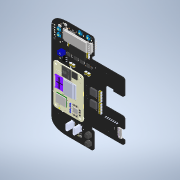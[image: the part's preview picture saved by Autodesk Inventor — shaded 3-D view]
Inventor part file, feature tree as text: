
AUTODESK INVENTOR PART (.ipt)
format: ipt  version: 2022 (Build 260153000, 153)  size: 56,215,552 bytes
history: native  units: mm
features: other x3630, sketch x2440, extrude x2
ambient origin geometry x8: Origin, YZ Plane, XZ Plane, XY Plane, X Axis, Y Axis, Z Axis, Center Point
bodies: Body1 (feature_tree), Body2 (feature_tree), Body3 (feature_tree), Body4 (feature_tree), Body5 (feature_tree), Body6 (feature_tree), Body7 (feature_tree), Body8 (feature_tree), Body9 (feature_tree), Body10 (feature_tree), Body11 (feature_tree), Body12 (feature_tree), Body13 (feature_tree), Body14 (feature_tree), Body15 (feature_tree), Body16 (feature_tree), Body17 (feature_tree), Body18 (feature_tree), Body19 (feature_tree), Body20 (feature_tree), Body21 (feature_tree), Body22 (feature_tree), Body23 (feature_tree), Body24 (feature_tree), Body25 (feature_tree), Body26 (feature_tree), Body27 (feature_tree), Body28 (feature_tree), Body29 (feature_tree), Body30 (feature_tree), Body31 (feature_tree), Body32 (feature_tree), Body33 (feature_tree), Body34 (feature_tree), Body35 (feature_tree), Body36 (feature_tree), Body37 (feature_tree), Body38 (feature_tree), Body39 (feature_tree), Body40 (feature_tree), Body41 (feature_tree), Body42 (feature_tree), Body43 (feature_tree), Body44 (feature_tree), Body45 (feature_tree), Body46 (feature_tree), Body47 (feature_tree), Body48 (feature_tree), Body49 (feature_tree), Body50 (feature_tree), Body51 (feature_tree), Body52 (feature_tree), Body53 (feature_tree), Body54 (feature_tree), Body55 (feature_tree), Body56 (feature_tree), Body57 (feature_tree), Body58 (feature_tree), Body59 (feature_tree), Body60 (feature_tree), Body61 (feature_tree), Body62 (feature_tree), Body63 (feature_tree), Body64 (feature_tree), Body65 (feature_tree), Body66 (feature_tree), Body67 (feature_tree), Body68 (feature_tree), Body69 (feature_tree), Body70 (feature_tree), Body71 (feature_tree), Body72 (feature_tree), Body73 (feature_tree), Body74 (feature_tree), Body75 (feature_tree), Body76 (feature_tree), Body77 (feature_tree), Body78 (feature_tree), Body79 (feature_tree), Body80 (feature_tree), Body81 (feature_tree), Body82 (feature_tree), Body83 (feature_tree), Body84 (feature_tree), Body85 (feature_tree), Body86 (feature_tree), Body87 (feature_tree), Body88 (feature_tree), Body89 (feature_tree), Body90 (feature_tree), Body91 (feature_tree), Body92 (feature_tree), Body93 (feature_tree), Body94 (feature_tree), Body95 (feature_tree), Body96 (feature_tree), Body97 (feature_tree), Body98 (feature_tree), Body99 (feature_tree), Body100 (feature_tree), Body101 (feature_tree), Body102 (feature_tree), Body103 (feature_tree), Body104 (feature_tree), Body105 (feature_tree), Body106 (feature_tree), Body107 (feature_tree), Body108 (feature_tree), Body109 (feature_tree), Body110 (feature_tree), Body111 (feature_tree), Body112 (feature_tree), Body113 (feature_tree), Body114 (feature_tree), Body115 (feature_tree), Body116 (feature_tree), Body117 (feature_tree), Body118 (feature_tree), Body119 (feature_tree), Body120 (feature_tree), Body121 (feature_tree), Body122 (feature_tree), Body123 (feature_tree), Body124 (feature_tree), Body125 (feature_tree), Body126 (feature_tree), Body127 (feature_tree), Body128 (feature_tree), Body129 (feature_tree), Body130 (feature_tree), Body131 (feature_tree), Body132 (feature_tree), Body133 (feature_tree), Body134 (feature_tree), Body135 (feature_tree), Body136 (feature_tree), Body137 (feature_tree), Body138 (feature_tree), Body139 (feature_tree), Body140 (feature_tree), Body141 (feature_tree), Body142 (feature_tree), Body143 (feature_tree), Body144 (feature_tree), Body145 (feature_tree), Body146 (feature_tree), Body147 (feature_tree), Body148 (feature_tree), Body149 (feature_tree), Body150 (feature_tree), Body151 (feature_tree), Body152 (feature_tree), Body153 (feature_tree), Body154 (feature_tree), Body155 (feature_tree), Body156 (feature_tree), Body157 (feature_tree), Body158 (feature_tree), Body159 (feature_tree), Body160 (feature_tree), Body161 (feature_tree), Body162 (feature_tree), Body163 (feature_tree), Body164 (feature_tree), Body165 (feature_tree), Body166 (feature_tree), Body167 (feature_tree), Body168 (feature_tree), Body169 (feature_tree), Body170 (feature_tree), Body171 (feature_tree), Body172 (feature_tree), Body173 (feature_tree), Body174 (feature_tree), Body175 (feature_tree), Body176 (feature_tree), Body177 (feature_tree), Body178 (feature_tree), Body179 (feature_tree), Body180 (feature_tree), Body181 (feature_tree), Body182 (feature_tree), Body183 (feature_tree), Body184 (feature_tree), Body185 (feature_tree), Body186 (feature_tree), Body187 (feature_tree), Body188 (feature_tree), Body189 (feature_tree), Body190 (feature_tree), Body191 (feature_tree), Body192 (feature_tree), Body193 (feature_tree), Body194 (feature_tree), Body195 (feature_tree), Body196 (feature_tree), Body197 (feature_tree), Body198 (feature_tree), Body199 (feature_tree), Body200 (feature_tree), Body201 (feature_tree), Body202 (feature_tree), Body203 (feature_tree), Body204 (feature_tree), Body205 (feature_tree), Body206 (feature_tree), Body207 (feature_tree), Body208 (feature_tree), Body209 (feature_tree), Body210 (feature_tree), Body211 (feature_tree), Body212 (feature_tree), Body213 (feature_tree), Body214 (feature_tree), Body215 (feature_tree), Body216 (feature_tree), Body217 (feature_tree), Body218 (feature_tree), Body219 (feature_tree), Body220 (feature_tree), Body221 (feature_tree), Body222 (feature_tree), Body223 (feature_tree), Body224 (feature_tree), Body225 (feature_tree), Body226 (feature_tree), Body227 (feature_tree), Body228 (feature_tree), Body229 (feature_tree), Body230 (feature_tree), Body231 (feature_tree), Body232 (feature_tree), Body233 (feature_tree), Body234 (feature_tree), Body235 (feature_tree), Body236 (feature_tree), Body237 (feature_tree), Body238 (feature_tree), Body239 (feature_tree), Body240 (feature_tree), Body241 (feature_tree), Body242 (feature_tree), Body243 (feature_tree), Body244 (feature_tree), Body245 (feature_tree), Body246 (feature_tree), Body247 (feature_tree), Body248 (feature_tree), Body249 (feature_tree), Body250 (feature_tree), Body251 (feature_tree), Body252 (feature_tree), Body253 (feature_tree), Body254 (feature_tree), Body255 (feature_tree), Body256 (feature_tree), Body257 (feature_tree), Body258 (feature_tree), Body259 (feature_tree), Body260 (feature_tree), Body261 (feature_tree), Body262 (feature_tree), Body263 (feature_tree), Body264 (feature_tree), Body265 (feature_tree), Body266 (feature_tree), Body267 (feature_tree), Body268 (feature_tree), Body269 (feature_tree), Body270 (feature_tree), Body271 (feature_tree), Body272 (feature_tree), Body273 (feature_tree), Body274 (feature_tree), Body275 (feature_tree), Body276 (feature_tree), Body277 (feature_tree), Body278 (feature_tree), Body279 (feature_tree), Body280 (feature_tree), Body281 (feature_tree), Body282 (feature_tree), Body283 (feature_tree), Body284 (feature_tree), Body285 (feature_tree), Body286 (feature_tree), Body287 (feature_tree), Body288 (feature_tree), Body289 (feature_tree), Body290 (feature_tree), Body291 (feature_tree), Body292 (feature_tree), Body293 (feature_tree), Body294 (feature_tree), Body295 (feature_tree), Body296 (feature_tree), Body297 (feature_tree), Body298 (feature_tree), Body299 (feature_tree), Body300 (feature_tree), Body301 (feature_tree), Body302 (feature_tree), Body303 (feature_tree), Body304 (feature_tree), Body305 (feature_tree), Body306 (feature_tree), Body307 (feature_tree), Body308 (feature_tree), Body309 (feature_tree), Body310 (feature_tree), Body311 (feature_tree), Body312 (feature_tree), Body313 (feature_tree), Body314 (feature_tree), Body315 (feature_tree), Body316 (feature_tree), Body317 (feature_tree), Body318 (feature_tree), Body319 (feature_tree), Body320 (feature_tree), Body321 (feature_tree), Body322 (feature_tree), Body323 (feature_tree), Body324 (feature_tree), Body325 (feature_tree), Body326 (feature_tree), Body327 (feature_tree), Body328 (feature_tree), Body329 (feature_tree), Body330 (feature_tree), Body331 (feature_tree), Body332 (feature_tree), Body333 (feature_tree), Body334 (feature_tree), Body335 (feature_tree), Body336 (feature_tree), Body337 (feature_tree), Body338 (feature_tree), Body339 (feature_tree), Body340 (feature_tree), Body341 (feature_tree), Body342 (feature_tree), Body343 (feature_tree), Body344 (feature_tree), Body345 (feature_tree), Body346 (feature_tree), Body347 (feature_tree), Body348 (feature_tree), Body349 (feature_tree), Body350 (feature_tree), Body351 (feature_tree), Body352 (feature_tree), Body353 (feature_tree), Body354 (feature_tree), Body355 (feature_tree), Body356 (feature_tree), Body357 (feature_tree), Body358 (feature_tree), Body359 (feature_tree), Body360 (feature_tree), Body361 (feature_tree), Body362 (feature_tree), Body363 (feature_tree), Body364 (feature_tree), Body365 (feature_tree), Body366 (feature_tree), Body367 (feature_tree), Body368 (feature_tree), Body369 (feature_tree), Body370 (feature_tree), Body371 (feature_tree), Body372 (feature_tree), Body373 (feature_tree), Body374 (feature_tree), Body375 (feature_tree), Body376 (feature_tree), Body377 (feature_tree), Body378 (feature_tree), Body379 (feature_tree), Body380 (feature_tree), Body381 (feature_tree), Body382 (feature_tree), Body383 (feature_tree), Body384 (feature_tree), Body385 (feature_tree), Body386 (feature_tree), Body387 (feature_tree), Body388 (feature_tree), Body389 (feature_tree), Body390 (feature_tree), Body391 (feature_tree), Body392 (feature_tree), Body393 (feature_tree), Body394 (feature_tree), Body395 (feature_tree), Body396 (feature_tree), Body397 (feature_tree), Body398 (feature_tree), Body399 (feature_tree), Body400 (feature_tree), Body401 (feature_tree), Body402 (feature_tree), Body403 (feature_tree), Body404 (feature_tree), Body405 (feature_tree), Body406 (feature_tree), Body407 (feature_tree), Body408 (feature_tree), Body409 (feature_tree), Body410 (feature_tree), Body411 (feature_tree), Body412 (feature_tree), Body413 (feature_tree), Body414 (feature_tree), Body415 (feature_tree), Body416 (feature_tree), Body417 (feature_tree), Body418 (feature_tree), Body419 (feature_tree), Body420 (feature_tree), Body421 (feature_tree), Body422 (feature_tree), Body423 (feature_tree), Body424 (feature_tree), Body425 (feature_tree), Body426 (feature_tree), Body427 (feature_tree), Body428 (feature_tree), Body429 (feature_tree), Body430 (feature_tree), Body431 (feature_tree), Body432 (feature_tree), Body433 (feature_tree), Body434 (feature_tree), Body435 (feature_tree), Body436 (feature_tree), Body437 (feature_tree), Body438 (feature_tree), Body439 (feature_tree), Body440 (feature_tree), Body441 (feature_tree), Body442 (feature_tree), Body443 (feature_tree), Body444 (feature_tree), Body445 (feature_tree), Body446 (feature_tree), Body447 (feature_tree), Body448 (feature_tree), Body449 (feature_tree), Body450 (feature_tree), Body451 (feature_tree), Body452 (feature_tree), Body453 (feature_tree), Body454 (feature_tree), Body455 (feature_tree), Body456 (feature_tree), Body457 (feature_tree), Body458 (feature_tree), Body459 (feature_tree), Body460 (feature_tree), Body461 (feature_tree), Body462 (feature_tree), Body463 (feature_tree), Body464 (feature_tree), Body465 (feature_tree), Body466 (feature_tree), Body467 (feature_tree), Body468 (feature_tree), Body469 (feature_tree), Body470 (feature_tree), Body471 (feature_tree), Body472 (feature_tree), Body473 (feature_tree), Body474 (feature_tree), Body475 (feature_tree), Body476 (feature_tree), Body477 (feature_tree), Body478 (feature_tree), Body479 (feature_tree), Body480 (feature_tree), Body481 (feature_tree), Body482 (feature_tree), Body483 (feature_tree), Body484 (feature_tree), Body485 (feature_tree), Body486 (feature_tree), Body487 (feature_tree), Body488 (feature_tree), Body489 (feature_tree), Body490 (feature_tree), Body491 (feature_tree), Body492 (feature_tree), Body493 (feature_tree), Body494 (feature_tree), Body495 (feature_tree), Body496 (feature_tree), Body497 (feature_tree), Body498 (feature_tree), Body499 (feature_tree), Body500 (feature_tree), Body501 (feature_tree), Body502 (feature_tree), Body503 (feature_tree), Body504 (feature_tree), Body505 (feature_tree), Body506 (feature_tree), Body507 (feature_tree), Body508 (feature_tree), Body509 (feature_tree), Body510 (feature_tree), Body511 (feature_tree), Body512 (feature_tree), Body513 (feature_tree), Body514 (feature_tree), Body515 (feature_tree), Body516 (feature_tree), Body517 (feature_tree), Body518 (feature_tree), Body519 (feature_tree), Body520 (feature_tree), Body521 (feature_tree), Body522 (feature_tree), Body523 (feature_tree), Body524 (feature_tree), Body525 (feature_tree), Body526 (feature_tree), Body527 (feature_tree), Body528 (feature_tree), Body529 (feature_tree), Body530 (feature_tree), Body531 (feature_tree), Body532 (feature_tree), Body533 (feature_tree), Body534 (feature_tree), Body535 (feature_tree), Body536 (feature_tree), Body537 (feature_tree), Body538 (feature_tree), Body539 (feature_tree), Body540 (feature_tree), Body541 (feature_tree), Body542 (feature_tree), Body543 (feature_tree), Body544 (feature_tree), Body545 (feature_tree), Body546 (feature_tree), Body547 (feature_tree), Body548 (feature_tree), Body549 (feature_tree), Body550 (feature_tree), Body551 (feature_tree), Body552 (feature_tree), Body553 (feature_tree), Body554 (feature_tree), Body555 (feature_tree), Body556 (feature_tree), Body557 (feature_tree), Body558 (feature_tree), Body559 (feature_tree), Body560 (feature_tree), Body561 (feature_tree), Body562 (feature_tree), Body563 (feature_tree), Body564 (feature_tree), Body565 (feature_tree), Body566 (feature_tree), Body567 (feature_tree), Body568 (feature_tree), Body569 (feature_tree), Body570 (feature_tree), Body571 (feature_tree), Body572 (feature_tree), Body573 (feature_tree), Body574 (feature_tree), Body575 (feature_tree), Body576 (feature_tree), Body577 (feature_tree), Body578 (feature_tree), Body579 (feature_tree), Body580 (feature_tree), Body581 (feature_tree), Body582 (feature_tree), Body583 (feature_tree), Body584 (feature_tree), Body585 (feature_tree), Body586 (feature_tree), Body587 (feature_tree), Body588 (feature_tree), Body589 (feature_tree), Body590 (feature_tree), Body591 (feature_tree), Body592 (feature_tree), Body593 (feature_tree), Body594 (feature_tree), Body595 (feature_tree), Body596 (feature_tree), Body597 (feature_tree), Body598 (feature_tree), Body599 (feature_tree), Body600 (feature_tree), Body601 (feature_tree), Body602 (feature_tree), Body603 (feature_tree), Body604 (feature_tree), Body605 (feature_tree), Body606 (feature_tree), Body607 (feature_tree), Body608 (feature_tree), Body609 (feature_tree), Body610 (feature_tree), Body611 (feature_tree), Body612 (feature_tree), Body613 (feature_tree), Body614 (feature_tree), Body615 (feature_tree), Body616 (feature_tree), Body617 (feature_tree), Body618 (feature_tree), Body619 (feature_tree), Body620 (feature_tree), Body621 (feature_tree), Body622 (feature_tree), Body623 (feature_tree), Body624 (feature_tree), Body625 (feature_tree), Body626 (feature_tree), Body627 (feature_tree), Body628 (feature_tree), Body629 (feature_tree), Body630 (feature_tree), Body631 (feature_tree), Body632 (feature_tree), Body633 (feature_tree), Body634 (feature_tree), Body635 (feature_tree), Body636 (feature_tree), Body637 (feature_tree), Body638 (feature_tree), Body639 (feature_tree), Body640 (feature_tree), Body641 (feature_tree), Body642 (feature_tree), Body643 (feature_tree), Body644 (feature_tree), Body645 (feature_tree), Body646 (feature_tree), Body647 (feature_tree), Body648 (feature_tree), Body649 (feature_tree), Body650 (feature_tree), Body651 (feature_tree), Body652 (feature_tree), Body653 (feature_tree), Body654 (feature_tree), Body655 (feature_tree), Body656 (feature_tree), Body657 (feature_tree), Body658 (feature_tree), Body659 (feature_tree), Body660 (feature_tree), Body661 (feature_tree), Body662 (feature_tree), Body663 (feature_tree), Body664 (feature_tree), Body665 (feature_tree), Body666 (feature_tree), Body667 (feature_tree), Body668 (feature_tree), Body669 (feature_tree), Body670 (feature_tree), Body671 (feature_tree), Body672 (feature_tree), Body673 (feature_tree), Body674 (feature_tree), Body675 (feature_tree), Body676 (feature_tree), Body677 (feature_tree), Body678 (feature_tree), Body679 (feature_tree), Body680 (feature_tree), Body681 (feature_tree), Body682 (feature_tree), Body683 (feature_tree), Body684 (feature_tree), Body685 (feature_tree), Body686 (feature_tree), Body687 (feature_tree), Body688 (feature_tree), Body689 (feature_tree), Body690 (feature_tree), Body691 (feature_tree), Body692 (feature_tree), Body693 (feature_tree), Body694 (feature_tree), Body695 (feature_tree), Body696 (feature_tree), Body697 (feature_tree), Body698 (feature_tree), Body699 (feature_tree), Body700 (feature_tree), Body701 (feature_tree), Body702 (feature_tree), Body703 (feature_tree), Body704 (feature_tree), Body705 (feature_tree), Body706 (feature_tree), Body707 (feature_tree), Body708 (feature_tree), Body709 (feature_tree), Body710 (feature_tree), Body711 (feature_tree), Body712 (feature_tree), Body713 (feature_tree), Body714 (feature_tree), Body715 (feature_tree), Body716 (feature_tree), Body717 (feature_tree), Body718 (feature_tree), Body719 (feature_tree), Body720 (feature_tree), Body721 (feature_tree), Body722 (feature_tree), Body723 (feature_tree), Body724 (feature_tree), Body725 (feature_tree), Body726 (feature_tree), Body727 (feature_tree), Body728 (feature_tree), Body729 (feature_tree), Body730 (feature_tree), Body731 (feature_tree), Body732 (feature_tree), Body733 (feature_tree), Body734 (feature_tree), Body735 (feature_tree), Body736 (feature_tree), Body737 (feature_tree), Body738 (feature_tree), Body739 (feature_tree), Body740 (feature_tree), Body741 (feature_tree), Body742 (feature_tree), Body743 (feature_tree), Body744 (feature_tree), Body745 (feature_tree), Body746 (feature_tree), Body747 (feature_tree), Body748 (feature_tree), Body749 (feature_tree), Body750 (feature_tree), Body751 (feature_tree), Body752 (feature_tree), Body753 (feature_tree), Body754 (feature_tree), Body755 (feature_tree), Body756 (feature_tree), Body757 (feature_tree), Body758 (feature_tree), Body759 (feature_tree), Body760 (feature_tree), Body761 (feature_tree), Body762 (feature_tree), Body763 (feature_tree), Body764 (feature_tree), Body765 (feature_tree), Body766 (feature_tree), Body767 (feature_tree), Body768 (feature_tree), Body769 (feature_tree), Body770 (feature_tree), Body771 (feature_tree), Body772 (feature_tree), Body773 (feature_tree), Body774 (feature_tree), Body775 (feature_tree), Body776 (feature_tree), Body777 (feature_tree), Body778 (feature_tree), Body779 (feature_tree), Body780 (feature_tree), Body781 (feature_tree), Body782 (feature_tree), Body783 (feature_tree), Body784 (feature_tree), Body785 (feature_tree), Body786 (feature_tree), Body787 (feature_tree), Body788 (feature_tree), Body789 (feature_tree), Body790 (feature_tree), Body791 (feature_tree), Body792 (feature_tree), Body793 (feature_tree), Body794 (feature_tree), Body795 (feature_tree), Body796 (feature_tree), Body797 (feature_tree), Body798 (feature_tree), Body799 (feature_tree), Body800 (feature_tree), Body801 (feature_tree), Body802 (feature_tree), Body803 (feature_tree), Body804 (feature_tree), Body805 (feature_tree), Body806 (feature_tree), Body807 (feature_tree), Body808 (feature_tree), Body809 (feature_tree), Body810 (feature_tree), Body811 (feature_tree), Body812 (feature_tree), Body813 (feature_tree), Body814 (feature_tree), Body815 (feature_tree), Body816 (feature_tree), Body817 (feature_tree), Body818 (feature_tree), Body819 (feature_tree), Body820 (feature_tree), Body821 (feature_tree), Body822 (feature_tree), Body823 (feature_tree), Body824 (feature_tree), Body825 (feature_tree), Body826 (feature_tree), Body827 (feature_tree), Body828 (feature_tree), Body829 (feature_tree), Body830 (feature_tree), Body831 (feature_tree), Body832 (feature_tree), Body833 (feature_tree), Body834 (feature_tree), Body835 (feature_tree), Body836 (feature_tree), Body837 (feature_tree), Body838 (feature_tree), Body839 (feature_tree), Body840 (feature_tree), Body841 (feature_tree), Body842 (feature_tree), Body843 (feature_tree), Body844 (feature_tree), Body845 (feature_tree), Body846 (feature_tree), Body847 (feature_tree), Body848 (feature_tree), Body849 (feature_tree), Body850 (feature_tree), Body851 (feature_tree), Body852 (feature_tree), Body853 (feature_tree), Body854 (feature_tree), Body855 (feature_tree), Body856 (feature_tree), Body857 (feature_tree), Body858 (feature_tree), Body859 (feature_tree), Body860 (feature_tree), Body861 (feature_tree), Body862 (feature_tree), Body863 (feature_tree), Body864 (feature_tree), Body865 (feature_tree), Body866 (feature_tree), Body867 (feature_tree), Body868 (feature_tree), Body869 (feature_tree), Body870 (feature_tree), Body871 (feature_tree), Body872 (feature_tree), Body873 (feature_tree), Body874 (feature_tree), Body875 (feature_tree), Body876 (feature_tree), Body877 (feature_tree), Body878 (feature_tree), Body879 (feature_tree), Body880 (feature_tree), Body881 (feature_tree), Body882 (feature_tree), Body883 (feature_tree), Body884 (feature_tree), Body885 (feature_tree), Body886 (feature_tree), Body887 (feature_tree), Body888 (feature_tree), Body889 (feature_tree), Body890 (feature_tree), Body891 (feature_tree), Body892 (feature_tree), Body893 (feature_tree), Body894 (feature_tree), Body895 (feature_tree), Body896 (feature_tree), Body897 (feature_tree), Body898 (feature_tree), Body899 (feature_tree), Body900 (feature_tree), Body901 (feature_tree), Body902 (feature_tree), Body903 (feature_tree), Body904 (feature_tree), Body905 (feature_tree), Body906 (feature_tree), Body907 (feature_tree), Body908 (feature_tree), Body909 (feature_tree), Body910 (feature_tree), Body911 (feature_tree), Body912 (feature_tree), Body913 (feature_tree), Body914 (feature_tree), Body915 (feature_tree), Body916 (feature_tree), Body917 (feature_tree), Body918 (feature_tree), Body919 (feature_tree), Body920 (feature_tree), Body921 (feature_tree), Body922 (feature_tree), Body923 (feature_tree), Body924 (feature_tree), Body925 (feature_tree), Body926 (feature_tree), Body927 (feature_tree), Body928 (feature_tree), Body929 (feature_tree), Body930 (feature_tree), Body931 (feature_tree), Body932 (feature_tree), Body933 (feature_tree), Body934 (feature_tree), Body935 (feature_tree), Body936 (feature_tree), Body937 (feature_tree), Body938 (feature_tree), Body939 (feature_tree), Body940 (feature_tree), Body941 (feature_tree), Body942 (feature_tree), Body943 (feature_tree), Body944 (feature_tree), Body945 (feature_tree), Body946 (feature_tree), Body947 (feature_tree), Body948 (feature_tree), Body949 (feature_tree), Body950 (feature_tree), Body951 (feature_tree), Body952 (feature_tree), Body953 (feature_tree), Body954 (feature_tree), Body955 (feature_tree), Body956 (feature_tree), Body957 (feature_tree), Body958 (feature_tree), Body959 (feature_tree), Body960 (feature_tree), Body961 (feature_tree), Body962 (feature_tree), Body963 (feature_tree), Body964 (feature_tree), Body965 (feature_tree), Body966 (feature_tree), Body967 (feature_tree), Body968 (feature_tree), Body969 (feature_tree), Body970 (feature_tree), Body971 (feature_tree), Body972 (feature_tree), Body973 (feature_tree), Body974 (feature_tree), Body975 (feature_tree), Body976 (feature_tree), Body977 (feature_tree), Body978 (feature_tree), Body979 (feature_tree), Body980 (feature_tree), Body981 (feature_tree), Body982 (feature_tree), Body983 (feature_tree), Body984 (feature_tree), Body985 (feature_tree), Body986 (feature_tree), Body987 (feature_tree), Body988 (feature_tree), Body989 (feature_tree), Body990 (feature_tree), Body991 (feature_tree), Body992 (feature_tree), Body993 (feature_tree), Body994 (feature_tree), Body995 (feature_tree), Body996 (feature_tree), Body997 (feature_tree), Body998 (feature_tree), Body999 (feature_tree), Body1000 (feature_tree), Body1001 (feature_tree), Body1002 (feature_tree), Body1003 (feature_tree), Body1004 (feature_tree), Body1005 (feature_tree), Body1006 (feature_tree), Body1007 (feature_tree), Body1008 (feature_tree), Body1009 (feature_tree), Body1010 (feature_tree), Body1011 (feature_tree), Body1012 (feature_tree), Body1013 (feature_tree), Body1014 (feature_tree), Body1015 (feature_tree), Body1016 (feature_tree), Body1017 (feature_tree), Body1018 (feature_tree), Body1019 (feature_tree), Body1020 (feature_tree), Body1021 (feature_tree), Body1022 (feature_tree), Body1023 (feature_tree), Body1024 (feature_tree), Body1025 (feature_tree), Body1026 (feature_tree), Body1027 (feature_tree), Body1028 (feature_tree), Body1029 (feature_tree), Body1030 (feature_tree), Body1031 (feature_tree), Body1032 (feature_tree), Body1033 (feature_tree), Body1034 (feature_tree), Body1035 (feature_tree), Body1036 (feature_tree), Body1037 (feature_tree), Body1038 (feature_tree), Body1039 (feature_tree), Body1040 (feature_tree), Body1041 (feature_tree), Body1042 (feature_tree), Body1043 (feature_tree), Body1044 (feature_tree), Body1045 (feature_tree), Body1046 (feature_tree), Body1047 (feature_tree), Body1048 (feature_tree), Body1049 (feature_tree), Body1050 (feature_tree), Body1051 (feature_tree), Body1052 (feature_tree), Body1053 (feature_tree), Body1054 (feature_tree), Body1055 (feature_tree), Body1056 (feature_tree), Body1057 (feature_tree), Body1058 (feature_tree), Body1059 (feature_tree), Body1060 (feature_tree), Body1061 (feature_tree), Body1062 (feature_tree), Body1063 (feature_tree), Body1064 (feature_tree), Body1065 (feature_tree), Body1066 (feature_tree), Body1067 (feature_tree), Body1068 (feature_tree), Body1069 (feature_tree), Body1070 (feature_tree), Body1071 (feature_tree), Body1072 (feature_tree), Body1073 (feature_tree), Body1074 (feature_tree), Body1075 (feature_tree), Body1076 (feature_tree), Body1077 (feature_tree), Body1078 (feature_tree), Body1079 (feature_tree), Body1080 (feature_tree), Body1081 (feature_tree), Body1082 (feature_tree), Body1083 (feature_tree), Body1084 (feature_tree), Body1085 (feature_tree), Body1086 (feature_tree), Body1087 (feature_tree), Body1088 (feature_tree), Body1089 (feature_tree), Body1090 (feature_tree), Body1091 (feature_tree), Body1092 (feature_tree), Body1093 (feature_tree), Body1094 (feature_tree), Body1095 (feature_tree), Body1096 (feature_tree), Body1097 (feature_tree), Body1098 (feature_tree), Body1099 (feature_tree), Body1100 (feature_tree), Body1101 (feature_tree), Body1102 (feature_tree), Body1103 (feature_tree), Body1104 (feature_tree), Body1105 (feature_tree), Body1106 (feature_tree), Body1107 (feature_tree), Body1108 (feature_tree), Body1109 (feature_tree), Body1110 (feature_tree), Body1111 (feature_tree), Body1112 (feature_tree), Body1113 (feature_tree), Body1114 (feature_tree), Body1115 (feature_tree), Body1116 (feature_tree), Body1117 (feature_tree), Body1118 (feature_tree), Body1119 (feature_tree), Body1120 (feature_tree), Body1121 (feature_tree), Body1122 (feature_tree), Body1123 (feature_tree), Body1124 (feature_tree), Body1125 (feature_tree), Body1126 (feature_tree), Body1127 (feature_tree), Body1128 (feature_tree), Body1129 (feature_tree), Body1130 (feature_tree), Body1131 (feature_tree), Body1132 (feature_tree), Body1133 (feature_tree), Body1134 (feature_tree), Body1135 (feature_tree), Body1136 (feature_tree), Body1137 (feature_tree), Body1138 (feature_tree), Body1139 (feature_tree), Body1140 (feature_tree), Body1141 (feature_tree), Body1142 (feature_tree), Body1143 (feature_tree), Body1144 (feature_tree), Body1145 (feature_tree), Body1146 (feature_tree), Body1147 (feature_tree), Body1148 (feature_tree), Body1149 (feature_tree), Body1150 (feature_tree), Body1151 (feature_tree), Body1152 (feature_tree), Body1153 (feature_tree), Body1154 (feature_tree), Body1155 (feature_tree), Body1156 (feature_tree), Body1157 (feature_tree), Body1158 (feature_tree), Body1159 (feature_tree), Body1160 (feature_tree), Body1161 (feature_tree), Body1162 (feature_tree), Body1163 (feature_tree), Body1164 (feature_tree), Body1165 (feature_tree), Body1166 (feature_tree), Body1167 (feature_tree), Body1168 (feature_tree), Body1169 (feature_tree), Body1170 (feature_tree), Body1171 (feature_tree), Body1172 (feature_tree), Body1173 (feature_tree), Body1174 (feature_tree), Body1175 (feature_tree), Body1176 (feature_tree), Body1177 (feature_tree), Body1178 (feature_tree), Body1179 (feature_tree), Body1180 (feature_tree), Body1181 (feature_tree), Body1182 (feature_tree), Body1183 (feature_tree), Body1184 (feature_tree), Body1185 (feature_tree), Body1186 (feature_tree), Body1187 (feature_tree), Body1188 (feature_tree), Body1189 (feature_tree), Body1190 (feature_tree), Body1191 (feature_tree), Body1192 (feature_tree), Body1193 (feature_tree), Body1194 (feature_tree), Body1195 (feature_tree), Body1196 (feature_tree), Body1197 (feature_tree), Body1198 (feature_tree), Body1199 (feature_tree), Body1200 (feature_tree), Body1201 (feature_tree), Body1202 (feature_tree), Body1203 (feature_tree), Body1204 (feature_tree), Body1205 (feature_tree), Body1206 (feature_tree), Body1207 (feature_tree), Body1208 (feature_tree), Body1209 (feature_tree), Body1210 (feature_tree), Body1211 (feature_tree), Body1212 (feature_tree), Body1213 (feature_tree), Body1214 (feature_tree), Body1215 (feature_tree), Body1216 (feature_tree), Body1217 (feature_tree), Body1218 (feature_tree), Body1219 (feature_tree), Body1220 (feature_tree), Body1221 (feature_tree), Body1222 (feature_tree), Body1223 (feature_tree), Body1224 (feature_tree), Body1225 (feature_tree), Body1226 (feature_tree), Body1227 (feature_tree), Body1228 (feature_tree), Body1229 (feature_tree), Body1230 (feature_tree), Body1231 (feature_tree), Body1232 (feature_tree), Body1233 (feature_tree), Body1234 (feature_tree), Body1235 (feature_tree), Body1236 (feature_tree), Body1237 (feature_tree), Body1238 (feature_tree), Body1239 (feature_tree), Body1240 (feature_tree), Body1241 (feature_tree), Body1242 (feature_tree), Body1243 (feature_tree), Body1244 (feature_tree), Body1245 (feature_tree), Body1246 (feature_tree), Body1247 (feature_tree), Body1248 (feature_tree), Body1249 (feature_tree), Body1250 (feature_tree), Body1251 (feature_tree), Body1252 (feature_tree), Body1253 (feature_tree), Body1254 (feature_tree), Body1255 (feature_tree), Body1256 (feature_tree), Body1257 (feature_tree), Body1258 (feature_tree), Body1259 (feature_tree), Body1260 (feature_tree), Body1261 (feature_tree), Body1262 (feature_tree), Body1263 (feature_tree), Body1264 (feature_tree), Body1265 (feature_tree), Body1266 (feature_tree), Body1267 (feature_tree), Body1268 (feature_tree), Body1269 (feature_tree), Body1270 (feature_tree), Body1271 (feature_tree), Body1272 (feature_tree), Body1273 (feature_tree), Body1274 (feature_tree), Body1275 (feature_tree), Body1276 (feature_tree), Body1277 (feature_tree), Body1278 (feature_tree), Body1279 (feature_tree), Body1280 (feature_tree), Body1281 (feature_tree), Body1282 (feature_tree), Body1283 (feature_tree), Body1284 (feature_tree), Body1285 (feature_tree), Body1286 (feature_tree), Body1287 (feature_tree), Body1288 (feature_tree), Body1289 (feature_tree), Body1290 (feature_tree), Body1291 (feature_tree), Body1292 (feature_tree), Body1293 (feature_tree), Body1294 (feature_tree), Body1295 (feature_tree), Body1296 (feature_tree), Body1297 (feature_tree), Body1298 (feature_tree), Body1299 (feature_tree), Body1300 (feature_tree), Body1301 (feature_tree), Body1302 (feature_tree), Body1303 (feature_tree), Body1304 (feature_tree), Body1305 (feature_tree), Body1306 (feature_tree), Body1307 (feature_tree), Body1308 (feature_tree), Body1309 (feature_tree), Body1310 (feature_tree), Body1311 (feature_tree), Body1312 (feature_tree), Body1313 (feature_tree), Body1314 (feature_tree), Body1315 (feature_tree), Body1316 (feature_tree), Body1317 (feature_tree), Body1318 (feature_tree), Body1319 (feature_tree), Body1320 (feature_tree), Body1321 (feature_tree), Body1322 (feature_tree), Body1323 (feature_tree), Body1324 (feature_tree), Body1325 (feature_tree), Body1326 (feature_tree), Body1327 (feature_tree), Body1328 (feature_tree), Body1329 (feature_tree), Body1330 (feature_tree), Body1331 (feature_tree), Body1332 (feature_tree), Body1333 (feature_tree), Body1334 (feature_tree), Body1335 (feature_tree), Body1336 (feature_tree), Body1337 (feature_tree), Body1338 (feature_tree), Body1339 (feature_tree), Body1340 (feature_tree), Body1341 (feature_tree), Body1342 (feature_tree), Body1343 (feature_tree), Body1344 (feature_tree), Body1345 (feature_tree), Body1346 (feature_tree), Body1347 (feature_tree), Body1348 (feature_tree), Body1349 (feature_tree), Body1350 (feature_tree), Body1351 (feature_tree), Body1352 (feature_tree), Body1353 (feature_tree), Body1354 (feature_tree), Body1355 (feature_tree), Body1356 (feature_tree), Body1357 (feature_tree), Body1358 (feature_tree), Body1359 (feature_tree), Body1360 (feature_tree), Body1361 (feature_tree), Body1362 (feature_tree), Body1363 (feature_tree), Body1364 (feature_tree), Body1365 (feature_tree), Body1366 (feature_tree), Body1367 (feature_tree), Body1368 (feature_tree), Body1369 (feature_tree), Body1370 (feature_tree), Body1371 (feature_tree), Body1372 (feature_tree), Body1373 (feature_tree), Body1374 (feature_tree), Body1375 (feature_tree), Body1376 (feature_tree), Body1377 (feature_tree), Body1378 (feature_tree), Body1379 (feature_tree), Body1380 (feature_tree), Body1381 (feature_tree), Body1382 (feature_tree), Body1383 (feature_tree), Body1384 (feature_tree), Body1385 (feature_tree), Body1386 (feature_tree), Body1387 (feature_tree), Body1388 (feature_tree), Body1389 (feature_tree), Body1390 (feature_tree), Body1391 (feature_tree), Body1392 (feature_tree), Body1393 (feature_tree), Body1394 (feature_tree), Body1395 (feature_tree), Body1396 (feature_tree), Body1397 (feature_tree), Body1398 (feature_tree), Body1399 (feature_tree), Body1400 (feature_tree), Body1401 (feature_tree), Body1402 (feature_tree), Body1403 (feature_tree), Body1404 (feature_tree), Body1405 (feature_tree), Body1406 (feature_tree), Body1407 (feature_tree), Body1408 (feature_tree), Body1409 (feature_tree), Body1410 (feature_tree), Body1411 (feature_tree), Body1412 (feature_tree), Body1413 (feature_tree), Body1414 (feature_tree), Body1415 (feature_tree), Body1416 (feature_tree), Body1417 (feature_tree), Body1418 (feature_tree), Body1419 (feature_tree), Body1420 (feature_tree), Body1421 (feature_tree), Body1422 (feature_tree), Body1423 (feature_tree), Body1424 (feature_tree), Body1425 (feature_tree), Body1426 (feature_tree), Body1427 (feature_tree), Body1428 (feature_tree), Body1429 (feature_tree), Body1430 (feature_tree), Body1431 (feature_tree), Body1432 (feature_tree), Body1433 (feature_tree), Body1434 (feature_tree), Body1435 (feature_tree), Body1436 (feature_tree), Body1437 (feature_tree), Body1438 (feature_tree), Body1439 (feature_tree), Body1440 (feature_tree), Body1441 (feature_tree), Body1442 (feature_tree), Body1443 (feature_tree), Body1444 (feature_tree), Body1445 (feature_tree), Body1446 (feature_tree), Body1447 (feature_tree), Body1448 (feature_tree), Body1449 (feature_tree), Body1450 (feature_tree), Body1451 (feature_tree), Body1452 (feature_tree), Body1453 (feature_tree), Body1454 (feature_tree), Body1455 (feature_tree), Body1456 (feature_tree), Body1457 (feature_tree), Body1458 (feature_tree), Body1459 (feature_tree), Body1460 (feature_tree), Body1461 (feature_tree), Body1462 (feature_tree), Body1463 (feature_tree), Body1464 (feature_tree), Body1465 (feature_tree), Body1466 (feature_tree), Body1467 (feature_tree), Body1468 (feature_tree), Body1469 (feature_tree), Body1470 (feature_tree), Body1471 (feature_tree), Body1472 (feature_tree), Body1473 (feature_tree), Body1474 (feature_tree), Body1475 (feature_tree), Body1476 (feature_tree), Body1477 (feature_tree), Body1478 (feature_tree), Body1479 (feature_tree), Body1480 (feature_tree), Body1481 (feature_tree), Body1482 (feature_tree), Body1483 (feature_tree), Body1484 (feature_tree), Body1485 (feature_tree), Body1486 (feature_tree), Body1487 (feature_tree), Body1488 (feature_tree), Body1489 (feature_tree), Body1490 (feature_tree), Body1491 (feature_tree), Body1492 (feature_tree), Body1493 (feature_tree), Body1494 (feature_tree), Body1495 (feature_tree), Body1496 (feature_tree), Body1497 (feature_tree), Body1498 (feature_tree), Body1499 (feature_tree), Body1500 (feature_tree), Body1501 (feature_tree), Body1502 (feature_tree), Body1503 (feature_tree), Body1504 (feature_tree), Body1505 (feature_tree), Body1506 (feature_tree), Body1507 (feature_tree), Body1508 (feature_tree), Body1509 (feature_tree), Body1510 (feature_tree), Body1511 (feature_tree), Body1512 (feature_tree), Body1513 (feature_tree), Body1514 (feature_tree), Body1515 (feature_tree), Body1516 (feature_tree), Body1517 (feature_tree), Body1518 (feature_tree), Body1519 (feature_tree), Body1520 (feature_tree), Body1521 (feature_tree), Body1522 (feature_tree), Body1523 (feature_tree), Body1524 (feature_tree), Body1525 (feature_tree), Body1526 (feature_tree), Body1527 (feature_tree), Body1528 (feature_tree), Body1529 (feature_tree), Body1530 (feature_tree), Body1531 (feature_tree), Body1532 (feature_tree), Body1533 (feature_tree), Body1534 (feature_tree), Body1535 (feature_tree), Body1536 (feature_tree), Body1537 (feature_tree), Body1538 (feature_tree), Body1539 (feature_tree), Body1540 (feature_tree), Body1541 (feature_tree), Body1542 (feature_tree), Body1543 (feature_tree), Body1544 (feature_tree), Body1545 (feature_tree), Body1546 (feature_tree), Body1547 (feature_tree), Body1548 (feature_tree), Body1549 (feature_tree), Body1550 (feature_tree), Body1551 (feature_tree), Body1552 (feature_tree), Body1553 (feature_tree), Body1554 (feature_tree), Body1555 (feature_tree), Body1556 (feature_tree), Body1557 (feature_tree), Body1558 (feature_tree), Body1559 (feature_tree), Body1560 (feature_tree), Body1561 (feature_tree), Body1562 (feature_tree), Body1563 (feature_tree), Body1564 (feature_tree), Body1565 (feature_tree), Body1566 (feature_tree), Body1567 (feature_tree), Body1568 (feature_tree), Body1569 (feature_tree), Body1570 (feature_tree), Body1571 (feature_tree), Body1572 (feature_tree), Body1573 (feature_tree), Body1574 (feature_tree), Body1575 (feature_tree), Body1576 (feature_tree), Body1577 (feature_tree), Body1578 (feature_tree), Body1579 (feature_tree), Body1580 (feature_tree), Body1581 (feature_tree), Body1582 (feature_tree), Body1583 (feature_tree), Body1584 (feature_tree), Body1585 (feature_tree), Body1586 (feature_tree), Body1587 (feature_tree), Body1588 (feature_tree), Body1589 (feature_tree), Body1590 (feature_tree), Body1591 (feature_tree), Body1592 (feature_tree), Body1593 (feature_tree), Body1594 (feature_tree), Body1595 (feature_tree), Body1596 (feature_tree), Body1597 (feature_tree), Body1598 (feature_tree), Body1599 (feature_tree), Body1600 (feature_tree), Body1601 (feature_tree), Body1602 (feature_tree), Body1603 (feature_tree), Body1604 (feature_tree), Body1605 (feature_tree), Body1606 (feature_tree), Body1607 (feature_tree), Body1608 (feature_tree), Body1609 (feature_tree), Body1610 (feature_tree), Body1611 (feature_tree), Body1612 (feature_tree), Body1613 (feature_tree), Body1614 (feature_tree), Body1615 (feature_tree), Body1616 (feature_tree), Body1617 (feature_tree), Body1618 (feature_tree), Body1619 (feature_tree), Body1620 (feature_tree), Body1621 (feature_tree), Body1622 (feature_tree), Body1623 (feature_tree), Body1624 (feature_tree), Body1625 (feature_tree), Body1626 (feature_tree), Body1627 (feature_tree), Body1628 (feature_tree), Body1629 (feature_tree), Body1630 (feature_tree), Body1631 (feature_tree), Body1632 (feature_tree), Body1633 (feature_tree), Body1634 (feature_tree), Body1635 (feature_tree), Body1636 (feature_tree), Body1637 (feature_tree), Body1638 (feature_tree), Body1639 (feature_tree), Body1640 (feature_tree), Body1641 (feature_tree), Body1642 (feature_tree), Body1643 (feature_tree), Body1644 (feature_tree), Body1645 (feature_tree), Body1646 (feature_tree), Body1647 (feature_tree), Body1648 (feature_tree), Body1649 (feature_tree), Body1650 (feature_tree), Body1651 (feature_tree), Body1652 (feature_tree), Body1653 (feature_tree), Body1654 (feature_tree), Body1655 (feature_tree), Body1656 (feature_tree), Body1657 (feature_tree), Body1658 (feature_tree), Body1659 (feature_tree), Body1660 (feature_tree), Body1661 (feature_tree), Body1662 (feature_tree), Body1663 (feature_tree), Body1664 (feature_tree), Body1665 (feature_tree), Body1666 (feature_tree), Body1667 (feature_tree), Body1668 (feature_tree), Body1669 (feature_tree), Body1670 (feature_tree), Body1671 (feature_tree), Body1672 (feature_tree), Body1673 (feature_tree), Body1674 (feature_tree), Body1675 (feature_tree), Body1676 (feature_tree), Body1677 (feature_tree), Body1678 (feature_tree), Body1679 (feature_tree), Body1680 (feature_tree), Body1681 (feature_tree), Body1682 (feature_tree), Body1683 (feature_tree), Body1684 (feature_tree), Body1685 (feature_tree), Body1686 (feature_tree), Body1687 (feature_tree), Body1688 (feature_tree), Body1689 (feature_tree), Body1690 (feature_tree), Body1691 (feature_tree), Body1692 (feature_tree), Body1693 (feature_tree), Body1694 (feature_tree), Body1695 (feature_tree), Body1696 (feature_tree), Body1697 (feature_tree), Body1698 (feature_tree), Body1699 (feature_tree), Body1700 (feature_tree), Body1701 (feature_tree), Body1702 (feature_tree), Body1703 (feature_tree), Body1704 (feature_tree), Body1705 (feature_tree), Body1706 (feature_tree), Body1707 (feature_tree), Body1708 (feature_tree), Body1709 (feature_tree), Body1710 (feature_tree), Body1711 (feature_tree), Body1712 (feature_tree), Body1713 (feature_tree), Body1714 (feature_tree), Body1715 (feature_tree), Body1716 (feature_tree), Body1717 (feature_tree), Body1718 (feature_tree), Body1719 (feature_tree), Body1720 (feature_tree), Body1721 (feature_tree), Body1722 (feature_tree), Body1723 (feature_tree), Body1724 (feature_tree), Body1725 (feature_tree), Body1726 (feature_tree), Body1727 (feature_tree), Body1728 (feature_tree), Body1729 (feature_tree), Body1730 (feature_tree), Body1731 (feature_tree), Body1732 (feature_tree), Body1733 (feature_tree), Body1734 (feature_tree), Body1735 (feature_tree), Body1736 (feature_tree), Body1737 (feature_tree), Body1738 (feature_tree), Body1739 (feature_tree), Body1740 (feature_tree), Body1741 (feature_tree), Body1742 (feature_tree), Body1743 (feature_tree), Body1744 (feature_tree), Body1745 (feature_tree), Body1746 (feature_tree), Body1747 (feature_tree), Body1748 (feature_tree), Body1749 (feature_tree), Body1750 (feature_tree), Body1751 (feature_tree), Body1752 (feature_tree), Body1753 (feature_tree), Body1754 (feature_tree), Body1755 (feature_tree), Body1756 (feature_tree), Body1757 (feature_tree), Body1758 (feature_tree), Body1759 (feature_tree), Body1760 (feature_tree), Body1761 (feature_tree), Body1762 (feature_tree), Body1763 (feature_tree), Body1764 (feature_tree), Body1765 (feature_tree), Body1766 (feature_tree), Body1767 (feature_tree), Body1768 (feature_tree), Body1769 (feature_tree), Body1770 (feature_tree), Body1771 (feature_tree), Body1772 (feature_tree), Body1773 (feature_tree), Body1774 (feature_tree), Body1775 (feature_tree), Body1776 (feature_tree), Body1777 (feature_tree), Body1778 (feature_tree), Body1779 (feature_tree), Body1780 (feature_tree), Body1781 (feature_tree), Body1782 (feature_tree), Body1783 (feature_tree), Body1784 (feature_tree), Body1785 (feature_tree), Body1786 (feature_tree), Body1787 (feature_tree), Body1788 (feature_tree), Body1789 (feature_tree), Body1790 (feature_tree), Body1791 (feature_tree), Body1792 (feature_tree), Body1793 (feature_tree), Body1794 (feature_tree), Body1795 (feature_tree), Body1796 (feature_tree), Body1797 (feature_tree), Body1798 (feature_tree), Body1799 (feature_tree), Body1800 (feature_tree), Body1801 (feature_tree), Body1802 (feature_tree), Body1803 (feature_tree), Body1804 (feature_tree), Body1805 (feature_tree), Body1806 (feature_tree), Body1807 (feature_tree), Body1808 (feature_tree), Body1809 (feature_tree), Body1810 (feature_tree), Body1811 (feature_tree), Body1812 (feature_tree), Body1813 (feature_tree), Body1814 (feature_tree), Body1815 (feature_tree), Body1816 (feature_tree), Body1817 (feature_tree)
feature tree (6072):
  other  "Твердое тело1"
  other  "Исправленная геометрия1"
  sketch  "3D эскиз1"
  sketch  "3D эскиз2"
  sketch  "3D эскиз3"
  sketch  "3D эскиз4"
  sketch  "3D эскиз5"
  sketch  "3D эскиз6"
  sketch  "3D эскиз7"
  sketch  "3D эскиз8"
  sketch  "3D эскиз9"
  sketch  "3D эскиз10"
  sketch  "3D эскиз11"
  sketch  "3D эскиз12"
  sketch  "3D эскиз13"
  sketch  "3D эскиз14"
  sketch  "3D эскиз15"
  sketch  "3D эскиз16"
  sketch  "3D эскиз17"
  sketch  "3D эскиз18"
  sketch  "3D эскиз19"
  sketch  "3D эскиз20"
  sketch  "3D эскиз21"
  sketch  "3D эскиз22"
  sketch  "3D эскиз23"
  sketch  "3D эскиз24"
  sketch  "3D эскиз25"
  sketch  "3D эскиз26"
  sketch  "3D эскиз27"
  sketch  "3D эскиз28"
  sketch  "3D эскиз29"
  sketch  "3D эскиз30"
  sketch  "3D эскиз31"
  sketch  "3D эскиз32"
  sketch  "3D эскиз33"
  sketch  "3D эскиз34"
  sketch  "3D эскиз35"
  sketch  "3D эскиз36"
  sketch  "3D эскиз37"
  sketch  "3D эскиз38"
  sketch  "3D эскиз39"
  sketch  "3D эскиз40"
  sketch  "3D эскиз41"
  sketch  "3D эскиз42"
  sketch  "3D эскиз43"
  sketch  "3D эскиз44"
  sketch  "3D эскиз45"
  sketch  "3D эскиз46"
  sketch  "3D эскиз47"
  sketch  "3D эскиз48"
  sketch  "3D эскиз49"
  sketch  "3D эскиз50"
  sketch  "3D эскиз51"
  sketch  "3D эскиз52"
  sketch  "3D эскиз53"
  sketch  "3D эскиз54"
  sketch  "3D эскиз55"
  sketch  "3D эскиз56"
  sketch  "3D эскиз57"
  sketch  "3D эскиз58"
  sketch  "3D эскиз59"
  sketch  "3D эскиз60"
  sketch  "3D эскиз61"
  sketch  "3D эскиз62"
  sketch  "3D эскиз63"
  sketch  "3D эскиз64"
  sketch  "3D эскиз65"
  sketch  "3D эскиз66"
  sketch  "3D эскиз67"
  sketch  "3D эскиз68"
  sketch  "3D эскиз69"
  sketch  "3D эскиз70"
  sketch  "3D эскиз71"
  sketch  "3D эскиз72"
  sketch  "3D эскиз73"
  sketch  "3D эскиз74"
  sketch  "3D эскиз75"
  sketch  "3D эскиз76"
  sketch  "3D эскиз77"
  sketch  "3D эскиз78"
  sketch  "3D эскиз79"
  sketch  "3D эскиз80"
  sketch  "3D эскиз81"
  sketch  "3D эскиз82"
  sketch  "3D эскиз83"
  sketch  "3D эскиз84"
  sketch  "3D эскиз85"
  sketch  "3D эскиз86"
  sketch  "3D эскиз87"
  sketch  "3D эскиз88"
  sketch  "3D эскиз89"
  sketch  "3D эскиз90"
  sketch  "3D эскиз91"
  sketch  "3D эскиз92"
  sketch  "3D эскиз93"
  sketch  "3D эскиз94"
  sketch  "3D эскиз95"
  sketch  "3D эскиз96"
  sketch  "3D эскиз97"
  sketch  "3D эскиз98"
  sketch  "3D эскиз99"
  sketch  "3D эскиз100"
  sketch  "3D эскиз101"
  sketch  "3D эскиз102"
  sketch  "3D эскиз103"
  sketch  "3D эскиз104"
  sketch  "3D эскиз105"
  sketch  "3D эскиз106"
  sketch  "3D эскиз107"
  sketch  "3D эскиз108"
  sketch  "3D эскиз109"
  sketch  "3D эскиз110"
  sketch  "3D эскиз111"
  sketch  "3D эскиз112"
  sketch  "3D эскиз113"
  sketch  "3D эскиз114"
  sketch  "3D эскиз115"
  sketch  "3D эскиз116"
  sketch  "3D эскиз117"
  sketch  "3D эскиз118"
  sketch  "3D эскиз119"
  sketch  "3D эскиз120"
  sketch  "3D эскиз121"
  sketch  "3D эскиз122"
  sketch  "3D эскиз123"
  sketch  "3D эскиз124"
  sketch  "3D эскиз125"
  sketch  "3D эскиз126"
  sketch  "3D эскиз127"
  sketch  "3D эскиз128"
  sketch  "3D эскиз129"
  sketch  "3D эскиз130"
  sketch  "3D эскиз131"
  sketch  "3D эскиз132"
  sketch  "3D эскиз133"
  sketch  "3D эскиз134"
  sketch  "3D эскиз135"
  sketch  "3D эскиз136"
  sketch  "3D эскиз137"
  sketch  "3D эскиз138"
  sketch  "3D эскиз139"
  sketch  "3D эскиз140"
  sketch  "3D эскиз141"
  sketch  "3D эскиз142"
  sketch  "3D эскиз143"
  sketch  "3D эскиз144"
  sketch  "3D эскиз145"
  sketch  "3D эскиз146"
  sketch  "3D эскиз147"
  sketch  "3D эскиз148"
  sketch  "3D эскиз149"
  sketch  "3D эскиз150"
  sketch  "3D эскиз151"
  sketch  "3D эскиз152"
  sketch  "3D эскиз153"
  sketch  "3D эскиз154"
  sketch  "3D эскиз155"
  sketch  "3D эскиз156"
  sketch  "3D эскиз157"
  sketch  "3D эскиз158"
  sketch  "3D эскиз159"
  sketch  "3D эскиз160"
  sketch  "3D эскиз161"
  sketch  "3D эскиз162"
  sketch  "3D эскиз163"
  sketch  "3D эскиз164"
  sketch  "3D эскиз165"
  sketch  "3D эскиз166"
  sketch  "3D эскиз167"
  sketch  "3D эскиз168"
  sketch  "3D эскиз169"
  sketch  "3D эскиз170"
  sketch  "3D эскиз171"
  sketch  "3D эскиз172"
  sketch  "3D эскиз173"
  sketch  "3D эскиз174"
  sketch  "3D эскиз175"
  sketch  "3D эскиз176"
  sketch  "3D эскиз177"
  sketch  "3D эскиз178"
  sketch  "3D эскиз179"
  sketch  "3D эскиз180"
  sketch  "3D эскиз181"
  sketch  "3D эскиз182"
  sketch  "3D эскиз183"
  sketch  "3D эскиз184"
  sketch  "3D эскиз185"
  sketch  "3D эскиз186"
  sketch  "3D эскиз187"
  sketch  "3D эскиз188"
  sketch  "3D эскиз189"
  sketch  "3D эскиз190"
  sketch  "3D эскиз191"
  sketch  "3D эскиз192"
  sketch  "3D эскиз193"
  sketch  "3D эскиз194"
  sketch  "3D эскиз195"
  sketch  "3D эскиз196"
  sketch  "3D эскиз197"
  sketch  "3D эскиз198"
  sketch  "3D эскиз199"
  sketch  "3D эскиз200"
  sketch  "3D эскиз201"
  sketch  "3D эскиз202"
  sketch  "3D эскиз203"
  sketch  "3D эскиз204"
  sketch  "3D эскиз205"
  sketch  "3D эскиз206"
  sketch  "3D эскиз207"
  sketch  "3D эскиз208"
  sketch  "3D эскиз209"
  sketch  "3D эскиз210"
  sketch  "3D эскиз211"
  sketch  "3D эскиз212"
  sketch  "3D эскиз213"
  sketch  "3D эскиз214"
  sketch  "3D эскиз215"
  sketch  "3D эскиз216"
  sketch  "3D эскиз217"
  sketch  "3D эскиз218"
  sketch  "3D эскиз219"
  sketch  "3D эскиз220"
  sketch  "3D эскиз221"
  sketch  "3D эскиз222"
  sketch  "3D эскиз223"
  sketch  "3D эскиз224"
  sketch  "3D эскиз225"
  sketch  "3D эскиз226"
  sketch  "3D эскиз227"
  sketch  "3D эскиз228"
  sketch  "3D эскиз229"
  sketch  "3D эскиз230"
  sketch  "3D эскиз231"
  sketch  "3D эскиз232"
  sketch  "3D эскиз233"
  sketch  "3D эскиз234"
  sketch  "3D эскиз235"
  sketch  "3D эскиз236"
  sketch  "3D эскиз237"
  sketch  "3D эскиз238"
  sketch  "3D эскиз239"
  sketch  "3D эскиз240"
  sketch  "3D эскиз241"
  sketch  "3D эскиз242"
  sketch  "3D эскиз243"
  sketch  "3D эскиз244"
  sketch  "3D эскиз245"
  sketch  "3D эскиз246"
  sketch  "3D эскиз247"
  sketch  "3D эскиз248"
  sketch  "3D эскиз249"
  sketch  "3D эскиз250"
  sketch  "3D эскиз251"
  sketch  "3D эскиз252"
  sketch  "3D эскиз253"
  sketch  "3D эскиз254"
  sketch  "3D эскиз255"
  sketch  "3D эскиз256"
  sketch  "3D эскиз257"
  sketch  "3D эскиз258"
  sketch  "3D эскиз259"
  sketch  "3D эскиз260"
  sketch  "3D эскиз261"
  sketch  "3D эскиз262"
  sketch  "3D эскиз263"
  sketch  "3D эскиз264"
  sketch  "3D эскиз265"
  sketch  "3D эскиз266"
  sketch  "3D эскиз267"
  sketch  "3D эскиз268"
  sketch  "3D эскиз269"
  sketch  "3D эскиз270"
  sketch  "3D эскиз271"
  sketch  "3D эскиз272"
  sketch  "3D эскиз273"
  sketch  "3D эскиз274"
  sketch  "3D эскиз275"
  sketch  "3D эскиз276"
  sketch  "3D эскиз277"
  sketch  "3D эскиз278"
  sketch  "3D эскиз279"
  sketch  "3D эскиз280"
  sketch  "3D эскиз281"
  sketch  "3D эскиз282"
  sketch  "3D эскиз283"
  sketch  "3D эскиз284"
  sketch  "3D эскиз285"
  sketch  "3D эскиз286"
  sketch  "3D эскиз287"
  sketch  "3D эскиз288"
  sketch  "3D эскиз289"
  sketch  "3D эскиз290"
  sketch  "3D эскиз291"
  sketch  "3D эскиз292"
  sketch  "3D эскиз293"
  sketch  "3D эскиз294"
  sketch  "3D эскиз295"
  sketch  "3D эскиз296"
  sketch  "3D эскиз297"
  sketch  "3D эскиз298"
  sketch  "3D эскиз299"
  sketch  "3D эскиз300"
  sketch  "3D эскиз301"
  sketch  "3D эскиз302"
  sketch  "3D эскиз303"
  sketch  "3D эскиз304"
  sketch  "3D эскиз305"
  sketch  "3D эскиз306"
  sketch  "3D эскиз307"
  sketch  "3D эскиз308"
  sketch  "3D эскиз309"
  sketch  "3D эскиз310"
  sketch  "3D эскиз311"
  sketch  "3D эскиз312"
  sketch  "3D эскиз313"
  sketch  "3D эскиз314"
  sketch  "3D эскиз315"
  sketch  "3D эскиз316"
  sketch  "3D эскиз317"
  sketch  "3D эскиз318"
  sketch  "3D эскиз319"
  sketch  "3D эскиз320"
  sketch  "3D эскиз321"
  sketch  "3D эскиз322"
  sketch  "3D эскиз323"
  sketch  "3D эскиз324"
  sketch  "3D эскиз325"
  sketch  "3D эскиз326"
  sketch  "3D эскиз327"
  sketch  "3D эскиз328"
  sketch  "3D эскиз329"
  sketch  "3D эскиз330"
  sketch  "3D эскиз331"
  sketch  "3D эскиз332"
  sketch  "3D эскиз333"
  sketch  "3D эскиз334"
  sketch  "3D эскиз335"
  sketch  "3D эскиз336"
  sketch  "3D эскиз337"
  sketch  "3D эскиз338"
  sketch  "3D эскиз339"
  sketch  "3D эскиз340"
  sketch  "3D эскиз341"
  sketch  "3D эскиз342"
  sketch  "3D эскиз343"
  sketch  "3D эскиз344"
  sketch  "3D эскиз345"
  sketch  "3D эскиз346"
  sketch  "3D эскиз347"
  sketch  "3D эскиз348"
  sketch  "3D эскиз349"
  sketch  "3D эскиз350"
  sketch  "3D эскиз351"
  sketch  "3D эскиз352"
  sketch  "3D эскиз353"
  sketch  "3D эскиз354"
  sketch  "3D эскиз355"
  sketch  "3D эскиз356"
  sketch  "3D эскиз357"
  sketch  "3D эскиз358"
  sketch  "3D эскиз359"
  sketch  "3D эскиз360"
  sketch  "3D эскиз361"
  sketch  "3D эскиз362"
  sketch  "3D эскиз363"
  sketch  "3D эскиз364"
  sketch  "3D эскиз365"
  sketch  "3D эскиз366"
  sketch  "3D эскиз367"
  sketch  "3D эскиз368"
  sketch  "3D эскиз369"
  sketch  "3D эскиз370"
  sketch  "3D эскиз371"
  sketch  "3D эскиз372"
  sketch  "3D эскиз373"
  sketch  "3D эскиз374"
  sketch  "3D эскиз375"
  sketch  "3D эскиз376"
  sketch  "3D эскиз377"
  sketch  "3D эскиз378"
  sketch  "3D эскиз379"
  sketch  "3D эскиз380"
  sketch  "3D эскиз381"
  sketch  "3D эскиз382"
  sketch  "3D эскиз383"
  sketch  "3D эскиз384"
  sketch  "3D эскиз385"
  sketch  "3D эскиз386"
  sketch  "3D эскиз387"
  sketch  "3D эскиз388"
  sketch  "3D эскиз389"
  sketch  "3D эскиз390"
  sketch  "3D эскиз391"
  sketch  "3D эскиз392"
  sketch  "3D эскиз393"
  sketch  "3D эскиз394"
  sketch  "3D эскиз395"
  sketch  "3D эскиз396"
  sketch  "3D эскиз397"
  sketch  "3D эскиз398"
  sketch  "3D эскиз399"
  sketch  "3D эскиз400"
  sketch  "3D эскиз401"
  sketch  "3D эскиз402"
  sketch  "3D эскиз403"
  sketch  "3D эскиз404"
  sketch  "3D эскиз405"
  sketch  "3D эскиз406"
  sketch  "3D эскиз407"
  sketch  "3D эскиз408"
  sketch  "3D эскиз409"
  sketch  "3D эскиз410"
  sketch  "3D эскиз411"
  sketch  "3D эскиз412"
  sketch  "3D эскиз413"
  sketch  "3D эскиз414"
  sketch  "3D эскиз415"
  sketch  "3D эскиз416"
  sketch  "3D эскиз417"
  sketch  "3D эскиз418"
  sketch  "3D эскиз419"
  sketch  "3D эскиз420"
  sketch  "3D эскиз421"
  sketch  "3D эскиз422"
  sketch  "3D эскиз423"
  sketch  "3D эскиз424"
  sketch  "3D эскиз425"
  sketch  "3D эскиз426"
  sketch  "3D эскиз427"
  sketch  "3D эскиз428"
  sketch  "3D эскиз429"
  sketch  "3D эскиз430"
  sketch  "3D эскиз431"
  sketch  "3D эскиз432"
  sketch  "3D эскиз433"
  sketch  "3D эскиз434"
  sketch  "3D эскиз435"
  sketch  "3D эскиз436"
  sketch  "3D эскиз437"
  sketch  "3D эскиз438"
  sketch  "3D эскиз439"
  sketch  "3D эскиз440"
  sketch  "3D эскиз441"
  sketch  "3D эскиз442"
  sketch  "3D эскиз443"
  sketch  "3D эскиз444"
  sketch  "3D эскиз445"
  sketch  "3D эскиз446"
  sketch  "3D эскиз447"
  sketch  "3D эскиз448"
  sketch  "3D эскиз449"
  sketch  "3D эскиз450"
  sketch  "3D эскиз451"
  sketch  "3D эскиз452"
  sketch  "3D эскиз453"
  sketch  "3D эскиз454"
  sketch  "3D эскиз455"
  sketch  "3D эскиз456"
  sketch  "3D эскиз457"
  sketch  "3D эскиз458"
  sketch  "3D эскиз459"
  sketch  "3D эскиз460"
  sketch  "3D эскиз461"
  sketch  "3D эскиз462"
  sketch  "3D эскиз463"
  sketch  "3D эскиз464"
  sketch  "3D эскиз465"
  sketch  "3D эскиз466"
  sketch  "3D эскиз467"
  sketch  "3D эскиз468"
  sketch  "3D эскиз469"
  sketch  "3D эскиз470"
  sketch  "3D эскиз471"
  sketch  "3D эскиз472"
  sketch  "3D эскиз473"
  sketch  "3D эскиз474"
  sketch  "3D эскиз475"
  sketch  "3D эскиз476"
  sketch  "3D эскиз477"
  sketch  "3D эскиз478"
  sketch  "3D эскиз479"
  sketch  "3D эскиз480"
  sketch  "3D эскиз481"
  sketch  "3D эскиз482"
  sketch  "3D эскиз483"
  sketch  "3D эскиз484"
  sketch  "3D эскиз485"
  sketch  "3D эскиз486"
  sketch  "3D эскиз487"
  sketch  "3D эскиз488"
  sketch  "3D эскиз489"
  sketch  "3D эскиз490"
  sketch  "3D эскиз491"
  sketch  "3D эскиз492"
  sketch  "3D эскиз493"
  sketch  "3D эскиз494"
  sketch  "3D эскиз495"
  sketch  "3D эскиз496"
  sketch  "3D эскиз497"
  sketch  "3D эскиз498"
  sketch  "3D эскиз499"
  sketch  "3D эскиз500"
  sketch  "3D эскиз501"
  sketch  "3D эскиз502"
  sketch  "3D эскиз503"
  sketch  "3D эскиз504"
  sketch  "3D эскиз505"
  sketch  "3D эскиз506"
  sketch  "3D эскиз507"
  sketch  "3D эскиз508"
  sketch  "3D эскиз509"
  sketch  "3D эскиз510"
  sketch  "3D эскиз511"
  sketch  "3D эскиз512"
  sketch  "3D эскиз513"
  sketch  "3D эскиз514"
  sketch  "3D эскиз515"
  sketch  "3D эскиз516"
  sketch  "3D эскиз517"
  sketch  "3D эскиз518"
  sketch  "3D эскиз519"
  sketch  "3D эскиз520"
  sketch  "3D эскиз521"
  sketch  "3D эскиз522"
  sketch  "3D эскиз523"
  sketch  "3D эскиз524"
  sketch  "3D эскиз525"
  sketch  "3D эскиз526"
  sketch  "3D эскиз527"
  sketch  "3D эскиз528"
  sketch  "3D эскиз529"
  sketch  "3D эскиз530"
  sketch  "3D эскиз531"
  sketch  "3D эскиз532"
  sketch  "3D эскиз533"
  sketch  "3D эскиз534"
  sketch  "3D эскиз535"
  sketch  "3D эскиз536"
  sketch  "3D эскиз537"
  sketch  "3D эскиз538"
  sketch  "3D эскиз539"
  sketch  "3D эскиз540"
  sketch  "3D эскиз541"
  sketch  "3D эскиз542"
  sketch  "3D эскиз543"
  sketch  "3D эскиз544"
  sketch  "3D эскиз545"
  sketch  "3D эскиз546"
  sketch  "3D эскиз547"
  sketch  "3D эскиз548"
  sketch  "3D эскиз549"
  sketch  "3D эскиз550"
  sketch  "3D эскиз551"
  sketch  "3D эскиз552"
  sketch  "3D эскиз553"
  sketch  "3D эскиз554"
  sketch  "3D эскиз555"
  sketch  "3D эскиз556"
  sketch  "3D эскиз557"
  sketch  "3D эскиз558"
  sketch  "3D эскиз559"
  sketch  "3D эскиз560"
  sketch  "3D эскиз561"
  sketch  "3D эскиз562"
  sketch  "3D эскиз563"
  sketch  "3D эскиз564"
  sketch  "3D эскиз565"
  sketch  "3D эскиз566"
  sketch  "3D эскиз567"
  sketch  "3D эскиз568"
  sketch  "3D эскиз569"
  sketch  "3D эскиз570"
  sketch  "3D эскиз571"
  sketch  "3D эскиз572"
  sketch  "3D эскиз573"
  sketch  "3D эскиз574"
  sketch  "3D эскиз575"
  sketch  "3D эскиз576"
  sketch  "3D эскиз577"
  sketch  "3D эскиз578"
  sketch  "3D эскиз579"
  sketch  "3D эскиз580"
  sketch  "3D эскиз581"
  sketch  "3D эскиз582"
  sketch  "3D эскиз583"
  sketch  "3D эскиз584"
  sketch  "3D эскиз585"
  sketch  "3D эскиз586"
  sketch  "3D эскиз587"
  sketch  "3D эскиз588"
  sketch  "3D эскиз589"
  sketch  "3D эскиз590"
  sketch  "3D эскиз591"
  sketch  "3D эскиз592"
  sketch  "3D эскиз593"
  sketch  "3D эскиз594"
  sketch  "3D эскиз595"
  sketch  "3D эскиз596"
  sketch  "3D эскиз597"
  sketch  "3D эскиз598"
  sketch  "3D эскиз599"
  sketch  "3D эскиз600"
  sketch  "3D эскиз601"
  sketch  "3D эскиз602"
  sketch  "3D эскиз603"
  sketch  "3D эскиз604"
  sketch  "3D эскиз605"
  sketch  "3D эскиз606"
  sketch  "3D эскиз607"
  sketch  "3D эскиз608"
  sketch  "3D эскиз609"
  sketch  "3D эскиз610"
  sketch  "3D эскиз611"
  sketch  "3D эскиз612"
  sketch  "3D эскиз613"
  sketch  "3D эскиз614"
  sketch  "3D эскиз615"
  sketch  "3D эскиз616"
  sketch  "3D эскиз617"
  sketch  "3D эскиз618"
  sketch  "3D эскиз619"
  sketch  "3D эскиз620"
  sketch  "3D эскиз621"
  sketch  "3D эскиз622"
  sketch  "3D эскиз623"
  sketch  "3D эскиз624"
  sketch  "3D эскиз625"
  sketch  "3D эскиз626"
  sketch  "3D эскиз627"
  sketch  "3D эскиз628"
  sketch  "3D эскиз629"
  sketch  "3D эскиз630"
  sketch  "3D эскиз631"
  sketch  "3D эскиз632"
  sketch  "3D эскиз633"
  sketch  "3D эскиз634"
  sketch  "3D эскиз635"
  sketch  "3D эскиз636"
  sketch  "3D эскиз637"
  sketch  "3D эскиз638"
  sketch  "3D эскиз639"
  sketch  "3D эскиз640"
  sketch  "3D эскиз641"
  sketch  "3D эскиз642"
  sketch  "3D эскиз643"
  sketch  "3D эскиз644"
  sketch  "3D эскиз645"
  sketch  "3D эскиз646"
  sketch  "3D эскиз647"
  sketch  "3D эскиз648"
  sketch  "3D эскиз649"
  sketch  "3D эскиз650"
  sketch  "3D эскиз651"
  sketch  "3D эскиз652"
  sketch  "3D эскиз653"
  sketch  "3D эскиз654"
  sketch  "3D эскиз655"
  sketch  "3D эскиз656"
  sketch  "3D эскиз657"
  sketch  "3D эскиз658"
  sketch  "3D эскиз659"
  sketch  "3D эскиз660"
  sketch  "3D эскиз661"
  sketch  "3D эскиз662"
  sketch  "3D эскиз663"
  sketch  "3D эскиз664"
  sketch  "3D эскиз665"
  sketch  "3D эскиз666"
  sketch  "3D эскиз667"
  sketch  "3D эскиз668"
  sketch  "3D эскиз669"
  sketch  "3D эскиз670"
  sketch  "3D эскиз671"
  sketch  "3D эскиз672"
  sketch  "3D эскиз673"
  sketch  "3D эскиз674"
  sketch  "3D эскиз675"
  sketch  "3D эскиз676"
  sketch  "3D эскиз677"
  sketch  "3D эскиз678"
  sketch  "3D эскиз679"
  sketch  "3D эскиз680"
  sketch  "3D эскиз681"
  sketch  "3D эскиз682"
  sketch  "3D эскиз683"
  sketch  "3D эскиз684"
  sketch  "3D эскиз685"
  sketch  "3D эскиз686"
  sketch  "3D эскиз687"
  sketch  "3D эскиз688"
  sketch  "3D эскиз689"
  sketch  "3D эскиз690"
  sketch  "3D эскиз691"
  sketch  "3D эскиз692"
  sketch  "3D эскиз693"
  sketch  "3D эскиз694"
  sketch  "3D эскиз695"
  sketch  "3D эскиз696"
  sketch  "3D эскиз697"
  sketch  "3D эскиз698"
  sketch  "3D эскиз699"
  sketch  "3D эскиз700"
  sketch  "3D эскиз701"
  sketch  "3D эскиз702"
  sketch  "3D эскиз703"
  sketch  "3D эскиз704"
  sketch  "3D эскиз705"
  sketch  "3D эскиз706"
  sketch  "3D эскиз707"
  sketch  "3D эскиз708"
  sketch  "3D эскиз709"
  sketch  "3D эскиз710"
  sketch  "3D эскиз711"
  sketch  "3D эскиз712"
  sketch  "3D эскиз713"
  sketch  "3D эскиз714"
  sketch  "3D эскиз715"
  sketch  "3D эскиз716"
  sketch  "3D эскиз717"
  sketch  "3D эскиз718"
  sketch  "3D эскиз719"
  sketch  "3D эскиз720"
  sketch  "3D эскиз721"
  sketch  "3D эскиз722"
  sketch  "3D эскиз723"
  sketch  "3D эскиз724"
  sketch  "3D эскиз725"
  sketch  "3D эскиз726"
  sketch  "3D эскиз727"
  sketch  "3D эскиз728"
  sketch  "3D эскиз729"
  sketch  "3D эскиз730"
  sketch  "3D эскиз731"
  sketch  "3D эскиз732"
  sketch  "3D эскиз733"
  sketch  "3D эскиз734"
  sketch  "3D эскиз735"
  sketch  "3D эскиз736"
  sketch  "3D эскиз737"
  sketch  "3D эскиз738"
  sketch  "3D эскиз739"
  sketch  "3D эскиз740"
  sketch  "3D эскиз741"
  sketch  "3D эскиз742"
  sketch  "3D эскиз743"
  sketch  "3D эскиз744"
  sketch  "3D эскиз745"
  sketch  "3D эскиз746"
  sketch  "3D эскиз747"
  sketch  "3D эскиз748"
  sketch  "3D эскиз749"
  sketch  "3D эскиз750"
  sketch  "3D эскиз751"
  sketch  "3D эскиз752"
  sketch  "3D эскиз753"
  sketch  "3D эскиз754"
  sketch  "3D эскиз755"
  sketch  "3D эскиз756"
  sketch  "3D эскиз757"
  sketch  "3D эскиз758"
  sketch  "3D эскиз759"
  sketch  "3D эскиз760"
  sketch  "3D эскиз761"
  sketch  "3D эскиз762"
  sketch  "3D эскиз763"
  sketch  "3D эскиз764"
  sketch  "3D эскиз765"
  sketch  "3D эскиз766"
  sketch  "3D эскиз767"
  sketch  "3D эскиз768"
  sketch  "3D эскиз769"
  sketch  "3D эскиз770"
  sketch  "3D эскиз771"
  sketch  "3D эскиз772"
  sketch  "3D эскиз773"
  sketch  "3D эскиз774"
  sketch  "3D эскиз775"
  sketch  "3D эскиз776"
  sketch  "3D эскиз777"
  sketch  "3D эскиз778"
  sketch  "3D эскиз779"
  sketch  "3D эскиз780"
  sketch  "3D эскиз781"
  sketch  "3D эскиз782"
  sketch  "3D эскиз783"
  sketch  "3D эскиз784"
  sketch  "3D эскиз785"
  sketch  "3D эскиз786"
  sketch  "3D эскиз787"
  sketch  "3D эскиз788"
  sketch  "3D эскиз789"
  sketch  "3D эскиз790"
  sketch  "3D эскиз791"
  sketch  "3D эскиз792"
  sketch  "3D эскиз793"
  sketch  "3D эскиз794"
  sketch  "3D эскиз795"
  sketch  "3D эскиз796"
  sketch  "3D эскиз797"
  sketch  "3D эскиз798"
  sketch  "3D эскиз799"
  sketch  "3D эскиз800"
  sketch  "3D эскиз801"
  sketch  "3D эскиз802"
  sketch  "3D эскиз803"
  sketch  "3D эскиз804"
  sketch  "3D эскиз805"
  sketch  "3D эскиз806"
  sketch  "3D эскиз807"
  sketch  "3D эскиз808"
  sketch  "3D эскиз809"
  sketch  "3D эскиз810"
  sketch  "3D эскиз811"
  sketch  "3D эскиз812"
  sketch  "3D эскиз813"
  sketch  "3D эскиз814"
  sketch  "3D эскиз815"
  sketch  "3D эскиз816"
  sketch  "3D эскиз817"
  sketch  "3D эскиз818"
  sketch  "3D эскиз819"
  sketch  "3D эскиз820"
  sketch  "3D эскиз821"
  sketch  "3D эскиз822"
  sketch  "3D эскиз823"
  sketch  "3D эскиз824"
  sketch  "3D эскиз825"
  sketch  "3D эскиз826"
  sketch  "3D эскиз827"
  sketch  "3D эскиз828"
  sketch  "3D эскиз829"
  sketch  "3D эскиз830"
  sketch  "3D эскиз831"
  sketch  "3D эскиз832"
  sketch  "3D эскиз833"
  sketch  "3D эскиз834"
  sketch  "3D эскиз835"
  sketch  "3D эскиз836"
  sketch  "3D эскиз837"
  sketch  "3D эскиз838"
  sketch  "3D эскиз839"
  sketch  "3D эскиз840"
  sketch  "3D эскиз841"
  sketch  "3D эскиз842"
  sketch  "3D эскиз843"
  sketch  "3D эскиз844"
  sketch  "3D эскиз845"
  sketch  "3D эскиз846"
  sketch  "3D эскиз847"
  sketch  "3D эскиз848"
  sketch  "3D эскиз849"
  sketch  "3D эскиз850"
  sketch  "3D эскиз851"
  sketch  "3D эскиз852"
  sketch  "3D эскиз853"
  sketch  "3D эскиз854"
  sketch  "3D эскиз855"
  sketch  "3D эскиз856"
  sketch  "3D эскиз857"
  sketch  "3D эскиз858"
  sketch  "3D эскиз859"
  sketch  "3D эскиз860"
  sketch  "3D эскиз861"
  sketch  "3D эскиз862"
  sketch  "3D эскиз863"
  sketch  "3D эскиз864"
  sketch  "3D эскиз865"
  sketch  "3D эскиз866"
  sketch  "3D эскиз867"
  sketch  "3D эскиз868"
  sketch  "3D эскиз869"
  sketch  "3D эскиз870"
  sketch  "3D эскиз871"
  sketch  "3D эскиз872"
  sketch  "3D эскиз873"
  sketch  "3D эскиз874"
  sketch  "3D эскиз875"
  sketch  "3D эскиз876"
  sketch  "3D эскиз877"
  sketch  "3D эскиз878"
  sketch  "3D эскиз879"
  sketch  "3D эскиз880"
  sketch  "3D эскиз881"
  sketch  "3D эскиз882"
  sketch  "3D эскиз883"
  sketch  "3D эскиз884"
  sketch  "3D эскиз885"
  sketch  "3D эскиз886"
  sketch  "3D эскиз887"
  sketch  "3D эскиз888"
  sketch  "3D эскиз889"
  sketch  "3D эскиз890"
  sketch  "3D эскиз891"
  sketch  "3D эскиз892"
  sketch  "3D эскиз893"
  sketch  "3D эскиз894"
  sketch  "3D эскиз895"
  sketch  "3D эскиз896"
  sketch  "3D эскиз897"
  sketch  "3D эскиз898"
  sketch  "3D эскиз899"
  sketch  "3D эскиз900"
  sketch  "3D эскиз901"
  sketch  "3D эскиз902"
  sketch  "3D эскиз903"
  sketch  "3D эскиз904"
  sketch  "3D эскиз905"
  sketch  "3D эскиз906"
  sketch  "3D эскиз907"
  sketch  "3D эскиз908"
  sketch  "3D эскиз909"
  sketch  "3D эскиз910"
  sketch  "3D эскиз911"
  sketch  "3D эскиз912"
  sketch  "3D эскиз913"
  sketch  "3D эскиз914"
  sketch  "3D эскиз915"
  sketch  "3D эскиз916"
  sketch  "3D эскиз917"
  sketch  "3D эскиз918"
  sketch  "3D эскиз919"
  sketch  "3D эскиз920"
  sketch  "3D эскиз921"
  sketch  "3D эскиз922"
  sketch  "3D эскиз923"
  sketch  "3D эскиз924"
  sketch  "3D эскиз925"
  sketch  "3D эскиз926"
  sketch  "3D эскиз927"
  sketch  "3D эскиз928"
  sketch  "3D эскиз929"
  sketch  "3D эскиз930"
  sketch  "3D эскиз931"
  sketch  "3D эскиз932"
  sketch  "3D эскиз933"
  sketch  "3D эскиз934"
  sketch  "3D эскиз935"
  sketch  "3D эскиз936"
  sketch  "3D эскиз937"
  sketch  "3D эскиз938"
  sketch  "3D эскиз939"
  sketch  "3D эскиз940"
  sketch  "3D эскиз941"
  sketch  "3D эскиз942"
  sketch  "3D эскиз943"
  sketch  "3D эскиз944"
  sketch  "3D эскиз945"
  sketch  "3D эскиз946"
  sketch  "3D эскиз947"
  sketch  "3D эскиз948"
  sketch  "3D эскиз949"
  sketch  "3D эскиз950"
  sketch  "3D эскиз951"
  sketch  "3D эскиз952"
  sketch  "3D эскиз953"
  sketch  "3D эскиз954"
  sketch  "3D эскиз955"
  sketch  "3D эскиз956"
  sketch  "3D эскиз957"
  sketch  "3D эскиз958"
  sketch  "3D эскиз959"
  sketch  "3D эскиз960"
  sketch  "3D эскиз961"
  sketch  "3D эскиз962"
  sketch  "3D эскиз963"
  sketch  "3D эскиз964"
  sketch  "3D эскиз965"
  sketch  "3D эскиз966"
  sketch  "3D эскиз967"
  sketch  "3D эскиз968"
  sketch  "3D эскиз969"
  sketch  "3D эскиз970"
  sketch  "3D эскиз971"
  sketch  "3D эскиз972"
  sketch  "3D эскиз973"
  sketch  "3D эскиз974"
  sketch  "3D эскиз975"
  sketch  "3D эскиз976"
  sketch  "3D эскиз977"
  sketch  "3D эскиз978"
  sketch  "3D эскиз979"
  sketch  "3D эскиз980"
  sketch  "3D эскиз981"
  sketch  "3D эскиз982"
  sketch  "3D эскиз983"
  sketch  "3D эскиз984"
  sketch  "3D эскиз985"
  sketch  "3D эскиз986"
  sketch  "3D эскиз987"
  sketch  "3D эскиз988"
  sketch  "3D эскиз989"
  sketch  "3D эскиз990"
  sketch  "3D эскиз991"
  sketch  "3D эскиз992"
  sketch  "3D эскиз993"
  sketch  "3D эскиз994"
  sketch  "3D эскиз995"
  sketch  "3D эскиз996"
  sketch  "3D эскиз997"
  sketch  "3D эскиз998"
  sketch  "3D эскиз999"
  sketch  "3D эскиз1000"
  sketch  "3D эскиз1001"
  sketch  "3D эскиз1002"
  sketch  "3D эскиз1003"
  sketch  "3D эскиз1004"
  sketch  "3D эскиз1005"
  sketch  "3D эскиз1006"
  sketch  "3D эскиз1007"
  sketch  "3D эскиз1008"
  sketch  "3D эскиз1009"
  sketch  "3D эскиз1010"
  sketch  "3D эскиз1011"
  sketch  "3D эскиз1012"
  sketch  "3D эскиз1013"
  sketch  "3D эскиз1014"
  sketch  "3D эскиз1015"
  sketch  "3D эскиз1016"
  sketch  "3D эскиз1017"
  sketch  "3D эскиз1018"
  sketch  "3D эскиз1019"
  sketch  "3D эскиз1020"
  sketch  "3D эскиз1021"
  sketch  "3D эскиз1022"
  sketch  "3D эскиз1023"
  sketch  "3D эскиз1024"
  sketch  "3D эскиз1025"
  sketch  "3D эскиз1026"
  sketch  "3D эскиз1027"
  sketch  "3D эскиз1028"
  sketch  "3D эскиз1029"
  sketch  "3D эскиз1030"
  sketch  "3D эскиз1031"
  sketch  "3D эскиз1032"
  sketch  "3D эскиз1033"
  sketch  "3D эскиз1034"
  sketch  "3D эскиз1035"
  sketch  "3D эскиз1036"
  sketch  "3D эскиз1037"
  sketch  "3D эскиз1038"
  sketch  "3D эскиз1039"
  sketch  "3D эскиз1040"
  sketch  "3D эскиз1041"
  sketch  "3D эскиз1042"
  sketch  "3D эскиз1043"
  sketch  "3D эскиз1044"
  sketch  "3D эскиз1045"
  sketch  "3D эскиз1046"
  sketch  "3D эскиз1047"
  sketch  "3D эскиз1048"
  sketch  "3D эскиз1049"
  sketch  "3D эскиз1050"
  sketch  "3D эскиз1051"
  sketch  "3D эскиз1052"
  sketch  "3D эскиз1053"
  sketch  "3D эскиз1054"
  sketch  "3D эскиз1055"
  sketch  "3D эскиз1056"
  sketch  "3D эскиз1057"
  sketch  "3D эскиз1058"
  sketch  "3D эскиз1059"
  sketch  "3D эскиз1060"
  sketch  "3D эскиз1061"
  sketch  "3D эскиз1062"
  sketch  "3D эскиз1063"
  sketch  "3D эскиз1064"
  sketch  "3D эскиз1065"
  sketch  "3D эскиз1066"
  sketch  "3D эскиз1067"
  sketch  "3D эскиз1068"
  sketch  "3D эскиз1069"
  sketch  "3D эскиз1070"
  sketch  "3D эскиз1071"
  sketch  "3D эскиз1072"
  sketch  "3D эскиз1073"
  sketch  "3D эскиз1074"
  sketch  "3D эскиз1075"
  sketch  "3D эскиз1076"
  sketch  "3D эскиз1077"
  sketch  "3D эскиз1078"
  sketch  "3D эскиз1079"
  sketch  "3D эскиз1080"
  sketch  "3D эскиз1081"
  sketch  "3D эскиз1082"
  sketch  "3D эскиз1083"
  sketch  "3D эскиз1084"
  sketch  "3D эскиз1085"
  sketch  "3D эскиз1086"
  sketch  "3D эскиз1087"
  sketch  "3D эскиз1088"
  sketch  "3D эскиз1089"
  sketch  "3D эскиз1090"
  sketch  "3D эскиз1091"
  sketch  "3D эскиз1092"
  sketch  "3D эскиз1093"
  sketch  "3D эскиз1094"
  sketch  "3D эскиз1095"
  sketch  "3D эскиз1096"
  sketch  "3D эскиз1097"
  sketch  "3D эскиз1098"
  sketch  "3D эскиз1099"
  sketch  "3D эскиз1100"
  sketch  "3D эскиз1101"
  sketch  "3D эскиз1102"
  sketch  "3D эскиз1103"
  sketch  "3D эскиз1104"
  sketch  "3D эскиз1105"
  sketch  "3D эскиз1106"
  sketch  "3D эскиз1107"
  sketch  "3D эскиз1108"
  sketch  "3D эскиз1109"
  sketch  "3D эскиз1110"
  sketch  "3D эскиз1111"
  sketch  "3D эскиз1112"
  sketch  "3D эскиз1113"
  sketch  "3D эскиз1114"
  sketch  "3D эскиз1115"
  sketch  "3D эскиз1116"
  sketch  "3D эскиз1117"
  sketch  "3D эскиз1118"
  sketch  "3D эскиз1119"
  sketch  "3D эскиз1120"
  sketch  "3D эскиз1121"
  sketch  "3D эскиз1122"
  sketch  "3D эскиз1123"
  sketch  "3D эскиз1124"
  sketch  "3D эскиз1125"
  sketch  "3D эскиз1126"
  sketch  "3D эскиз1127"
  sketch  "3D эскиз1128"
  sketch  "3D эскиз1129"
  sketch  "3D эскиз1130"
  sketch  "3D эскиз1131"
  sketch  "3D эскиз1132"
  sketch  "3D эскиз1133"
  sketch  "3D эскиз1134"
  sketch  "3D эскиз1135"
  sketch  "3D эскиз1136"
  sketch  "3D эскиз1137"
  sketch  "3D эскиз1138"
  sketch  "3D эскиз1139"
  sketch  "3D эскиз1140"
  sketch  "3D эскиз1141"
  sketch  "3D эскиз1142"
  sketch  "3D эскиз1143"
  sketch  "3D эскиз1144"
  sketch  "3D эскиз1145"
  sketch  "3D эскиз1146"
  sketch  "3D эскиз1147"
  sketch  "3D эскиз1148"
  sketch  "3D эскиз1149"
  sketch  "3D эскиз1150"
  sketch  "3D эскиз1151"
  sketch  "3D эскиз1152"
  sketch  "3D эскиз1153"
  sketch  "3D эскиз1154"
  sketch  "3D эскиз1155"
  sketch  "3D эскиз1156"
  sketch  "3D эскиз1157"
  sketch  "3D эскиз1158"
  sketch  "3D эскиз1159"
  sketch  "3D эскиз1160"
  sketch  "3D эскиз1161"
  sketch  "3D эскиз1162"
  sketch  "3D эскиз1163"
  sketch  "3D эскиз1164"
  sketch  "3D эскиз1165"
  sketch  "3D эскиз1166"
  sketch  "3D эскиз1167"
  sketch  "3D эскиз1168"
  sketch  "3D эскиз1169"
  sketch  "3D эскиз1170"
  sketch  "3D эскиз1171"
  sketch  "3D эскиз1172"
  sketch  "3D эскиз1173"
  sketch  "3D эскиз1174"
  sketch  "3D эскиз1175"
  sketch  "3D эскиз1176"
  sketch  "3D эскиз1177"
  sketch  "3D эскиз1178"
  sketch  "3D эскиз1179"
  sketch  "3D эскиз1180"
  sketch  "3D эскиз1181"
  sketch  "3D эскиз1182"
  sketch  "3D эскиз1183"
  sketch  "3D эскиз1184"
  sketch  "3D эскиз1185"
  sketch  "3D эскиз1186"
  sketch  "3D эскиз1187"
  sketch  "3D эскиз1188"
  sketch  "3D эскиз1189"
  sketch  "3D эскиз1190"
  sketch  "3D эскиз1191"
  sketch  "3D эскиз1192"
  sketch  "3D эскиз1193"
  sketch  "3D эскиз1194"
  sketch  "3D эскиз1195"
  sketch  "3D эскиз1196"
  sketch  "3D эскиз1197"
  sketch  "3D эскиз1198"
  sketch  "3D эскиз1199"
  sketch  "3D эскиз1200"
  sketch  "3D эскиз1201"
  sketch  "3D эскиз1202"
  sketch  "3D эскиз1203"
  sketch  "3D эскиз1204"
  sketch  "3D эскиз1205"
  sketch  "3D эскиз1206"
  sketch  "3D эскиз1207"
  sketch  "3D эскиз1208"
  sketch  "3D эскиз1209"
  sketch  "3D эскиз1210"
  sketch  "3D эскиз1211"
  sketch  "3D эскиз1212"
  sketch  "3D эскиз1213"
  sketch  "3D эскиз1214"
  sketch  "3D эскиз1215"
  sketch  "3D эскиз1216"
  sketch  "3D эскиз1217"
  sketch  "3D эскиз1218"
  sketch  "3D эскиз1219"
  sketch  "3D эскиз1220"
  sketch  "3D эскиз1221"
  sketch  "3D эскиз1222"
  sketch  "3D эскиз1223"
  sketch  "3D эскиз1224"
  sketch  "3D эскиз1225"
  sketch  "3D эскиз1226"
  sketch  "3D эскиз1227"
  sketch  "3D эскиз1228"
  sketch  "3D эскиз1229"
  sketch  "3D эскиз1230"
  sketch  "3D эскиз1231"
  sketch  "3D эскиз1232"
  sketch  "3D эскиз1233"
  sketch  "3D эскиз1234"
  sketch  "3D эскиз1235"
  sketch  "3D эскиз1236"
  sketch  "3D эскиз1237"
  sketch  "3D эскиз1238"
  sketch  "3D эскиз1239"
  sketch  "3D эскиз1240"
  sketch  "3D эскиз1241"
  sketch  "3D эскиз1242"
  sketch  "3D эскиз1243"
  sketch  "3D эскиз1244"
  sketch  "3D эскиз1245"
  sketch  "3D эскиз1246"
  sketch  "3D эскиз1247"
  sketch  "3D эскиз1248"
  sketch  "3D эскиз1249"
  sketch  "3D эскиз1250"
  sketch  "3D эскиз1251"
  sketch  "3D эскиз1252"
  sketch  "3D эскиз1253"
  sketch  "3D эскиз1254"
  sketch  "3D эскиз1255"
  sketch  "3D эскиз1256"
  sketch  "3D эскиз1257"
  sketch  "3D эскиз1258"
  sketch  "3D эскиз1259"
  sketch  "3D эскиз1260"
  sketch  "3D эскиз1261"
  sketch  "3D эскиз1262"
  sketch  "3D эскиз1263"
  sketch  "3D эскиз1264"
  sketch  "3D эскиз1265"
  sketch  "3D эскиз1266"
  sketch  "3D эскиз1267"
  sketch  "3D эскиз1268"
  sketch  "3D эскиз1269"
  sketch  "3D эскиз1270"
  sketch  "3D эскиз1271"
  sketch  "3D эскиз1272"
  sketch  "3D эскиз1273"
  sketch  "3D эскиз1274"
  sketch  "3D эскиз1275"
  sketch  "3D эскиз1276"
  sketch  "3D эскиз1277"
  sketch  "3D эскиз1278"
  sketch  "3D эскиз1279"
  sketch  "3D эскиз1280"
  sketch  "3D эскиз1281"
  sketch  "3D эскиз1282"
  sketch  "3D эскиз1283"
  sketch  "3D эскиз1284"
  sketch  "3D эскиз1285"
  sketch  "3D эскиз1286"
  sketch  "3D эскиз1287"
  sketch  "3D эскиз1288"
  sketch  "3D эскиз1289"
  sketch  "3D эскиз1290"
  sketch  "3D эскиз1291"
  sketch  "3D эскиз1292"
  sketch  "3D эскиз1293"
  sketch  "3D эскиз1294"
  sketch  "3D эскиз1295"
  sketch  "3D эскиз1296"
  sketch  "3D эскиз1297"
  sketch  "3D эскиз1298"
  sketch  "3D эскиз1299"
  sketch  "3D эскиз1300"
  sketch  "3D эскиз1301"
  sketch  "3D эскиз1302"
  sketch  "3D эскиз1303"
  sketch  "3D эскиз1304"
  sketch  "3D эскиз1305"
  sketch  "3D эскиз1306"
  sketch  "3D эскиз1307"
  sketch  "3D эскиз1308"
  sketch  "3D эскиз1309"
  sketch  "3D эскиз1310"
  sketch  "3D эскиз1311"
  sketch  "3D эскиз1312"
  sketch  "3D эскиз1313"
  sketch  "3D эскиз1314"
  sketch  "3D эскиз1315"
  sketch  "3D эскиз1316"
  sketch  "3D эскиз1317"
  sketch  "3D эскиз1318"
  sketch  "3D эскиз1319"
  sketch  "3D эскиз1320"
  sketch  "3D эскиз1321"
  sketch  "3D эскиз1322"
  sketch  "3D эскиз1323"
  sketch  "3D эскиз1324"
  sketch  "3D эскиз1325"
  sketch  "3D эскиз1326"
  sketch  "3D эскиз1327"
  sketch  "3D эскиз1328"
  sketch  "3D эскиз1329"
  sketch  "3D эскиз1330"
  sketch  "3D эскиз1331"
  sketch  "3D эскиз1332"
  sketch  "3D эскиз1333"
  sketch  "3D эскиз1334"
  sketch  "3D эскиз1335"
  sketch  "3D эскиз1336"
  sketch  "3D эскиз1337"
  sketch  "3D эскиз1338"
  sketch  "3D эскиз1339"
  sketch  "3D эскиз1340"
  sketch  "3D эскиз1341"
  sketch  "3D эскиз1342"
  sketch  "3D эскиз1343"
  sketch  "3D эскиз1344"
  sketch  "3D эскиз1345"
  sketch  "3D эскиз1346"
  sketch  "3D эскиз1347"
  sketch  "3D эскиз1348"
  sketch  "3D эскиз1349"
  sketch  "3D эскиз1350"
  sketch  "3D эскиз1351"
  sketch  "3D эскиз1352"
  sketch  "3D эскиз1353"
  sketch  "3D эскиз1354"
  sketch  "3D эскиз1355"
  sketch  "3D эскиз1356"
  sketch  "3D эскиз1357"
  sketch  "3D эскиз1358"
  sketch  "3D эскиз1359"
  sketch  "3D эскиз1360"
  sketch  "3D эскиз1361"
  sketch  "3D эскиз1362"
  sketch  "3D эскиз1363"
  sketch  "3D эскиз1364"
  sketch  "3D эскиз1365"
  sketch  "3D эскиз1366"
  sketch  "3D эскиз1367"
  sketch  "3D эскиз1368"
  sketch  "3D эскиз1369"
  sketch  "3D эскиз1370"
  sketch  "3D эскиз1371"
  sketch  "3D эскиз1372"
  sketch  "3D эскиз1373"
  sketch  "3D эскиз1374"
  sketch  "3D эскиз1375"
  sketch  "3D эскиз1376"
  sketch  "3D эскиз1377"
  sketch  "3D эскиз1378"
  sketch  "3D эскиз1379"
  sketch  "3D эскиз1380"
  sketch  "3D эскиз1381"
  sketch  "3D эскиз1382"
  sketch  "3D эскиз1383"
  sketch  "3D эскиз1384"
  sketch  "3D эскиз1385"
  sketch  "3D эскиз1386"
  sketch  "3D эскиз1387"
  sketch  "3D эскиз1388"
  sketch  "3D эскиз1389"
  sketch  "3D эскиз1390"
  sketch  "3D эскиз1391"
  sketch  "3D эскиз1392"
  sketch  "3D эскиз1393"
  sketch  "3D эскиз1394"
  sketch  "3D эскиз1395"
  sketch  "3D эскиз1396"
  sketch  "3D эскиз1397"
  sketch  "3D эскиз1398"
  sketch  "3D эскиз1399"
  sketch  "3D эскиз1400"
  sketch  "3D эскиз1401"
  sketch  "3D эскиз1402"
  sketch  "3D эскиз1403"
  sketch  "3D эскиз1404"
  sketch  "3D эскиз1405"
  sketch  "3D эскиз1406"
  sketch  "3D эскиз1407"
  sketch  "3D эскиз1408"
  sketch  "3D эскиз1409"
  sketch  "3D эскиз1410"
  sketch  "3D эскиз1411"
  sketch  "3D эскиз1412"
  sketch  "3D эскиз1413"
  sketch  "3D эскиз1414"
  sketch  "3D эскиз1415"
  sketch  "3D эскиз1416"
  sketch  "3D эскиз1417"
  sketch  "3D эскиз1418"
  sketch  "3D эскиз1419"
  sketch  "3D эскиз1420"
  sketch  "3D эскиз1421"
  sketch  "3D эскиз1422"
  sketch  "3D эскиз1423"
  sketch  "3D эскиз1424"
  sketch  "3D эскиз1425"
  sketch  "3D эскиз1426"
  sketch  "3D эскиз1427"
  sketch  "3D эскиз1428"
  sketch  "3D эскиз1429"
  sketch  "3D эскиз1430"
  sketch  "3D эскиз1431"
  sketch  "3D эскиз1432"
  sketch  "3D эскиз1433"
  sketch  "3D эскиз1434"
  sketch  "3D эскиз1435"
  sketch  "3D эскиз1436"
  sketch  "3D эскиз1437"
  sketch  "3D эскиз1438"
  sketch  "3D эскиз1439"
  sketch  "3D эскиз1440"
  sketch  "3D эскиз1441"
  sketch  "3D эскиз1442"
  sketch  "3D эскиз1443"
  sketch  "3D эскиз1444"
  sketch  "3D эскиз1445"
  sketch  "3D эскиз1446"
  sketch  "3D эскиз1447"
  sketch  "3D эскиз1448"
  sketch  "3D эскиз1449"
  sketch  "3D эскиз1450"
  sketch  "3D эскиз1451"
  sketch  "3D эскиз1452"
  sketch  "3D эскиз1453"
  sketch  "3D эскиз1454"
  sketch  "3D эскиз1455"
  sketch  "3D эскиз1456"
  sketch  "3D эскиз1457"
  sketch  "3D эскиз1458"
  sketch  "3D эскиз1459"
  sketch  "3D эскиз1460"
  sketch  "3D эскиз1461"
  sketch  "3D эскиз1462"
  sketch  "3D эскиз1463"
  sketch  "3D эскиз1464"
  sketch  "3D эскиз1465"
  sketch  "3D эскиз1466"
  sketch  "3D эскиз1467"
  sketch  "3D эскиз1468"
  sketch  "3D эскиз1469"
  sketch  "3D эскиз1470"
  sketch  "3D эскиз1471"
  sketch  "3D эскиз1472"
  sketch  "3D эскиз1473"
  sketch  "3D эскиз1474"
  sketch  "3D эскиз1475"
  sketch  "3D эскиз1476"
  sketch  "3D эскиз1477"
  sketch  "3D эскиз1478"
  sketch  "3D эскиз1479"
  sketch  "3D эскиз1480"
  sketch  "3D эскиз1481"
  sketch  "3D эскиз1482"
  sketch  "3D эскиз1483"
  sketch  "3D эскиз1484"
  sketch  "3D эскиз1485"
  sketch  "3D эскиз1486"
  sketch  "3D эскиз1487"
  sketch  "3D эскиз1488"
  sketch  "3D эскиз1489"
  sketch  "3D эскиз1490"
  sketch  "3D эскиз1491"
  sketch  "3D эскиз1492"
  sketch  "3D эскиз1493"
  sketch  "3D эскиз1494"
  sketch  "3D эскиз1495"
  sketch  "3D эскиз1496"
  sketch  "3D эскиз1497"
  sketch  "3D эскиз1498"
  sketch  "3D эскиз1499"
  sketch  "3D эскиз1500"
  sketch  "3D эскиз1501"
  sketch  "3D эскиз1502"
  sketch  "3D эскиз1503"
  sketch  "3D эскиз1504"
  sketch  "3D эскиз1505"
  sketch  "3D эскиз1506"
  sketch  "3D эскиз1507"
  sketch  "3D эскиз1508"
  sketch  "3D эскиз1509"
  sketch  "3D эскиз1510"
  sketch  "3D эскиз1511"
  sketch  "3D эскиз1512"
  sketch  "3D эскиз1513"
  sketch  "3D эскиз1514"
  sketch  "3D эскиз1515"
  sketch  "3D эскиз1516"
  sketch  "3D эскиз1517"
  sketch  "3D эскиз1518"
  sketch  "3D эскиз1519"
  sketch  "3D эскиз1520"
  sketch  "3D эскиз1521"
  sketch  "3D эскиз1522"
  sketch  "3D эскиз1523"
  sketch  "3D эскиз1524"
  sketch  "3D эскиз1525"
  sketch  "3D эскиз1526"
  sketch  "3D эскиз1527"
  sketch  "3D эскиз1528"
  sketch  "3D эскиз1529"
  sketch  "3D эскиз1530"
  sketch  "3D эскиз1531"
  sketch  "3D эскиз1532"
  sketch  "3D эскиз1533"
  sketch  "3D эскиз1534"
  sketch  "3D эскиз1535"
  sketch  "3D эскиз1536"
  sketch  "3D эскиз1537"
  sketch  "3D эскиз1538"
  sketch  "3D эскиз1539"
  sketch  "3D эскиз1540"
  sketch  "3D эскиз1541"
  sketch  "3D эскиз1542"
  sketch  "3D эскиз1543"
  sketch  "3D эскиз1544"
  sketch  "3D эскиз1545"
  sketch  "3D эскиз1546"
  sketch  "3D эскиз1547"
  sketch  "3D эскиз1548"
  sketch  "3D эскиз1549"
  sketch  "3D эскиз1550"
  sketch  "3D эскиз1551"
  sketch  "3D эскиз1552"
  sketch  "3D эскиз1553"
  sketch  "3D эскиз1554"
  sketch  "3D эскиз1555"
  sketch  "3D эскиз1556"
  sketch  "3D эскиз1557"
  sketch  "3D эскиз1558"
  sketch  "3D эскиз1559"
  sketch  "3D эскиз1560"
  sketch  "3D эскиз1561"
  sketch  "3D эскиз1562"
  sketch  "3D эскиз1563"
  sketch  "3D эскиз1564"
  sketch  "3D эскиз1565"
  sketch  "3D эскиз1566"
  sketch  "3D эскиз1567"
  sketch  "3D эскиз1568"
  sketch  "3D эскиз1569"
  sketch  "3D эскиз1570"
  sketch  "3D эскиз1571"
  sketch  "3D эскиз1572"
  sketch  "3D эскиз1573"
  sketch  "3D эскиз1574"
  sketch  "3D эскиз1575"
  sketch  "3D эскиз1576"
  sketch  "3D эскиз1577"
  sketch  "3D эскиз1578"
  sketch  "3D эскиз1579"
  sketch  "3D эскиз1580"
  sketch  "3D эскиз1581"
  sketch  "3D эскиз1582"
  sketch  "3D эскиз1583"
  sketch  "3D эскиз1584"
  sketch  "3D эскиз1585"
  sketch  "3D эскиз1586"
  sketch  "3D эскиз1587"
  sketch  "3D эскиз1588"
  sketch  "3D эскиз1589"
  sketch  "3D эскиз1590"
  sketch  "3D эскиз1591"
  sketch  "3D эскиз1592"
  sketch  "3D эскиз1593"
  sketch  "3D эскиз1594"
  sketch  "3D эскиз1595"
  sketch  "3D эскиз1596"
  sketch  "3D эскиз1597"
  sketch  "3D эскиз1598"
  sketch  "3D эскиз1599"
  sketch  "3D эскиз1600"
  sketch  "3D эскиз1601"
  sketch  "3D эскиз1602"
  sketch  "3D эскиз1603"
  sketch  "3D эскиз1604"
  sketch  "3D эскиз1605"
  sketch  "3D эскиз1606"
  sketch  "3D эскиз1607"
  sketch  "3D эскиз1608"
  sketch  "3D эскиз1609"
  sketch  "3D эскиз1610"
  sketch  "3D эскиз1611"
  sketch  "3D эскиз1612"
  sketch  "3D эскиз1613"
  sketch  "3D эскиз1614"
  sketch  "3D эскиз1615"
  sketch  "3D эскиз1616"
  sketch  "3D эскиз1617"
  sketch  "3D эскиз1618"
  sketch  "3D эскиз1619"
  sketch  "3D эскиз1620"
  sketch  "3D эскиз1621"
  sketch  "3D эскиз1622"
  sketch  "3D эскиз1623"
  sketch  "3D эскиз1624"
  sketch  "3D эскиз1625"
  sketch  "3D эскиз1626"
  sketch  "3D эскиз1627"
  sketch  "3D эскиз1628"
  sketch  "3D эскиз1629"
  sketch  "3D эскиз1630"
  sketch  "3D эскиз1631"
  sketch  "3D эскиз1632"
  sketch  "3D эскиз1633"
  sketch  "3D эскиз1634"
  sketch  "3D эскиз1635"
  sketch  "3D эскиз1636"
  sketch  "3D эскиз1637"
  sketch  "3D эскиз1638"
  sketch  "3D эскиз1639"
  sketch  "3D эскиз1640"
  sketch  "3D эскиз1641"
  sketch  "3D эскиз1642"
  sketch  "3D эскиз1643"
  sketch  "3D эскиз1644"
  sketch  "3D эскиз1645"
  sketch  "3D эскиз1646"
  sketch  "3D эскиз1647"
  sketch  "3D эскиз1648"
  sketch  "3D эскиз1649"
  sketch  "3D эскиз1650"
  sketch  "3D эскиз1651"
  sketch  "3D эскиз1652"
  sketch  "3D эскиз1653"
  sketch  "3D эскиз1654"
  sketch  "3D эскиз1655"
  sketch  "3D эскиз1656"
  sketch  "3D эскиз1657"
  sketch  "3D эскиз1658"
  sketch  "3D эскиз1659"
  sketch  "3D эскиз1660"
  sketch  "3D эскиз1661"
  sketch  "3D эскиз1662"
  sketch  "3D эскиз1663"
  sketch  "3D эскиз1664"
  sketch  "3D эскиз1665"
  sketch  "3D эскиз1666"
  sketch  "3D эскиз1667"
  sketch  "3D эскиз1668"
  sketch  "3D эскиз1669"
  sketch  "3D эскиз1670"
  sketch  "3D эскиз1671"
  sketch  "3D эскиз1672"
  sketch  "3D эскиз1673"
  sketch  "3D эскиз1674"
  sketch  "3D эскиз1675"
  sketch  "3D эскиз1676"
  sketch  "3D эскиз1677"
  sketch  "3D эскиз1678"
  sketch  "3D эскиз1679"
  sketch  "3D эскиз1680"
  sketch  "3D эскиз1681"
  sketch  "3D эскиз1682"
  sketch  "3D эскиз1683"
  sketch  "3D эскиз1684"
  sketch  "3D эскиз1685"
  sketch  "3D эскиз1686"
  sketch  "3D эскиз1687"
  sketch  "3D эскиз1688"
  sketch  "3D эскиз1689"
  sketch  "3D эскиз1690"
  sketch  "3D эскиз1691"
  sketch  "3D эскиз1692"
  sketch  "3D эскиз1693"
  sketch  "3D эскиз1694"
  sketch  "3D эскиз1695"
  sketch  "3D эскиз1696"
  sketch  "3D эскиз1697"
  sketch  "3D эскиз1698"
  sketch  "3D эскиз1699"
  sketch  "3D эскиз1700"
  sketch  "3D эскиз1701"
  sketch  "3D эскиз1702"
  sketch  "3D эскиз1703"
  sketch  "3D эскиз1704"
  sketch  "3D эскиз1705"
  sketch  "3D эскиз1706"
  sketch  "3D эскиз1707"
  sketch  "3D эскиз1708"
  sketch  "3D эскиз1709"
  sketch  "3D эскиз1710"
  sketch  "3D эскиз1711"
  sketch  "3D эскиз1712"
  sketch  "3D эскиз1713"
  sketch  "3D эскиз1714"
  sketch  "3D эскиз1715"
  sketch  "3D эскиз1716"
  sketch  "3D эскиз1717"
  sketch  "3D эскиз1718"
  sketch  "3D эскиз1719"
  sketch  "3D эскиз1720"
  sketch  "3D эскиз1721"
  sketch  "3D эскиз1722"
  sketch  "3D эскиз1723"
  sketch  "3D эскиз1724"
  sketch  "3D эскиз1725"
  sketch  "3D эскиз1726"
  sketch  "3D эскиз1727"
  sketch  "3D эскиз1728"
  sketch  "3D эскиз1729"
  sketch  "3D эскиз1730"
  sketch  "3D эскиз1731"
  sketch  "3D эскиз1732"
  sketch  "3D эскиз1733"
  sketch  "3D эскиз1734"
  sketch  "3D эскиз1735"
  sketch  "3D эскиз1736"
  sketch  "3D эскиз1737"
  sketch  "3D эскиз1738"
  sketch  "3D эскиз1739"
  sketch  "3D эскиз1740"
  sketch  "3D эскиз1741"
  sketch  "3D эскиз1742"
  sketch  "3D эскиз1743"
  sketch  "3D эскиз1744"
  sketch  "3D эскиз1745"
  sketch  "3D эскиз1746"
  sketch  "3D эскиз1747"
  sketch  "3D эскиз1748"
  sketch  "3D эскиз1749"
  sketch  "3D эскиз1750"
  sketch  "3D эскиз1751"
  sketch  "3D эскиз1752"
  sketch  "3D эскиз1753"
  sketch  "3D эскиз1754"
  sketch  "3D эскиз1755"
  sketch  "3D эскиз1756"
  sketch  "3D эскиз1757"
  sketch  "3D эскиз1758"
  sketch  "3D эскиз1759"
  sketch  "3D эскиз1760"
  sketch  "3D эскиз1761"
  sketch  "3D эскиз1762"
  sketch  "3D эскиз1763"
  sketch  "3D эскиз1764"
  sketch  "3D эскиз1765"
  sketch  "3D эскиз1766"
  sketch  "3D эскиз1767"
  sketch  "3D эскиз1768"
  sketch  "3D эскиз1769"
  sketch  "3D эскиз1770"
  sketch  "3D эскиз1771"
  sketch  "3D эскиз1772"
  sketch  "3D эскиз1773"
  sketch  "3D эскиз1774"
  sketch  "3D эскиз1775"
  sketch  "3D эскиз1776"
  sketch  "3D эскиз1777"
  sketch  "3D эскиз1778"
  sketch  "3D эскиз1779"
  sketch  "3D эскиз1780"
  sketch  "3D эскиз1781"
  sketch  "3D эскиз1782"
  sketch  "3D эскиз1783"
  sketch  "3D эскиз1784"
  sketch  "3D эскиз1785"
  sketch  "3D эскиз1786"
  sketch  "3D эскиз1787"
  sketch  "3D эскиз1788"
  sketch  "3D эскиз1789"
  sketch  "3D эскиз1790"
  sketch  "3D эскиз1791"
  sketch  "3D эскиз1792"
  sketch  "3D эскиз1793"
  sketch  "3D эскиз1794"
  sketch  "3D эскиз1795"
  sketch  "3D эскиз1796"
  sketch  "3D эскиз1797"
  sketch  "3D эскиз1798"
  sketch  "3D эскиз1799"
  sketch  "3D эскиз1800"
  sketch  "3D эскиз1801"
  sketch  "3D эскиз1802"
  sketch  "3D эскиз1803"
  sketch  "3D эскиз1804"
  sketch  "3D эскиз1805"
  sketch  "3D эскиз1806"
  sketch  "3D эскиз1807"
  sketch  "3D эскиз1808"
  sketch  "3D эскиз1809"
  sketch  "3D эскиз1810"
  sketch  "3D эскиз1811"
  sketch  "3D эскиз1812"
  sketch  "3D эскиз1813"
  sketch  "3D эскиз1814"
  sketch  "3D эскиз1815"
  sketch  "3D эскиз1816"
  sketch  "3D эскиз1817"
  sketch  "3D эскиз1818"
  sketch  "3D эскиз1819"
  sketch  "3D эскиз1820"
  sketch  "3D эскиз1821"
  sketch  "3D эскиз1822"
  sketch  "3D эскиз1823"
  sketch  "3D эскиз1824"
  sketch  "3D эскиз1825"
  sketch  "3D эскиз1826"
  sketch  "3D эскиз1827"
  sketch  "3D эскиз1828"
  sketch  "3D эскиз1829"
  sketch  "3D эскиз1830"
  sketch  "3D эскиз1831"
  sketch  "3D эскиз1832"
  sketch  "3D эскиз1833"
  sketch  "3D эскиз1834"
  sketch  "3D эскиз1835"
  sketch  "3D эскиз1836"
  sketch  "3D эскиз1837"
  sketch  "3D эскиз1838"
  sketch  "3D эскиз1839"
  sketch  "3D эскиз1840"
  sketch  "3D эскиз1841"
  sketch  "3D эскиз1842"
  sketch  "3D эскиз1843"
  sketch  "3D эскиз1844"
  sketch  "3D эскиз1845"
  sketch  "3D эскиз1846"
  sketch  "3D эскиз1847"
  sketch  "3D эскиз1848"
  sketch  "3D эскиз1849"
  sketch  "3D эскиз1850"
  sketch  "3D эскиз1851"
  sketch  "3D эскиз1852"
  sketch  "3D эскиз1853"
  sketch  "3D эскиз1854"
  sketch  "3D эскиз1855"
  sketch  "3D эскиз1856"
  sketch  "3D эскиз1857"
  sketch  "3D эскиз1858"
  sketch  "3D эскиз1859"
  sketch  "3D эскиз1860"
  sketch  "3D эскиз1861"
  sketch  "3D эскиз1862"
  sketch  "3D эскиз1863"
  sketch  "3D эскиз1864"
  sketch  "3D эскиз1865"
  sketch  "3D эскиз1866"
  sketch  "3D эскиз1867"
  sketch  "3D эскиз1868"
  sketch  "3D эскиз1869"
  sketch  "3D эскиз1870"
  sketch  "3D эскиз1871"
  sketch  "3D эскиз1872"
  sketch  "3D эскиз1873"
  sketch  "3D эскиз1874"
  sketch  "3D эскиз1875"
  sketch  "3D эскиз1876"
  sketch  "3D эскиз1877"
  sketch  "3D эскиз1878"
  sketch  "3D эскиз1879"
  sketch  "3D эскиз1880"
  sketch  "3D эскиз1881"
  sketch  "3D эскиз1882"
  sketch  "3D эскиз1883"
  sketch  "3D эскиз1884"
  sketch  "3D эскиз1885"
  sketch  "3D эскиз1886"
  sketch  "3D эскиз1887"
  sketch  "3D эскиз1888"
  sketch  "3D эскиз1889"
  sketch  "3D эскиз1890"
  sketch  "3D эскиз1891"
  sketch  "3D эскиз1892"
  sketch  "3D эскиз1893"
  sketch  "3D эскиз1894"
  sketch  "3D эскиз1895"
  sketch  "3D эскиз1896"
  sketch  "3D эскиз1897"
  sketch  "3D эскиз1898"
  sketch  "3D эскиз1899"
  sketch  "3D эскиз1900"
  sketch  "3D эскиз1901"
  sketch  "3D эскиз1902"
  sketch  "3D эскиз1903"
  sketch  "3D эскиз1904"
  sketch  "3D эскиз1905"
  sketch  "3D эскиз1906"
  sketch  "3D эскиз1907"
  sketch  "3D эскиз1908"
  sketch  "3D эскиз1909"
  sketch  "3D эскиз1910"
  sketch  "3D эскиз1911"
  sketch  "3D эскиз1912"
  sketch  "3D эскиз1913"
  sketch  "3D эскиз1914"
  sketch  "3D эскиз1915"
  sketch  "3D эскиз1916"
  sketch  "3D эскиз1917"
  sketch  "3D эскиз1918"
  sketch  "3D эскиз1919"
  sketch  "3D эскиз1920"
  sketch  "3D эскиз1921"
  sketch  "3D эскиз1922"
  sketch  "3D эскиз1923"
  sketch  "3D эскиз1924"
  sketch  "3D эскиз1925"
  sketch  "3D эскиз1926"
  sketch  "3D эскиз1927"
  sketch  "3D эскиз1928"
  sketch  "3D эскиз1929"
  sketch  "3D эскиз1930"
  sketch  "3D эскиз1931"
  sketch  "3D эскиз1932"
  sketch  "3D эскиз1933"
  sketch  "3D эскиз1934"
  sketch  "3D эскиз1935"
  sketch  "3D эскиз1936"
  sketch  "3D эскиз1937"
  sketch  "3D эскиз1938"
  sketch  "3D эскиз1939"
  sketch  "3D эскиз1940"
  sketch  "3D эскиз1941"
  sketch  "3D эскиз1942"
  sketch  "3D эскиз1943"
  sketch  "3D эскиз1944"
  sketch  "3D эскиз1945"
  sketch  "3D эскиз1946"
  sketch  "3D эскиз1947"
  sketch  "3D эскиз1948"
  sketch  "3D эскиз1949"
  sketch  "3D эскиз1950"
  sketch  "3D эскиз1951"
  sketch  "3D эскиз1952"
  sketch  "3D эскиз1953"
  sketch  "3D эскиз1954"
  sketch  "3D эскиз1955"
  sketch  "3D эскиз1956"
  sketch  "3D эскиз1957"
  sketch  "3D эскиз1958"
  sketch  "3D эскиз1959"
  sketch  "3D эскиз1960"
  sketch  "3D эскиз1961"
  sketch  "3D эскиз1962"
  sketch  "3D эскиз1963"
  sketch  "3D эскиз1964"
  sketch  "3D эскиз1965"
  sketch  "3D эскиз1966"
  sketch  "3D эскиз1967"
  sketch  "3D эскиз1968"
  sketch  "3D эскиз1969"
  sketch  "3D эскиз1970"
  sketch  "3D эскиз1971"
  sketch  "3D эскиз1972"
  sketch  "3D эскиз1973"
  sketch  "3D эскиз1974"
  sketch  "3D эскиз1975"
  sketch  "3D эскиз1976"
  sketch  "3D эскиз1977"
  sketch  "3D эскиз1978"
  sketch  "3D эскиз1979"
  sketch  "3D эскиз1980"
  sketch  "3D эскиз1981"
  sketch  "3D эскиз1982"
  sketch  "3D эскиз1983"
  sketch  "3D эскиз1984"
  sketch  "3D эскиз1985"
  sketch  "3D эскиз1986"
  sketch  "3D эскиз1987"
  sketch  "3D эскиз1988"
  sketch  "3D эскиз1989"
  sketch  "3D эскиз1990"
  sketch  "3D эскиз1991"
  sketch  "3D эскиз1992"
  sketch  "3D эскиз1993"
  sketch  "3D эскиз1994"
  sketch  "3D эскиз1995"
  sketch  "3D эскиз1996"
  sketch  "3D эскиз1997"
  sketch  "3D эскиз1998"
  sketch  "3D эскиз1999"
  sketch  "3D эскиз2000"
  sketch  "3D эскиз2001"
  sketch  "3D эскиз2002"
  sketch  "3D эскиз2003"
  sketch  "3D эскиз2004"
  sketch  "3D эскиз2005"
  sketch  "3D эскиз2006"
  sketch  "3D эскиз2007"
  sketch  "3D эскиз2008"
  sketch  "3D эскиз2009"
  sketch  "3D эскиз2010"
  sketch  "3D эскиз2011"
  sketch  "3D эскиз2012"
  sketch  "3D эскиз2013"
  sketch  "3D эскиз2014"
  sketch  "3D эскиз2015"
  sketch  "3D эскиз2016"
  sketch  "3D эскиз2017"
  sketch  "3D эскиз2018"
  sketch  "3D эскиз2019"
  sketch  "3D эскиз2020"
  sketch  "3D эскиз2021"
  sketch  "3D эскиз2022"
  sketch  "3D эскиз2023"
  sketch  "3D эскиз2024"
  sketch  "3D эскиз2025"
  sketch  "3D эскиз2026"
  sketch  "3D эскиз2027"
  sketch  "3D эскиз2028"
  sketch  "3D эскиз2029"
  sketch  "3D эскиз2030"
  sketch  "3D эскиз2031"
  sketch  "3D эскиз2032"
  sketch  "3D эскиз2033"
  sketch  "3D эскиз2034"
  sketch  "3D эскиз2035"
  sketch  "3D эскиз2036"
  sketch  "3D эскиз2037"
  sketch  "3D эскиз2038"
  sketch  "3D эскиз2039"
  sketch  "3D эскиз2040"
  sketch  "3D эскиз2041"
  sketch  "3D эскиз2042"
  sketch  "3D эскиз2043"
  sketch  "3D эскиз2044"
  sketch  "3D эскиз2045"
  sketch  "3D эскиз2046"
  sketch  "3D эскиз2047"
  sketch  "3D эскиз2048"
  sketch  "3D эскиз2049"
  sketch  "3D эскиз2050"
  sketch  "3D эскиз2051"
  sketch  "3D эскиз2052"
  sketch  "3D эскиз2053"
  sketch  "3D эскиз2054"
  sketch  "3D эскиз2055"
  sketch  "3D эскиз2056"
  sketch  "3D эскиз2057"
  sketch  "3D эскиз2058"
  sketch  "3D эскиз2059"
  sketch  "3D эскиз2060"
  sketch  "3D эскиз2061"
  sketch  "3D эскиз2062"
  sketch  "3D эскиз2063"
  sketch  "3D эскиз2064"
  sketch  "3D эскиз2065"
  sketch  "3D эскиз2066"
  sketch  "3D эскиз2067"
  sketch  "3D эскиз2068"
  sketch  "3D эскиз2069"
  sketch  "3D эскиз2070"
  sketch  "3D эскиз2071"
  sketch  "3D эскиз2072"
  sketch  "3D эскиз2073"
  sketch  "3D эскиз2074"
  sketch  "3D эскиз2075"
  sketch  "3D эскиз2076"
  sketch  "3D эскиз2077"
  sketch  "3D эскиз2078"
  sketch  "3D эскиз2079"
  sketch  "3D эскиз2080"
  sketch  "3D эскиз2081"
  sketch  "3D эскиз2082"
  sketch  "3D эскиз2083"
  sketch  "3D эскиз2084"
  sketch  "3D эскиз2085"
  sketch  "3D эскиз2086"
  sketch  "3D эскиз2087"
  sketch  "3D эскиз2088"
  sketch  "3D эскиз2089"
  sketch  "3D эскиз2090"
  sketch  "3D эскиз2091"
  sketch  "3D эскиз2092"
  sketch  "3D эскиз2093"
  sketch  "3D эскиз2094"
  sketch  "3D эскиз2095"
  sketch  "3D эскиз2096"
  sketch  "3D эскиз2097"
  sketch  "3D эскиз2098"
  sketch  "3D эскиз2099"
  sketch  "3D эскиз2100"
  sketch  "3D эскиз2101"
  sketch  "3D эскиз2102"
  sketch  "3D эскиз2103"
  sketch  "3D эскиз2104"
  sketch  "3D эскиз2105"
  sketch  "3D эскиз2106"
  sketch  "3D эскиз2107"
  sketch  "3D эскиз2108"
  sketch  "3D эскиз2109"
  sketch  "3D эскиз2110"
  sketch  "3D эскиз2111"
  sketch  "3D эскиз2112"
  sketch  "3D эскиз2113"
  sketch  "3D эскиз2114"
  sketch  "3D эскиз2115"
  sketch  "3D эскиз2116"
  sketch  "3D эскиз2117"
  sketch  "3D эскиз2118"
  sketch  "3D эскиз2119"
  sketch  "3D эскиз2120"
  sketch  "3D эскиз2121"
  sketch  "3D эскиз2122"
  sketch  "3D эскиз2123"
  sketch  "3D эскиз2124"
  sketch  "3D эскиз2125"
  sketch  "3D эскиз2126"
  sketch  "3D эскиз2127"
  sketch  "3D эскиз2128"
  sketch  "3D эскиз2129"
  sketch  "3D эскиз2130"
  sketch  "3D эскиз2131"
  sketch  "3D эскиз2132"
  sketch  "3D эскиз2133"
  sketch  "3D эскиз2134"
  sketch  "3D эскиз2135"
  sketch  "3D эскиз2136"
  sketch  "3D эскиз2137"
  sketch  "3D эскиз2138"
  sketch  "3D эскиз2139"
  sketch  "3D эскиз2140"
  sketch  "3D эскиз2141"
  sketch  "3D эскиз2142"
  sketch  "3D эскиз2143"
  sketch  "3D эскиз2144"
  sketch  "3D эскиз2145"
  sketch  "3D эскиз2146"
  sketch  "3D эскиз2147"
  sketch  "3D эскиз2148"
  sketch  "3D эскиз2149"
  sketch  "3D эскиз2150"
  sketch  "3D эскиз2151"
  sketch  "3D эскиз2152"
  sketch  "3D эскиз2153"
  sketch  "3D эскиз2154"
  sketch  "3D эскиз2155"
  sketch  "3D эскиз2156"
  sketch  "3D эскиз2157"
  sketch  "3D эскиз2158"
  sketch  "3D эскиз2159"
  sketch  "3D эскиз2160"
  sketch  "3D эскиз2161"
  sketch  "3D эскиз2162"
  sketch  "3D эскиз2163"
  sketch  "3D эскиз2164"
  sketch  "3D эскиз2165"
  sketch  "3D эскиз2166"
  sketch  "3D эскиз2167"
  sketch  "3D эскиз2168"
  sketch  "3D эскиз2169"
  sketch  "3D эскиз2170"
  sketch  "3D эскиз2171"
  sketch  "3D эскиз2172"
  sketch  "3D эскиз2173"
  sketch  "3D эскиз2174"
  sketch  "3D эскиз2175"
  sketch  "3D эскиз2176"
  sketch  "3D эскиз2177"
  sketch  "3D эскиз2178"
  sketch  "3D эскиз2179"
  sketch  "3D эскиз2180"
  sketch  "3D эскиз2181"
  sketch  "3D эскиз2182"
  sketch  "3D эскиз2183"
  sketch  "3D эскиз2184"
  sketch  "3D эскиз2185"
  sketch  "3D эскиз2186"
  sketch  "3D эскиз2187"
  sketch  "3D эскиз2188"
  sketch  "3D эскиз2189"
  sketch  "3D эскиз2190"
  sketch  "3D эскиз2191"
  sketch  "3D эскиз2192"
  sketch  "3D эскиз2193"
  sketch  "3D эскиз2194"
  sketch  "3D эскиз2195"
  sketch  "3D эскиз2196"
  sketch  "3D эскиз2197"
  sketch  "3D эскиз2198"
  sketch  "3D эскиз2199"
  sketch  "3D эскиз2200"
  sketch  "3D эскиз2201"
  sketch  "3D эскиз2202"
  sketch  "3D эскиз2203"
  sketch  "3D эскиз2204"
  sketch  "3D эскиз2205"
  sketch  "3D эскиз2206"
  sketch  "3D эскиз2207"
  sketch  "3D эскиз2208"
  sketch  "3D эскиз2209"
  sketch  "3D эскиз2210"
  sketch  "3D эскиз2211"
  sketch  "3D эскиз2212"
  sketch  "3D эскиз2213"
  sketch  "3D эскиз2214"
  sketch  "3D эскиз2215"
  sketch  "3D эскиз2216"
  sketch  "3D эскиз2217"
  sketch  "3D эскиз2218"
  sketch  "3D эскиз2219"
  sketch  "3D эскиз2220"
  sketch  "3D эскиз2221"
  sketch  "3D эскиз2222"
  sketch  "3D эскиз2223"
  sketch  "3D эскиз2224"
  sketch  "3D эскиз2225"
  sketch  "3D эскиз2226"
  sketch  "3D эскиз2227"
  sketch  "3D эскиз2228"
  sketch  "3D эскиз2229"
  sketch  "3D эскиз2230"
  sketch  "3D эскиз2231"
  sketch  "3D эскиз2232"
  sketch  "3D эскиз2233"
  sketch  "3D эскиз2234"
  sketch  "3D эскиз2235"
  sketch  "3D эскиз2236"
  sketch  "3D эскиз2237"
  sketch  "3D эскиз2238"
  sketch  "3D эскиз2239"
  sketch  "3D эскиз2240"
  sketch  "3D эскиз2241"
  sketch  "3D эскиз2242"
  sketch  "3D эскиз2243"
  sketch  "3D эскиз2244"
  sketch  "3D эскиз2245"
  sketch  "3D эскиз2246"
  sketch  "3D эскиз2247"
  sketch  "3D эскиз2248"
  sketch  "3D эскиз2249"
  sketch  "3D эскиз2250"
  sketch  "3D эскиз2251"
  sketch  "3D эскиз2252"
  sketch  "3D эскиз2253"
  sketch  "3D эскиз2254"
  sketch  "3D эскиз2255"
  sketch  "3D эскиз2256"
  sketch  "3D эскиз2257"
  sketch  "3D эскиз2258"
  sketch  "3D эскиз2259"
  sketch  "3D эскиз2260"
  sketch  "3D эскиз2261"
  sketch  "3D эскиз2262"
  sketch  "3D эскиз2263"
  sketch  "3D эскиз2264"
  sketch  "3D эскиз2265"
  sketch  "3D эскиз2266"
  sketch  "3D эскиз2267"
  sketch  "3D эскиз2268"
  sketch  "3D эскиз2269"
  sketch  "3D эскиз2270"
  sketch  "3D эскиз2271"
  sketch  "3D эскиз2272"
  sketch  "3D эскиз2273"
  sketch  "3D эскиз2274"
  sketch  "3D эскиз2275"
  sketch  "3D эскиз2276"
  sketch  "3D эскиз2277"
  sketch  "3D эскиз2278"
  sketch  "3D эскиз2279"
  sketch  "3D эскиз2280"
  sketch  "3D эскиз2281"
  sketch  "3D эскиз2282"
  sketch  "3D эскиз2283"
  sketch  "3D эскиз2284"
  sketch  "3D эскиз2285"
  sketch  "3D эскиз2286"
  sketch  "3D эскиз2287"
  sketch  "3D эскиз2288"
  sketch  "3D эскиз2289"
  sketch  "3D эскиз2290"
  sketch  "3D эскиз2291"
  sketch  "3D эскиз2292"
  sketch  "3D эскиз2293"
  sketch  "3D эскиз2294"
  sketch  "3D эскиз2295"
  sketch  "3D эскиз2296"
  sketch  "3D эскиз2297"
  sketch  "3D эскиз2298"
  sketch  "3D эскиз2299"
  sketch  "3D эскиз2300"
  sketch  "3D эскиз2301"
  sketch  "3D эскиз2302"
  sketch  "3D эскиз2303"
  sketch  "3D эскиз2304"
  sketch  "3D эскиз2305"
  sketch  "3D эскиз2306"
  sketch  "3D эскиз2307"
  sketch  "3D эскиз2308"
  sketch  "3D эскиз2309"
  sketch  "3D эскиз2310"
  sketch  "3D эскиз2311"
  sketch  "3D эскиз2312"
  sketch  "3D эскиз2313"
  sketch  "3D эскиз2314"
  sketch  "3D эскиз2315"
  sketch  "3D эскиз2316"
  sketch  "3D эскиз2317"
  sketch  "3D эскиз2318"
  sketch  "3D эскиз2319"
  sketch  "3D эскиз2320"
  sketch  "3D эскиз2321"
  sketch  "3D эскиз2322"
  sketch  "3D эскиз2323"
  sketch  "3D эскиз2324"
  sketch  "3D эскиз2325"
  sketch  "3D эскиз2326"
  sketch  "3D эскиз2327"
  sketch  "3D эскиз2328"
  sketch  "3D эскиз2329"
  sketch  "3D эскиз2330"
  sketch  "3D эскиз2331"
  sketch  "3D эскиз2332"
  sketch  "3D эскиз2333"
  sketch  "3D эскиз2334"
  sketch  "3D эскиз2335"
  sketch  "3D эскиз2336"
  sketch  "3D эскиз2337"
  sketch  "3D эскиз2338"
  sketch  "3D эскиз2339"
  sketch  "3D эскиз2340"
  sketch  "3D эскиз2341"
  sketch  "3D эскиз2342"
  sketch  "3D эскиз2343"
  sketch  "3D эскиз2344"
  sketch  "3D эскиз2345"
  sketch  "3D эскиз2346"
  sketch  "3D эскиз2347"
  sketch  "3D эскиз2348"
  sketch  "3D эскиз2349"
  sketch  "3D эскиз2350"
  sketch  "3D эскиз2351"
  sketch  "3D эскиз2352"
  sketch  "3D эскиз2353"
  sketch  "3D эскиз2354"
  sketch  "3D эскиз2355"
  sketch  "3D эскиз2356"
  sketch  "3D эскиз2357"
  sketch  "3D эскиз2358"
  sketch  "3D эскиз2359"
  sketch  "3D эскиз2360"
  sketch  "3D эскиз2361"
  sketch  "3D эскиз2362"
  sketch  "3D эскиз2363"
  sketch  "3D эскиз2364"
  sketch  "3D эскиз2365"
  sketch  "3D эскиз2366"
  sketch  "3D эскиз2367"
  sketch  "3D эскиз2368"
  sketch  "3D эскиз2369"
  sketch  "3D эскиз2370"
  sketch  "3D эскиз2371"
  sketch  "3D эскиз2372"
  sketch  "3D эскиз2373"
  sketch  "3D эскиз2374"
  sketch  "3D эскиз2375"
  sketch  "3D эскиз2376"
  sketch  "3D эскиз2377"
  sketch  "3D эскиз2378"
  sketch  "3D эскиз2379"
  sketch  "3D эскиз2380"
  sketch  "3D эскиз2381"
  sketch  "3D эскиз2382"
  sketch  "3D эскиз2383"
  sketch  "3D эскиз2384"
  sketch  "3D эскиз2385"
  sketch  "3D эскиз2386"
  sketch  "3D эскиз2387"
  sketch  "3D эскиз2388"
  sketch  "3D эскиз2389"
  sketch  "3D эскиз2390"
  sketch  "3D эскиз2391"
  sketch  "3D эскиз2392"
  sketch  "3D эскиз2393"
  sketch  "3D эскиз2394"
  sketch  "3D эскиз2395"
  sketch  "3D эскиз2396"
  sketch  "3D эскиз2397"
  sketch  "3D эскиз2398"
  sketch  "3D эскиз2399"
  sketch  "3D эскиз2400"
  sketch  "3D эскиз2401"
  sketch  "3D эскиз2402"
  sketch  "3D эскиз2403"
  sketch  "3D эскиз2404"
  sketch  "3D эскиз2405"
  sketch  "3D эскиз2406"
  sketch  "3D эскиз2407"
  sketch  "3D эскиз2408"
  sketch  "3D эскиз2409"
  sketch  "3D эскиз2410"
  sketch  "3D эскиз2411"
  sketch  "3D эскиз2412"
  sketch  "3D эскиз2413"
  sketch  "3D эскиз2414"
  sketch  "3D эскиз2415"
  sketch  "3D эскиз2416"
  sketch  "3D эскиз2417"
  sketch  "3D эскиз2418"
  sketch  "3D эскиз2419"
  sketch  "3D эскиз2420"
  sketch  "3D эскиз2421"
  sketch  "3D эскиз2422"
  sketch  "3D эскиз2423"
  sketch  "3D эскиз2424"
  sketch  "3D эскиз2425"
  sketch  "3D эскиз2426"
  sketch  "3D эскиз2427"
  sketch  "3D эскиз2428"
  sketch  "3D эскиз2429"
  sketch  "3D эскиз2430"
  sketch  "3D эскиз2431"
  sketch  "3D эскиз2432"
  sketch  "3D эскиз2433"
  sketch  "3D эскиз2434"
  sketch  "3D эскиз2435"
  sketch  "3D эскиз2436"
  sketch  "3D эскиз2437"
  sketch  "3D эскиз2438"
  sketch  "3D эскиз2439"
  other  "Твердое тело2"
  other  "Твердое тело3"
  other  "Твердое тело4"
  other  "Твердое тело5"
  other  "Твердое тело6"
  other  "Твердое тело7"
  other  "Твердое тело8"
  other  "Твердое тело9"
  other  "Твердое тело10"
  other  "Твердое тело11"
  other  "Твердое тело12"
  other  "Твердое тело13"
  other  "Твердое тело14"
  other  "Твердое тело15"
  other  "Твердое тело16"
  other  "Твердое тело17"
  other  "Твердое тело18"
  other  "Твердое тело19"
  other  "Твердое тело20"
  other  "Твердое тело21"
  other  "Твердое тело22"
  other  "Твердое тело23"
  other  "Твердое тело24"
  other  "Твердое тело25"
  other  "Твердое тело26"
  other  "Твердое тело27"
  other  "Твердое тело28"
  other  "Твердое тело29"
  other  "Твердое тело30"
  other  "Твердое тело31"
  other  "Твердое тело32"
  other  "Твердое тело33"
  other  "Твердое тело34"
  other  "Твердое тело35"
  other  "Твердое тело36"
  other  "Твердое тело37"
  other  "Твердое тело38"
  other  "Твердое тело39"
  other  "Твердое тело40"
  other  "Твердое тело41"
  other  "Твердое тело42"
  other  "Твердое тело43"
  other  "Твердое тело44"
  other  "Твердое тело45"
  other  "Твердое тело46"
  other  "Твердое тело47"
  other  "Твердое тело48"
  other  "Твердое тело49"
  other  "Твердое тело50"
  other  "Твердое тело51"
  other  "Твердое тело52"
  other  "Твердое тело53"
  other  "Твердое тело54"
  other  "Твердое тело55"
  other  "Твердое тело56"
  other  "Твердое тело57"
  other  "Твердое тело58"
  other  "Твердое тело59"
  other  "Твердое тело60"
  other  "Твердое тело61"
  other  "Твердое тело62"
  other  "Твердое тело63"
  other  "Твердое тело64"
  other  "Твердое тело65"
  other  "Твердое тело66"
  other  "Твердое тело67"
  other  "Твердое тело68"
  other  "Твердое тело69"
  other  "Твердое тело70"
  other  "Твердое тело71"
  other  "Твердое тело72"
  other  "Твердое тело73"
  other  "Твердое тело74"
  other  "Твердое тело75"
  other  "Твердое тело76"
  other  "Твердое тело77"
  other  "Твердое тело78"
  other  "Твердое тело79"
  other  "Твердое тело80"
  other  "Твердое тело81"
  other  "Твердое тело82"
  other  "Твердое тело83"
  other  "Твердое тело84"
  other  "Твердое тело85"
  other  "Твердое тело86"
  other  "Твердое тело87"
  other  "Твердое тело88"
  other  "Твердое тело89"
  other  "Твердое тело90"
  other  "Твердое тело91"
  other  "Твердое тело92"
  other  "Твердое тело93"
  other  "Твердое тело94"
  other  "Твердое тело95"
  other  "Твердое тело96"
  other  "Твердое тело97"
  other  "Твердое тело98"
  other  "Твердое тело99"
  other  "Твердое тело100"
  other  "Твердое тело101"
  other  "Твердое тело102"
  other  "Твердое тело103"
  other  "Твердое тело104"
  other  "Твердое тело105"
  other  "Твердое тело106"
  other  "Твердое тело107"
  other  "Твердое тело108"
  other  "Твердое тело109"
  other  "Твердое тело110"
  other  "Твердое тело111"
  other  "Твердое тело112"
  other  "Твердое тело113"
  other  "Твердое тело114"
  other  "Твердое тело115"
  other  "Твердое тело116"
  other  "Твердое тело117"
  other  "Твердое тело118"
  other  "Твердое тело119"
  other  "Твердое тело120"
  other  "Твердое тело121"
  other  "Твердое тело122"
  other  "Твердое тело123"
  other  "Твердое тело124"
  other  "Твердое тело125"
  other  "Твердое тело126"
  other  "Твердое тело127"
  other  "Твердое тело128"
  other  "Твердое тело129"
  other  "Твердое тело130"
  other  "Твердое тело131"
  other  "Твердое тело132"
  other  "Твердое тело133"
  other  "Твердое тело134"
  other  "Твердое тело135"
  other  "Твердое тело136"
  other  "Твердое тело137"
  other  "Твердое тело138"
  other  "Твердое тело139"
  other  "Твердое тело140"
  other  "Твердое тело141"
  other  "Твердое тело142"
  other  "Твердое тело143"
  other  "Твердое тело144"
  other  "Твердое тело145"
  other  "Твердое тело146"
  other  "Твердое тело147"
  other  "Твердое тело148"
  other  "Твердое тело149"
  other  "Твердое тело150"
  other  "Твердое тело151"
  other  "Твердое тело152"
  other  "Твердое тело153"
  other  "Твердое тело154"
  other  "Твердое тело155"
  other  "Твердое тело156"
  other  "Твердое тело157"
  other  "Твердое тело158"
  other  "Твердое тело159"
  other  "Твердое тело160"
  other  "Твердое тело161"
  other  "Твердое тело162"
  other  "Твердое тело163"
  other  "Твердое тело164"
  other  "Твердое тело165"
  other  "Твердое тело166"
  other  "Твердое тело167"
  other  "Твердое тело168"
  other  "Твердое тело169"
  other  "Твердое тело170"
  other  "Твердое тело171"
  other  "Твердое тело172"
  other  "Твердое тело173"
  other  "Твердое тело174"
  other  "Твердое тело175"
  other  "Твердое тело176"
  other  "Твердое тело177"
  other  "Твердое тело178"
  other  "Твердое тело179"
  other  "Твердое тело180"
  other  "Твердое тело181"
  other  "Твердое тело182"
  other  "Твердое тело183"
  other  "Твердое тело184"
  other  "Твердое тело185"
  other  "Твердое тело186"
  other  "Твердое тело187"
  other  "Твердое тело188"
  other  "Твердое тело189"
  other  "Твердое тело190"
  other  "Твердое тело191"
  other  "Твердое тело192"
  other  "Твердое тело193"
  other  "Твердое тело194"
  other  "Твердое тело195"
  other  "Твердое тело196"
  other  "Твердое тело197"
  other  "Твердое тело198"
  other  "Твердое тело199"
  other  "Твердое тело200"
  other  "Твердое тело201"
  other  "Твердое тело202"
  other  "Твердое тело203"
  other  "Твердое тело204"
  other  "Твердое тело205"
  other  "Твердое тело206"
  other  "Твердое тело207"
  other  "Твердое тело208"
  other  "Твердое тело209"
  other  "Твердое тело210"
  other  "Твердое тело211"
  other  "Твердое тело212"
  other  "Твердое тело213"
  other  "Твердое тело214"
  other  "Твердое тело215"
  other  "Твердое тело216"
  other  "Твердое тело217"
  other  "Твердое тело218"
  other  "Твердое тело219"
  other  "Твердое тело220"
  other  "Твердое тело221"
  other  "Твердое тело222"
  other  "Твердое тело223"
  other  "Твердое тело224"
  other  "Твердое тело225"
  other  "Твердое тело226"
  other  "Твердое тело227"
  other  "Твердое тело228"
  other  "Твердое тело229"
  other  "Твердое тело230"
  other  "Твердое тело231"
  other  "Твердое тело232"
  other  "Твердое тело233"
  other  "Твердое тело234"
  other  "Твердое тело235"
  other  "Твердое тело236"
  other  "Твердое тело237"
  other  "Твердое тело238"
  other  "Твердое тело239"
  other  "Твердое тело240"
  other  "Твердое тело241"
  other  "Твердое тело242"
  other  "Твердое тело243"
  other  "Твердое тело244"
  other  "Твердое тело245"
  other  "Твердое тело246"
  other  "Твердое тело247"
  other  "Твердое тело248"
  other  "Твердое тело249"
  other  "Твердое тело250"
  other  "Твердое тело251"
  other  "Твердое тело252"
  other  "Твердое тело253"
  other  "Твердое тело254"
  other  "Твердое тело255"
  other  "Твердое тело256"
  other  "Твердое тело257"
  other  "Твердое тело258"
  other  "Твердое тело259"
  other  "Твердое тело260"
  other  "Твердое тело261"
  other  "Твердое тело262"
  other  "Твердое тело263"
  other  "Твердое тело264"
  other  "Твердое тело265"
  other  "Твердое тело266"
  other  "Твердое тело267"
  other  "Твердое тело268"
  other  "Твердое тело269"
  other  "Твердое тело270"
  other  "Твердое тело271"
  other  "Твердое тело272"
  other  "Твердое тело273"
  other  "Твердое тело274"
  other  "Твердое тело275"
  other  "Твердое тело276"
  other  "Твердое тело277"
  other  "Твердое тело278"
  other  "Твердое тело279"
  other  "Твердое тело280"
  other  "Твердое тело281"
  other  "Твердое тело282"
  other  "Твердое тело283"
  other  "Твердое тело284"
  other  "Твердое тело285"
  other  "Твердое тело286"
  other  "Твердое тело287"
  other  "Твердое тело288"
  other  "Твердое тело289"
  other  "Твердое тело290"
  other  "Твердое тело291"
  other  "Твердое тело292"
  other  "Твердое тело293"
  other  "Твердое тело294"
  other  "Твердое тело295"
  other  "Твердое тело296"
  other  "Твердое тело297"
  other  "Твердое тело298"
  other  "Твердое тело299"
  other  "Твердое тело300"
  other  "Твердое тело301"
  other  "Твердое тело302"
  other  "Твердое тело303"
  other  "Твердое тело304"
  other  "Твердое тело305"
  other  "Твердое тело306"
  other  "Твердое тело307"
  other  "Твердое тело308"
  other  "Твердое тело309"
  other  "Твердое тело310"
  other  "Твердое тело311"
  other  "Твердое тело312"
  other  "Твердое тело313"
  other  "Твердое тело314"
  other  "Твердое тело315"
  other  "Твердое тело316"
  other  "Твердое тело317"
  other  "Твердое тело318"
  other  "Твердое тело319"
  other  "Твердое тело320"
  other  "Твердое тело321"
  other  "Твердое тело322"
  other  "Твердое тело323"
  other  "Твердое тело324"
  other  "Твердое тело325"
  other  "Твердое тело326"
  other  "Твердое тело327"
  other  "Твердое тело328"
  other  "Твердое тело329"
  other  "Твердое тело330"
  other  "Твердое тело331"
  other  "Твердое тело332"
  other  "Твердое тело333"
  other  "Твердое тело334"
  other  "Твердое тело335"
  other  "Твердое тело336"
  other  "Твердое тело337"
  other  "Твердое тело338"
  other  "Твердое тело339"
  other  "Твердое тело340"
  other  "Твердое тело341"
  other  "Твердое тело342"
  other  "Твердое тело343"
  other  "Твердое тело344"
  other  "Твердое тело345"
  other  "Твердое тело346"
  other  "Твердое тело347"
  other  "Твердое тело348"
  other  "Твердое тело349"
  other  "Твердое тело350"
  other  "Твердое тело351"
  other  "Твердое тело352"
  other  "Твердое тело353"
  other  "Твердое тело354"
  other  "Твердое тело355"
  other  "Твердое тело356"
  other  "Твердое тело357"
  other  "Твердое тело358"
  other  "Твердое тело359"
  other  "Твердое тело360"
  other  "Твердое тело361"
  other  "Твердое тело362"
  other  "Твердое тело363"
  other  "Твердое тело364"
  other  "Твердое тело365"
  other  "Твердое тело366"
  other  "Твердое тело367"
  other  "Твердое тело368"
  other  "Твердое тело369"
  other  "Твердое тело370"
  other  "Твердое тело371"
  other  "Твердое тело372"
  other  "Твердое тело373"
  other  "Твердое тело374"
  other  "Твердое тело375"
  other  "Твердое тело376"
  other  "Твердое тело377"
  other  "Твердое тело378"
  other  "Твердое тело379"
  other  "Твердое тело380"
  other  "Твердое тело381"
  other  "Твердое тело382"
  other  "Твердое тело383"
  other  "Твердое тело384"
  other  "Твердое тело385"
  other  "Твердое тело386"
  other  "Твердое тело387"
  other  "Твердое тело388"
  other  "Твердое тело389"
  other  "Твердое тело390"
  other  "Твердое тело391"
  other  "Твердое тело392"
  other  "Твердое тело393"
  other  "Твердое тело394"
  other  "Твердое тело395"
  other  "Твердое тело396"
  other  "Твердое тело397"
  other  "Твердое тело398"
  other  "Твердое тело399"
  other  "Твердое тело400"
  other  "Твердое тело401"
  other  "Твердое тело402"
  other  "Твердое тело403"
  other  "Твердое тело404"
  other  "Твердое тело405"
  other  "Твердое тело406"
  other  "Твердое тело407"
  other  "Твердое тело408"
  other  "Твердое тело409"
  other  "Твердое тело410"
  other  "Твердое тело411"
  other  "Твердое тело412"
  other  "Твердое тело413"
  other  "Твердое тело414"
  other  "Твердое тело415"
  other  "Твердое тело416"
  other  "Твердое тело417"
  other  "Твердое тело418"
  other  "Твердое тело419"
  other  "Твердое тело420"
  other  "Твердое тело421"
  other  "Твердое тело422"
  other  "Твердое тело423"
  other  "Твердое тело424"
  other  "Твердое тело425"
  other  "Твердое тело426"
  other  "Твердое тело427"
  other  "Твердое тело428"
  other  "Твердое тело429"
  other  "Твердое тело430"
  other  "Твердое тело431"
  other  "Твердое тело432"
  other  "Твердое тело433"
  other  "Твердое тело434"
  other  "Твердое тело435"
  other  "Твердое тело436"
  other  "Твердое тело437"
  other  "Твердое тело438"
  other  "Твердое тело439"
  other  "Твердое тело440"
  other  "Твердое тело441"
  other  "Твердое тело442"
  other  "Твердое тело443"
  other  "Твердое тело444"
  other  "Твердое тело445"
  other  "Твердое тело446"
  other  "Твердое тело447"
  other  "Твердое тело448"
  other  "Твердое тело449"
  other  "Твердое тело450"
  other  "Твердое тело451"
  other  "Твердое тело452"
  other  "Твердое тело453"
  other  "Твердое тело454"
  other  "Твердое тело455"
  other  "Твердое тело456"
  other  "Твердое тело457"
  other  "Твердое тело458"
  other  "Твердое тело459"
  other  "Твердое тело460"
  other  "Твердое тело461"
  other  "Твердое тело462"
  other  "Твердое тело463"
  other  "Твердое тело464"
  other  "Твердое тело465"
  other  "Твердое тело466"
  other  "Твердое тело467"
  other  "Твердое тело468"
  other  "Твердое тело469"
  other  "Твердое тело470"
  other  "Твердое тело471"
  other  "Твердое тело472"
  other  "Твердое тело473"
  other  "Твердое тело474"
  other  "Твердое тело475"
  other  "Твердое тело476"
  other  "Твердое тело477"
  other  "Твердое тело478"
  other  "Твердое тело479"
  other  "Твердое тело480"
  other  "Твердое тело481"
  other  "Твердое тело482"
  other  "Твердое тело483"
  other  "Твердое тело484"
  other  "Твердое тело485"
  other  "Твердое тело486"
  other  "Твердое тело487"
  other  "Твердое тело488"
  other  "Твердое тело489"
  other  "Твердое тело490"
  other  "Твердое тело491"
  other  "Твердое тело492"
  other  "Твердое тело493"
  other  "Твердое тело494"
  other  "Твердое тело495"
  other  "Твердое тело496"
  other  "Твердое тело497"
  other  "Твердое тело498"
  other  "Твердое тело499"
  other  "Твердое тело500"
  other  "Твердое тело501"
  other  "Твердое тело502"
  other  "Твердое тело503"
  other  "Твердое тело504"
  other  "Твердое тело505"
  other  "Твердое тело506"
  other  "Твердое тело507"
  other  "Твердое тело508"
  other  "Твердое тело509"
  other  "Твердое тело510"
  other  "Твердое тело511"
  other  "Твердое тело512"
  other  "Твердое тело513"
  other  "Твердое тело514"
  other  "Твердое тело515"
  other  "Твердое тело516"
  other  "Твердое тело517"
  other  "Твердое тело518"
  other  "Твердое тело519"
  other  "Твердое тело520"
  other  "Твердое тело521"
  other  "Твердое тело522"
  other  "Твердое тело523"
  other  "Твердое тело524"
  other  "Твердое тело525"
  other  "Твердое тело526"
  other  "Твердое тело527"
  other  "Твердое тело528"
  other  "Твердое тело529"
  other  "Твердое тело530"
  other  "Твердое тело531"
  other  "Твердое тело532"
  other  "Твердое тело533"
  other  "Твердое тело534"
  other  "Твердое тело535"
  other  "Твердое тело536"
  other  "Твердое тело537"
  other  "Твердое тело538"
  other  "Твердое тело539"
  other  "Твердое тело540"
  other  "Твердое тело541"
  other  "Твердое тело542"
  other  "Твердое тело543"
  other  "Твердое тело544"
  other  "Твердое тело545"
  other  "Твердое тело546"
  other  "Твердое тело547"
  other  "Твердое тело548"
  other  "Твердое тело549"
  other  "Твердое тело550"
  other  "Твердое тело551"
  other  "Твердое тело552"
  other  "Твердое тело553"
  other  "Твердое тело554"
  other  "Твердое тело555"
  other  "Твердое тело556"
  other  "Твердое тело557"
  other  "Твердое тело558"
  other  "Твердое тело559"
  other  "Твердое тело560"
  other  "Твердое тело561"
  other  "Твердое тело562"
  other  "Твердое тело563"
  other  "Твердое тело564"
  other  "Твердое тело565"
  other  "Твердое тело566"
  other  "Твердое тело567"
  other  "Твердое тело568"
  other  "Твердое тело569"
  other  "Твердое тело570"
  other  "Твердое тело571"
  other  "Твердое тело572"
  other  "Твердое тело573"
  other  "Твердое тело574"
  other  "Твердое тело575"
  other  "Твердое тело576"
  other  "Твердое тело577"
  other  "Твердое тело578"
  other  "Твердое тело579"
  other  "Твердое тело580"
  other  "Твердое тело581"
  other  "Твердое тело582"
  other  "Твердое тело583"
  other  "Твердое тело584"
  other  "Твердое тело585"
  other  "Твердое тело586"
  other  "Твердое тело587"
  other  "Твердое тело588"
  other  "Твердое тело589"
  other  "Твердое тело590"
  other  "Твердое тело591"
  other  "Твердое тело592"
  other  "Твердое тело593"
  other  "Твердое тело594"
  other  "Твердое тело595"
  other  "Твердое тело596"
  other  "Твердое тело597"
  other  "Твердое тело598"
  other  "Твердое тело599"
  other  "Твердое тело600"
  other  "Твердое тело601"
  other  "Твердое тело602"
  other  "Твердое тело603"
  other  "Твердое тело604"
  other  "Твердое тело605"
  other  "Твердое тело606"
  other  "Твердое тело607"
  other  "Твердое тело608"
  other  "Твердое тело609"
  other  "Твердое тело610"
  other  "Твердое тело611"
  other  "Твердое тело612"
  other  "Твердое тело613"
  other  "Твердое тело614"
  other  "Твердое тело615"
  other  "Твердое тело616"
  other  "Твердое тело617"
  other  "Твердое тело618"
  other  "Твердое тело619"
  other  "Твердое тело620"
  other  "Твердое тело621"
  other  "Твердое тело622"
  other  "Твердое тело623"
  other  "Твердое тело624"
  other  "Твердое тело625"
  other  "Твердое тело626"
  other  "Твердое тело627"
  other  "Твердое тело628"
  other  "Твердое тело629"
  other  "Твердое тело630"
  other  "Твердое тело631"
  other  "Твердое тело632"
  other  "Твердое тело633"
  other  "Твердое тело634"
  other  "Твердое тело635"
  other  "Твердое тело636"
  other  "Твердое тело637"
  other  "Твердое тело638"
  other  "Твердое тело639"
  other  "Твердое тело640"
  other  "Твердое тело641"
  other  "Твердое тело642"
  other  "Твердое тело643"
  other  "Твердое тело644"
  other  "Твердое тело645"
  other  "Твердое тело646"
  other  "Твердое тело647"
  other  "Твердое тело648"
  other  "Твердое тело649"
  other  "Твердое тело650"
  other  "Твердое тело651"
  other  "Твердое тело652"
  other  "Твердое тело653"
  other  "Твердое тело654"
  other  "Твердое тело655"
  other  "Твердое тело656"
  other  "Твердое тело657"
  other  "Твердое тело658"
  other  "Твердое тело659"
  other  "Твердое тело660"
  other  "Твердое тело661"
  other  "Твердое тело662"
  other  "Твердое тело663"
  other  "Твердое тело664"
  other  "Твердое тело665"
  other  "Твердое тело666"
  other  "Твердое тело667"
  other  "Твердое тело668"
  other  "Твердое тело669"
  other  "Твердое тело670"
  other  "Твердое тело671"
  other  "Твердое тело672"
  other  "Твердое тело673"
  other  "Твердое тело674"
  other  "Твердое тело675"
  other  "Твердое тело676"
  other  "Твердое тело677"
  other  "Твердое тело678"
  other  "Твердое тело679"
  other  "Твердое тело680"
  other  "Твердое тело681"
  other  "Твердое тело682"
  other  "Твердое тело683"
  other  "Твердое тело684"
  other  "Твердое тело685"
  other  "Твердое тело686"
  other  "Твердое тело687"
  other  "Твердое тело688"
  other  "Твердое тело689"
  other  "Твердое тело690"
  other  "Твердое тело691"
  other  "Твердое тело692"
  other  "Твердое тело693"
  other  "Твердое тело694"
  other  "Твердое тело695"
  other  "Твердое тело696"
  other  "Твердое тело697"
  other  "Твердое тело698"
  other  "Твердое тело699"
  other  "Твердое тело700"
  other  "Твердое тело701"
  other  "Твердое тело702"
  other  "Твердое тело703"
  other  "Твердое тело704"
  other  "Твердое тело705"
  other  "Твердое тело706"
  other  "Твердое тело707"
  other  "Твердое тело708"
  other  "Твердое тело709"
  other  "Твердое тело710"
  other  "Твердое тело711"
  other  "Твердое тело712"
  other  "Твердое тело713"
  other  "Твердое тело714"
  other  "Твердое тело715"
  other  "Твердое тело716"
  other  "Твердое тело717"
  other  "Твердое тело718"
  other  "Твердое тело719"
  other  "Твердое тело720"
  other  "Твердое тело721"
  other  "Твердое тело722"
  other  "Твердое тело723"
  other  "Твердое тело724"
  other  "Твердое тело725"
  other  "Твердое тело726"
  other  "Твердое тело727"
  other  "Твердое тело728"
  other  "Твердое тело729"
  other  "Твердое тело730"
  other  "Твердое тело731"
  other  "Твердое тело732"
  other  "Твердое тело733"
  other  "Твердое тело734"
  other  "Твердое тело735"
  other  "Твердое тело736"
  other  "Твердое тело737"
  other  "Твердое тело738"
  other  "Твердое тело739"
  other  "Твердое тело740"
  other  "Твердое тело741"
  other  "Твердое тело742"
  other  "Твердое тело743"
  other  "Твердое тело744"
  other  "Твердое тело745"
  other  "Твердое тело746"
  other  "Твердое тело747"
  other  "Твердое тело748"
  other  "Твердое тело749"
  other  "Твердое тело750"
  other  "Твердое тело751"
  other  "Твердое тело752"
  other  "Твердое тело753"
  other  "Твердое тело754"
  other  "Твердое тело755"
  other  "Твердое тело756"
  other  "Твердое тело757"
  other  "Твердое тело758"
  other  "Твердое тело759"
  other  "Твердое тело760"
  other  "Твердое тело761"
  other  "Твердое тело762"
  other  "Твердое тело763"
  other  "Твердое тело764"
  other  "Твердое тело765"
  other  "Твердое тело766"
  other  "Твердое тело767"
  other  "Твердое тело768"
  other  "Твердое тело769"
  other  "Твердое тело770"
  other  "Твердое тело771"
  other  "Твердое тело772"
  other  "Твердое тело773"
  other  "Твердое тело774"
  other  "Твердое тело775"
  other  "Твердое тело776"
  other  "Твердое тело777"
  other  "Твердое тело778"
  other  "Твердое тело779"
  other  "Твердое тело780"
  other  "Твердое тело781"
  other  "Твердое тело782"
  other  "Твердое тело783"
  other  "Твердое тело784"
  other  "Твердое тело785"
  other  "Твердое тело786"
  other  "Твердое тело787"
  other  "Твердое тело788"
  other  "Твердое тело789"
  other  "Твердое тело790"
  other  "Твердое тело791"
  other  "Твердое тело792"
  other  "Твердое тело793"
  other  "Твердое тело794"
  other  "Твердое тело795"
  other  "Твердое тело796"
  other  "Твердое тело797"
  other  "Твердое тело798"
  other  "Твердое тело799"
  other  "Твердое тело800"
  other  "Твердое тело801"
  other  "Твердое тело802"
  other  "Твердое тело803"
  other  "Твердое тело804"
  other  "Твердое тело805"
  other  "Твердое тело806"
  other  "Твердое тело807"
  other  "Твердое тело808"
  other  "Твердое тело809"
  other  "Твердое тело810"
  other  "Твердое тело811"
  other  "Твердое тело812"
  other  "Твердое тело813"
  other  "Твердое тело814"
  other  "Твердое тело815"
  other  "Твердое тело816"
  other  "Твердое тело817"
  other  "Твердое тело818"
  other  "Твердое тело819"
  other  "Твердое тело820"
  other  "Твердое тело821"
  other  "Твердое тело822"
  other  "Твердое тело823"
  other  "Твердое тело824"
  other  "Твердое тело825"
  other  "Твердое тело826"
  other  "Твердое тело827"
  other  "Твердое тело828"
  other  "Твердое тело829"
  other  "Твердое тело830"
  other  "Твердое тело831"
  other  "Твердое тело832"
  other  "Твердое тело833"
  other  "Твердое тело834"
  other  "Твердое тело835"
  other  "Твердое тело836"
  other  "Твердое тело837"
  other  "Твердое тело838"
  other  "Твердое тело839"
  other  "Твердое тело840"
  other  "Твердое тело841"
  other  "Твердое тело842"
  other  "Твердое тело843"
  other  "Твердое тело844"
  other  "Твердое тело845"
  other  "Твердое тело846"
  other  "Твердое тело847"
  other  "Твердое тело848"
  other  "Твердое тело849"
  other  "Твердое тело850"
  other  "Твердое тело851"
  other  "Твердое тело852"
  other  "Твердое тело853"
  other  "Твердое тело854"
  other  "Твердое тело855"
  other  "Твердое тело856"
  other  "Твердое тело857"
  other  "Твердое тело858"
  other  "Твердое тело859"
  other  "Твердое тело860"
  other  "Твердое тело861"
  other  "Твердое тело862"
  other  "Твердое тело863"
  other  "Твердое тело864"
  other  "Твердое тело865"
  other  "Твердое тело866"
  other  "Твердое тело867"
  other  "Твердое тело868"
  other  "Твердое тело869"
  other  "Твердое тело870"
  other  "Твердое тело871"
  other  "Твердое тело872"
  other  "Твердое тело873"
  other  "Твердое тело874"
  other  "Твердое тело875"
  other  "Твердое тело876"
  other  "Твердое тело877"
  other  "Твердое тело878"
  other  "Твердое тело879"
  other  "Твердое тело880"
  other  "Твердое тело881"
  other  "Твердое тело882"
  other  "Твердое тело883"
  other  "Твердое тело884"
  other  "Твердое тело885"
  other  "Твердое тело886"
  other  "Твердое тело887"
  other  "Твердое тело888"
  other  "Твердое тело889"
  other  "Твердое тело890"
  other  "Твердое тело891"
  other  "Твердое тело892"
  other  "Твердое тело893"
  other  "Твердое тело894"
  other  "Твердое тело895"
  other  "Твердое тело896"
  other  "Твердое тело897"
  other  "Твердое тело898"
  other  "Твердое тело899"
  other  "Твердое тело900"
  other  "Твердое тело901"
  other  "Твердое тело902"
  other  "Твердое тело903"
  other  "Твердое тело904"
  other  "Твердое тело905"
  other  "Твердое тело906"
  other  "Твердое тело907"
  other  "Твердое тело908"
  other  "Твердое тело909"
  other  "Твердое тело910"
  other  "Твердое тело911"
  other  "Твердое тело912"
  other  "Твердое тело913"
  other  "Твердое тело914"
  other  "Твердое тело915"
  other  "Твердое тело916"
  other  "Твердое тело917"
  other  "Твердое тело918"
  other  "Твердое тело919"
  other  "Твердое тело920"
  other  "Твердое тело921"
  other  "Твердое тело922"
  other  "Твердое тело923"
  other  "Твердое тело924"
  other  "Твердое тело925"
  other  "Твердое тело926"
  other  "Твердое тело927"
  other  "Твердое тело928"
  other  "Твердое тело929"
  other  "Твердое тело930"
  other  "Твердое тело931"
  other  "Твердое тело932"
  other  "Твердое тело933"
  other  "Твердое тело934"
  other  "Твердое тело935"
  other  "Твердое тело936"
  other  "Твердое тело937"
  other  "Твердое тело938"
  other  "Твердое тело939"
  other  "Твердое тело940"
  other  "Твердое тело941"
  other  "Твердое тело942"
  other  "Твердое тело943"
  other  "Твердое тело944"
  other  "Твердое тело945"
  other  "Твердое тело946"
  other  "Твердое тело947"
  other  "Твердое тело948"
  other  "Твердое тело949"
  other  "Твердое тело950"
  other  "Твердое тело951"
  other  "Твердое тело952"
  other  "Твердое тело953"
  other  "Твердое тело954"
  other  "Твердое тело955"
  other  "Твердое тело956"
  other  "Твердое тело957"
  other  "Твердое тело958"
  other  "Твердое тело959"
  other  "Твердое тело960"
  other  "Твердое тело961"
  other  "Твердое тело962"
  other  "Твердое тело963"
  other  "Твердое тело964"
  other  "Твердое тело965"
  other  "Твердое тело966"
  other  "Твердое тело967"
  other  "Твердое тело968"
  other  "Твердое тело969"
  other  "Твердое тело970"
  other  "Твердое тело971"
  other  "Твердое тело972"
  other  "Твердое тело973"
  other  "Твердое тело974"
  other  "Твердое тело975"
  other  "Твердое тело976"
  other  "Твердое тело977"
  other  "Твердое тело978"
  other  "Твердое тело979"
  other  "Твердое тело980"
  other  "Твердое тело981"
  other  "Твердое тело982"
  other  "Твердое тело983"
  other  "Твердое тело984"
  other  "Твердое тело985"
  other  "Твердое тело986"
  other  "Твердое тело987"
  other  "Твердое тело988"
  other  "Твердое тело989"
  other  "Твердое тело990"
  other  "Твердое тело991"
  other  "Твердое тело992"
  other  "Твердое тело993"
  other  "Твердое тело994"
  other  "Твердое тело995"
  other  "Твердое тело996"
  other  "Твердое тело997"
  other  "Твердое тело998"
  other  "Твердое тело999"
  other  "Твердое тело1000"
  other  "Твердое тело1001"
  other  "Твердое тело1002"
  other  "Твердое тело1003"
  other  "Твердое тело1004"
  other  "Твердое тело1005"
  other  "Твердое тело1006"
  other  "Твердое тело1007"
  other  "Твердое тело1008"
  other  "Твердое тело1009"
  other  "Твердое тело1010"
  other  "Твердое тело1011"
  other  "Твердое тело1012"
  other  "Твердое тело1013"
  other  "Твердое тело1014"
  other  "Твердое тело1015"
  other  "Твердое тело1016"
  other  "Твердое тело1017"
  other  "Твердое тело1018"
  other  "Твердое тело1019"
  other  "Твердое тело1020"
  other  "Твердое тело1021"
  other  "Твердое тело1022"
  other  "Твердое тело1023"
  other  "Твердое тело1024"
  other  "Твердое тело1025"
  other  "Твердое тело1026"
  other  "Твердое тело1027"
  other  "Твердое тело1028"
  other  "Твердое тело1029"
  other  "Твердое тело1030"
  other  "Твердое тело1031"
  other  "Твердое тело1032"
  other  "Твердое тело1033"
  other  "Твердое тело1034"
  other  "Твердое тело1035"
  other  "Твердое тело1036"
  other  "Твердое тело1037"
  other  "Твердое тело1038"
  other  "Твердое тело1039"
  other  "Твердое тело1040"
  other  "Твердое тело1041"
  other  "Твердое тело1042"
  other  "Твердое тело1043"
  other  "Твердое тело1044"
  other  "Твердое тело1045"
  other  "Твердое тело1046"
  other  "Твердое тело1047"
  other  "Твердое тело1048"
  other  "Твердое тело1049"
  other  "Твердое тело1050"
  other  "Твердое тело1051"
  other  "Твердое тело1052"
  other  "Твердое тело1053"
  other  "Твердое тело1054"
  other  "Твердое тело1055"
  other  "Твердое тело1056"
  other  "Твердое тело1057"
  other  "Твердое тело1058"
  other  "Твердое тело1059"
  other  "Твердое тело1060"
  other  "Твердое тело1061"
  other  "Твердое тело1062"
  other  "Твердое тело1063"
  other  "Твердое тело1064"
  other  "Твердое тело1065"
  other  "Твердое тело1066"
  other  "Твердое тело1067"
  other  "Твердое тело1068"
  other  "Твердое тело1069"
  other  "Твердое тело1070"
  other  "Твердое тело1071"
  other  "Твердое тело1072"
  other  "Твердое тело1073"
  other  "Твердое тело1074"
  other  "Твердое тело1075"
  other  "Твердое тело1076"
  other  "Твердое тело1077"
  other  "Твердое тело1078"
  other  "Твердое тело1079"
  other  "Твердое тело1080"
  other  "Твердое тело1081"
  other  "Твердое тело1082"
  other  "Твердое тело1083"
  other  "Твердое тело1084"
  other  "Твердое тело1085"
  other  "Твердое тело1086"
  other  "Твердое тело1087"
  other  "Твердое тело1088"
  other  "Твердое тело1089"
  other  "Твердое тело1090"
  other  "Твердое тело1091"
  other  "Твердое тело1092"
  other  "Твердое тело1093"
  other  "Твердое тело1094"
  other  "Твердое тело1095"
  other  "Твердое тело1096"
  other  "Твердое тело1097"
  other  "Твердое тело1098"
  other  "Твердое тело1099"
  other  "Твердое тело1100"
  other  "Твердое тело1101"
  other  "Твердое тело1102"
  other  "Твердое тело1103"
  other  "Твердое тело1104"
  other  "Твердое тело1105"
  other  "Твердое тело1106"
  other  "Твердое тело1107"
  other  "Твердое тело1108"
  other  "Твердое тело1109"
  other  "Твердое тело1110"
  other  "Твердое тело1111"
  other  "Твердое тело1112"
  other  "Твердое тело1113"
  other  "Твердое тело1114"
  other  "Твердое тело1115"
  other  "Твердое тело1116"
  other  "Твердое тело1117"
  other  "Твердое тело1118"
  other  "Твердое тело1119"
  other  "Твердое тело1120"
  other  "Твердое тело1121"
  other  "Твердое тело1122"
  other  "Твердое тело1123"
  other  "Твердое тело1124"
  other  "Твердое тело1125"
  other  "Твердое тело1126"
  other  "Твердое тело1127"
  other  "Твердое тело1128"
  other  "Твердое тело1129"
  other  "Твердое тело1130"
  other  "Твердое тело1131"
  other  "Твердое тело1132"
  other  "Твердое тело1133"
  other  "Твердое тело1134"
  other  "Твердое тело1135"
  other  "Твердое тело1136"
  other  "Твердое тело1137"
  other  "Твердое тело1138"
  other  "Твердое тело1139"
  other  "Твердое тело1140"
  other  "Твердое тело1141"
  other  "Твердое тело1142"
  other  "Твердое тело1143"
  other  "Твердое тело1144"
  other  "Твердое тело1145"
  other  "Твердое тело1146"
  other  "Твердое тело1147"
  other  "Твердое тело1148"
  other  "Твердое тело1149"
  other  "Твердое тело1150"
  other  "Твердое тело1151"
  other  "Твердое тело1152"
  other  "Твердое тело1153"
  other  "Твердое тело1154"
  other  "Твердое тело1155"
  other  "Твердое тело1156"
  other  "Твердое тело1157"
  other  "Твердое тело1158"
  other  "Твердое тело1159"
  other  "Твердое тело1160"
  other  "Твердое тело1161"
  other  "Твердое тело1162"
  other  "Твердое тело1163"
  other  "Твердое тело1164"
  other  "Твердое тело1165"
  other  "Твердое тело1166"
  other  "Твердое тело1167"
  other  "Твердое тело1168"
  other  "Твердое тело1169"
  other  "Твердое тело1170"
  other  "Твердое тело1171"
  other  "Твердое тело1172"
  other  "Твердое тело1173"
  other  "Твердое тело1174"
  other  "Твердое тело1175"
  other  "Твердое тело1176"
  other  "Твердое тело1177"
  other  "Твердое тело1178"
  other  "Твердое тело1179"
  other  "Твердое тело1180"
  other  "Твердое тело1181"
  other  "Твердое тело1182"
  other  "Твердое тело1183"
  other  "Твердое тело1184"
  other  "Твердое тело1185"
  other  "Твердое тело1186"
  other  "Твердое тело1187"
  other  "Твердое тело1188"
  other  "Твердое тело1189"
  other  "Твердое тело1190"
  other  "Твердое тело1191"
  other  "Твердое тело1192"
  other  "Твердое тело1193"
  other  "Твердое тело1194"
  other  "Твердое тело1195"
  other  "Твердое тело1196"
  other  "Твердое тело1197"
  other  "Твердое тело1198"
  other  "Твердое тело1199"
  other  "Твердое тело1200"
  other  "Твердое тело1201"
  other  "Твердое тело1202"
  other  "Твердое тело1203"
  other  "Твердое тело1204"
  other  "Твердое тело1205"
  other  "Твердое тело1206"
  other  "Твердое тело1207"
  other  "Твердое тело1208"
  other  "Твердое тело1209"
  other  "Твердое тело1210"
  other  "Твердое тело1211"
  other  "Твердое тело1212"
  other  "Твердое тело1213"
  other  "Твердое тело1214"
  other  "Твердое тело1215"
  other  "Твердое тело1216"
  other  "Твердое тело1217"
  other  "Твердое тело1218"
  other  "Твердое тело1219"
  other  "Твердое тело1220"
  other  "Твердое тело1221"
  other  "Твердое тело1222"
  other  "Твердое тело1223"
  other  "Твердое тело1224"
  other  "Твердое тело1225"
  other  "Твердое тело1226"
  other  "Твердое тело1227"
  other  "Твердое тело1228"
  other  "Твердое тело1229"
  other  "Твердое тело1230"
  other  "Твердое тело1231"
  other  "Твердое тело1232"
  other  "Твердое тело1233"
  other  "Твердое тело1234"
  other  "Твердое тело1235"
  other  "Твердое тело1236"
  other  "Твердое тело1237"
  other  "Твердое тело1238"
  other  "Твердое тело1239"
  other  "Твердое тело1240"
  other  "Твердое тело1241"
  other  "Твердое тело1242"
  other  "Твердое тело1243"
  other  "Твердое тело1244"
  other  "Твердое тело1245"
  other  "Твердое тело1246"
  other  "Твердое тело1247"
  other  "Твердое тело1248"
  other  "Твердое тело1249"
  other  "Твердое тело1250"
  other  "Твердое тело1251"
  other  "Твердое тело1252"
  other  "Твердое тело1253"
  other  "Твердое тело1254"
  other  "Твердое тело1255"
  other  "Твердое тело1256"
  other  "Твердое тело1257"
  other  "Твердое тело1258"
  other  "Твердое тело1259"
  other  "Твердое тело1260"
  other  "Твердое тело1261"
  other  "Твердое тело1262"
  other  "Твердое тело1263"
  other  "Твердое тело1264"
  other  "Твердое тело1265"
  other  "Твердое тело1266"
  other  "Твердое тело1267"
  other  "Твердое тело1268"
  other  "Твердое тело1269"
  other  "Твердое тело1270"
  other  "Твердое тело1271"
  other  "Твердое тело1272"
  other  "Твердое тело1273"
  other  "Твердое тело1274"
  other  "Твердое тело1275"
  other  "Твердое тело1276"
  other  "Твердое тело1277"
  other  "Твердое тело1278"
  other  "Твердое тело1279"
  other  "Твердое тело1280"
  other  "Твердое тело1281"
  other  "Твердое тело1282"
  other  "Твердое тело1283"
  other  "Твердое тело1284"
  other  "Твердое тело1285"
  other  "Твердое тело1286"
  other  "Твердое тело1287"
  other  "Твердое тело1288"
  other  "Твердое тело1289"
  other  "Твердое тело1290"
  other  "Твердое тело1291"
  other  "Твердое тело1292"
  other  "Твердое тело1293"
  other  "Твердое тело1294"
  other  "Твердое тело1295"
  other  "Твердое тело1296"
  other  "Твердое тело1297"
  other  "Твердое тело1298"
  other  "Твердое тело1299"
  other  "Твердое тело1300"
  other  "Твердое тело1301"
  other  "Твердое тело1302"
  other  "Твердое тело1303"
  other  "Твердое тело1304"
  other  "Твердое тело1305"
  other  "Твердое тело1306"
  other  "Твердое тело1307"
  other  "Твердое тело1308"
  other  "Твердое тело1309"
  other  "Твердое тело1310"
  other  "Твердое тело1311"
  other  "Твердое тело1312"
  other  "Твердое тело1313"
  other  "Твердое тело1314"
  other  "Твердое тело1315"
  other  "Твердое тело1316"
  other  "Твердое тело1317"
  other  "Твердое тело1318"
  other  "Твердое тело1319"
  other  "Твердое тело1320"
  other  "Твердое тело1321"
  other  "Твердое тело1322"
  other  "Твердое тело1323"
  other  "Твердое тело1324"
  other  "Твердое тело1325"
  other  "Твердое тело1326"
  other  "Твердое тело1327"
  other  "Твердое тело1328"
  other  "Твердое тело1329"
  other  "Твердое тело1330"
  other  "Твердое тело1331"
  other  "Твердое тело1332"
  other  "Твердое тело1333"
  other  "Твердое тело1334"
  other  "Твердое тело1335"
  other  "Твердое тело1336"
  other  "Твердое тело1337"
  other  "Твердое тело1338"
  other  "Твердое тело1339"
  other  "Твердое тело1340"
  other  "Твердое тело1341"
  other  "Твердое тело1342"
  other  "Твердое тело1343"
  other  "Твердое тело1344"
  other  "Твердое тело1345"
  other  "Твердое тело1346"
  other  "Твердое тело1347"
  other  "Твердое тело1348"
  other  "Твердое тело1349"
  other  "Твердое тело1350"
  other  "Твердое тело1351"
  other  "Твердое тело1352"
  other  "Твердое тело1353"
  other  "Твердое тело1354"
  other  "Твердое тело1355"
  other  "Твердое тело1356"
  other  "Твердое тело1357"
  other  "Твердое тело1358"
  other  "Твердое тело1359"
  other  "Твердое тело1360"
  other  "Твердое тело1361"
  other  "Твердое тело1362"
  other  "Твердое тело1363"
  other  "Твердое тело1364"
  other  "Твердое тело1365"
  other  "Твердое тело1366"
  other  "Твердое тело1367"
  other  "Твердое тело1368"
  other  "Твердое тело1369"
  other  "Твердое тело1370"
  other  "Твердое тело1371"
  other  "Твердое тело1372"
  other  "Твердое тело1373"
  other  "Твердое тело1374"
  other  "Твердое тело1375"
  other  "Твердое тело1376"
  other  "Твердое тело1377"
  other  "Твердое тело1378"
  other  "Твердое тело1379"
  other  "Твердое тело1380"
  other  "Твердое тело1381"
  other  "Твердое тело1382"
  other  "Твердое тело1383"
  other  "Твердое тело1384"
  other  "Твердое тело1385"
  other  "Твердое тело1386"
  other  "Твердое тело1387"
  other  "Твердое тело1388"
  other  "Твердое тело1389"
  other  "Твердое тело1390"
  other  "Твердое тело1391"
  other  "Твердое тело1392"
  other  "Твердое тело1393"
  other  "Твердое тело1394"
  other  "Твердое тело1395"
  other  "Твердое тело1396"
  other  "Твердое тело1397"
  other  "Твердое тело1398"
  other  "Твердое тело1399"
  other  "Твердое тело1400"
  other  "Твердое тело1401"
  other  "Твердое тело1402"
  other  "Твердое тело1403"
  other  "Твердое тело1404"
  other  "Твердое тело1405"
  other  "Твердое тело1406"
  other  "Твердое тело1407"
  other  "Твердое тело1408"
  other  "Твердое тело1409"
  other  "Твердое тело1410"
  other  "Твердое тело1411"
  other  "Твердое тело1412"
  other  "Твердое тело1413"
  other  "Твердое тело1414"
  other  "Твердое тело1415"
  other  "Твердое тело1416"
  other  "Твердое тело1417"
  other  "Твердое тело1418"
  other  "Твердое тело1419"
  other  "Твердое тело1420"
  other  "Твердое тело1421"
  other  "Твердое тело1422"
  other  "Твердое тело1423"
  other  "Твердое тело1424"
  other  "Твердое тело1425"
  other  "Твердое тело1426"
  other  "Твердое тело1427"
  other  "Твердое тело1428"
  other  "Твердое тело1429"
  other  "Твердое тело1430"
  other  "Твердое тело1431"
  other  "Твердое тело1432"
  other  "Твердое тело1433"
  other  "Твердое тело1434"
  other  "Твердое тело1435"
  other  "Твердое тело1436"
  other  "Твердое тело1437"
  other  "Твердое тело1438"
  other  "Твердое тело1439"
  other  "Твердое тело1440"
  other  "Твердое тело1441"
  other  "Твердое тело1442"
  other  "Твердое тело1443"
  other  "Твердое тело1444"
  other  "Твердое тело1445"
  other  "Твердое тело1446"
  other  "Твердое тело1447"
  other  "Твердое тело1448"
  other  "Твердое тело1449"
  other  "Твердое тело1450"
  other  "Твердое тело1451"
  other  "Твердое тело1452"
  other  "Твердое тело1453"
  other  "Твердое тело1454"
  other  "Твердое тело1455"
  other  "Твердое тело1456"
  other  "Твердое тело1457"
  other  "Твердое тело1458"
  other  "Твердое тело1459"
  other  "Твердое тело1460"
  other  "Твердое тело1461"
  other  "Твердое тело1462"
  other  "Твердое тело1463"
  other  "Твердое тело1464"
  other  "Твердое тело1465"
  other  "Твердое тело1466"
  other  "Твердое тело1467"
  other  "Твердое тело1468"
  other  "Твердое тело1469"
  other  "Твердое тело1470"
  other  "Твердое тело1471"
  other  "Твердое тело1472"
  other  "Твердое тело1473"
  other  "Твердое тело1474"
  other  "Твердое тело1475"
  other  "Твердое тело1476"
  other  "Твердое тело1477"
  other  "Твердое тело1478"
  other  "Твердое тело1479"
  other  "Твердое тело1480"
  other  "Твердое тело1481"
  other  "Твердое тело1482"
  other  "Твердое тело1483"
  other  "Твердое тело1484"
  other  "Твердое тело1485"
  other  "Твердое тело1486"
  other  "Твердое тело1487"
  other  "Твердое тело1488"
  other  "Твердое тело1489"
  other  "Твердое тело1490"
  other  "Твердое тело1491"
  other  "Твердое тело1492"
  other  "Твердое тело1493"
  other  "Твердое тело1494"
  other  "Твердое тело1495"
  other  "Твердое тело1496"
  other  "Твердое тело1497"
  other  "Твердое тело1498"
  other  "Твердое тело1499"
  other  "Твердое тело1500"
  other  "Твердое тело1501"
  other  "Твердое тело1502"
  other  "Твердое тело1503"
  other  "Твердое тело1504"
  other  "Твердое тело1505"
  other  "Твердое тело1506"
  other  "Твердое тело1507"
  other  "Твердое тело1508"
  other  "Твердое тело1509"
  other  "Твердое тело1510"
  other  "Твердое тело1511"
  other  "Твердое тело1512"
  other  "Твердое тело1513"
  other  "Твердое тело1514"
  other  "Твердое тело1515"
  other  "Твердое тело1516"
  other  "Твердое тело1517"
  other  "Твердое тело1518"
  other  "Твердое тело1519"
  other  "Твердое тело1520"
  other  "Твердое тело1521"
  other  "Твердое тело1522"
  other  "Твердое тело1523"
  other  "Твердое тело1524"
  other  "Твердое тело1525"
  other  "Твердое тело1526"
  other  "Твердое тело1527"
  other  "Твердое тело1528"
  other  "Твердое тело1529"
  other  "Твердое тело1530"
  other  "Твердое тело1531"
  other  "Твердое тело1532"
  other  "Твердое тело1533"
  other  "Твердое тело1534"
  other  "Твердое тело1535"
  other  "Твердое тело1536"
  other  "Твердое тело1537"
  other  "Твердое тело1538"
  other  "Твердое тело1539"
  other  "Твердое тело1540"
  other  "Твердое тело1541"
  other  "Твердое тело1542"
  other  "Твердое тело1543"
  other  "Твердое тело1544"
  other  "Твердое тело1545"
  other  "Твердое тело1546"
  other  "Твердое тело1547"
  other  "Твердое тело1548"
  other  "Твердое тело1549"
  other  "Твердое тело1550"
  other  "Твердое тело1551"
  other  "Твердое тело1552"
  other  "Твердое тело1553"
  other  "Твердое тело1554"
  other  "Твердое тело1555"
  other  "Твердое тело1556"
  other  "Твердое тело1557"
  other  "Твердое тело1558"
  other  "Твердое тело1559"
  other  "Твердое тело1560"
  other  "Твердое тело1561"
  other  "Твердое тело1562"
  other  "Твердое тело1563"
  other  "Твердое тело1564"
  other  "Твердое тело1565"
  other  "Твердое тело1566"
  other  "Твердое тело1567"
  other  "Твердое тело1568"
  other  "Твердое тело1569"
  other  "Твердое тело1570"
  other  "Твердое тело1571"
  other  "Твердое тело1572"
  other  "Твердое тело1573"
  other  "Твердое тело1574"
  other  "Твердое тело1575"
  other  "Твердое тело1576"
  other  "Твердое тело1577"
  other  "Твердое тело1578"
  other  "Твердое тело1579"
  other  "Твердое тело1580"
  other  "Твердое тело1581"
  other  "Твердое тело1582"
  other  "Твердое тело1583"
  other  "Твердое тело1584"
  other  "Твердое тело1585"
  other  "Твердое тело1586"
  other  "Твердое тело1587"
  other  "Твердое тело1588"
  other  "Твердое тело1589"
  other  "Твердое тело1590"
  other  "Твердое тело1591"
  other  "Твердое тело1592"
  other  "Твердое тело1593"
  other  "Твердое тело1594"
  other  "Твердое тело1595"
  other  "Твердое тело1596"
  other  "Твердое тело1597"
  other  "Твердое тело1598"
  other  "Твердое тело1599"
  other  "Твердое тело1600"
  other  "Твердое тело1601"
  other  "Твердое тело1602"
  other  "Твердое тело1603"
  other  "Твердое тело1604"
  other  "Твердое тело1605"
  other  "Твердое тело1606"
  other  "Твердое тело1607"
  other  "Твердое тело1608"
  other  "Твердое тело1609"
  other  "Твердое тело1610"
  other  "Твердое тело1611"
  other  "Твердое тело1612"
  other  "Твердое тело1613"
  other  "Твердое тело1614"
  other  "Твердое тело1615"
  other  "Твердое тело1616"
  other  "Твердое тело1617"
  other  "Твердое тело1618"
  other  "Твердое тело1619"
  other  "Твердое тело1620"
  other  "Твердое тело1621"
  other  "Твердое тело1622"
  other  "Твердое тело1623"
  other  "Твердое тело1624"
  other  "Твердое тело1625"
  other  "Твердое тело1626"
  other  "Твердое тело1627"
  other  "Твердое тело1628"
  other  "Твердое тело1629"
  other  "Твердое тело1630"
  other  "Твердое тело1631"
  other  "Твердое тело1632"
  other  "Твердое тело1633"
  other  "Твердое тело1634"
  other  "Твердое тело1635"
  other  "Твердое тело1636"
  other  "Твердое тело1637"
  other  "Твердое тело1638"
  other  "Твердое тело1639"
  other  "Твердое тело1640"
  other  "Твердое тело1641"
  other  "Твердое тело1642"
  other  "Твердое тело1643"
  other  "Твердое тело1644"
  other  "Твердое тело1645"
  other  "Твердое тело1646"
  other  "Твердое тело1647"
  other  "Твердое тело1648"
  other  "Твердое тело1649"
  other  "Твердое тело1650"
  other  "Твердое тело1651"
  other  "Твердое тело1652"
  other  "Твердое тело1653"
  other  "Твердое тело1654"
  other  "Твердое тело1655"
  other  "Твердое тело1656"
  other  "Твердое тело1657"
  other  "Твердое тело1658"
  other  "Твердое тело1659"
  other  "Твердое тело1660"
  other  "Твердое тело1661"
  other  "Твердое тело1662"
  other  "Твердое тело1663"
  other  "Твердое тело1664"
  other  "Твердое тело1665"
  other  "Твердое тело1666"
  other  "Твердое тело1667"
  other  "Твердое тело1668"
  other  "Твердое тело1669"
  other  "Твердое тело1670"
  other  "Твердое тело1671"
  other  "Твердое тело1672"
  other  "Твердое тело1673"
  other  "Твердое тело1674"
  other  "Твердое тело1675"
  other  "Твердое тело1676"
  other  "Твердое тело1677"
  other  "Твердое тело1678"
  other  "Твердое тело1679"
  other  "Твердое тело1680"
  other  "Твердое тело1681"
  other  "Твердое тело1682"
  other  "Твердое тело1683"
  other  "Твердое тело1684"
  other  "Твердое тело1685"
  other  "Твердое тело1686"
  other  "Твердое тело1687"
  other  "Твердое тело1688"
  other  "Твердое тело1689"
  other  "Твердое тело1690"
  other  "Твердое тело1691"
  other  "Твердое тело1692"
  other  "Твердое тело1693"
  other  "Твердое тело1694"
  other  "Твердое тело1695"
  other  "Твердое тело1696"
  other  "Твердое тело1697"
  other  "Твердое тело1698"
  other  "Твердое тело1699"
  other  "Твердое тело1700"
  other  "Твердое тело1701"
  other  "Твердое тело1702"
  other  "Твердое тело1703"
  other  "Твердое тело1704"
  other  "Твердое тело1705"
  other  "Твердое тело1706"
  other  "Твердое тело1707"
  other  "Твердое тело1708"
  other  "Твердое тело1709"
  other  "Твердое тело1710"
  other  "Твердое тело1711"
  other  "Твердое тело1712"
  other  "Твердое тело1713"
  other  "Твердое тело1714"
  other  "Твердое тело1715"
  other  "Твердое тело1716"
  other  "Твердое тело1717"
  other  "Твердое тело1718"
  other  "Твердое тело1719"
  other  "Твердое тело1720"
  other  "Твердое тело1721"
  other  "Твердое тело1722"
  other  "Твердое тело1723"
  other  "Твердое тело1724"
  other  "Твердое тело1725"
  other  "Твердое тело1726"
  other  "Твердое тело1727"
  other  "Твердое тело1728"
  other  "Твердое тело1729"
  other  "Твердое тело1730"
  other  "Твердое тело1731"
  other  "Твердое тело1732"
  other  "Твердое тело1733"
  other  "Твердое тело1734"
  other  "Твердое тело1735"
  other  "Твердое тело1736"
  other  "Твердое тело1737"
  other  "Твердое тело1738"
  other  "Твердое тело1739"
  other  "Твердое тело1740"
  other  "Твердое тело1741"
  other  "Твердое тело1742"
  other  "Твердое тело1743"
  other  "Твердое тело1744"
  other  "Твердое тело1745"
  other  "Твердое тело1746"
  other  "Твердое тело1747"
  other  "Твердое тело1748"
  other  "Твердое тело1749"
  other  "Твердое тело1750"
  other  "Твердое тело1751"
  other  "Твердое тело1752"
  other  "Твердое тело1753"
  other  "Твердое тело1754"
  other  "Твердое тело1755"
  other  "Твердое тело1756"
  other  "Твердое тело1757"
  other  "Твердое тело1758"
  other  "Твердое тело1759"
  other  "Твердое тело1760"
  other  "Твердое тело1761"
  other  "Твердое тело1762"
  other  "Твердое тело1763"
  other  "Твердое тело1764"
  other  "Твердое тело1765"
  other  "Твердое тело1766"
  other  "Твердое тело1767"
  other  "Твердое тело1768"
  other  "Твердое тело1769"
  other  "Твердое тело1770"
  other  "Твердое тело1771"
  other  "Твердое тело1772"
  other  "Твердое тело1773"
  other  "Твердое тело1774"
  other  "Твердое тело1775"
  other  "Твердое тело1776"
  other  "Твердое тело1777"
  other  "Твердое тело1778"
  other  "Твердое тело1779"
  other  "Твердое тело1780"
  other  "Твердое тело1781"
  other  "Твердое тело1782"
  other  "Твердое тело1783"
  other  "Твердое тело1784"
  other  "Твердое тело1785"
  other  "Твердое тело1786"
  other  "Твердое тело1787"
  other  "Твердое тело1788"
  other  "Твердое тело1789"
  other  "Твердое тело1790"
  other  "Твердое тело1791"
  other  "Твердое тело1792"
  other  "Твердое тело1793"
  other  "Твердое тело1794"
  other  "Твердое тело1795"
  other  "Твердое тело1796"
  other  "Твердое тело1797"
  other  "Твердое тело1798"
  other  "Твердое тело1799"
  other  "Твердое тело1800"
  other  "Твердое тело1801"
  other  "Твердое тело1802"
  other  "Твердое тело1803"
  other  "Твердое тело1804"
  other  "Твердое тело1805"
  other  "Твердое тело1806"
  other  "Твердое тело1807"
  other  "Твердое тело1808"
  other  "Твердое тело1809"
  other  "Твердое тело1810"
  other  "Твердое тело1811"
  other  "Твердое тело1812"
  other  "Твердое тело1813"
  other  "Твердое тело1814"
  other  "Твердое тело1815"
  other  "Твердое тело1816"
  sketch  "3D эскиз2440"
  other  "Open CASCADE STEP translator 7.5 1.1.1_1:1"
  other  "B2B-PH-K-S_3:1"
  extrude  "Extruded_5:1"  [1 undecoded]
  other  "KTD0621_8:1"
  other  "KTD0621_10:1"
  other  "User Library-User Library-res0402_res0402_body_12:1"
  other  "User Library-User Library-res0402_res0402_body_14:1"
  other  "User Library-User Library-res0402_res0402_body_16:1"
  other  "User Library-DF40C-100DP-0_4V(51)_21:1"
  other  "User Library-DF40C-100DP-0_4V(51)_22:1"
  other  "200-ball_VFBGAold.step_23:1"
  other  "200-ball_VFBGAold.step_23:2"
  other  "200-ball_VFBGAold.step_23:3"
  other  "200-ball_VFBGAold.step_23:4"
  other  "200-ball_VFBGAold.step_23:5"
  other  "200-ball_VFBGAold.step_23:6"
  other  "200-ball_VFBGAold.step_23:7"
  other  "200-ball_VFBGAold.step_23:8"
  other  "200-ball_VFBGAold.step_23:9"
  other  "200-ball_VFBGAold.step_23:10"
  other  "200-ball_VFBGAold.step_23:11"
  other  "200-ball_VFBGAold.step_23:12"
  other  "200-ball_VFBGAold.step_23:13"
  other  "200-ball_VFBGAold.step_23:14"
  other  "200-ball_VFBGAold.step_23:15"
  other  "200-ball_VFBGAold.step_23:16"
  other  "200-ball_VFBGAold.step_23:17"
  other  "200-ball_VFBGAold.step_23:18"
  other  "200-ball_VFBGAold.step_23:19"
  other  "200-ball_VFBGAold.step_23:20"
  other  "200-ball_VFBGAold.step_23:21"
  other  "200-ball_VFBGAold.step_23:22"
  other  "200-ball_VFBGAold.step_23:23"
  other  "200-ball_VFBGAold.step_23:24"
  other  "200-ball_VFBGAold.step_23:25"
  other  "200-ball_VFBGAold.step_23:26"
  other  "200-ball_VFBGAold.step_23:27"
  other  "200-ball_VFBGAold.step_23:28"
  other  "200-ball_VFBGAold.step_23:29"
  other  "200-ball_VFBGAold.step_23:30"
  other  "200-ball_VFBGAold.step_23:31"
  other  "200-ball_VFBGAold.step_23:32"
  other  "200-ball_VFBGAold.step_23:33"
  other  "200-ball_VFBGAold.step_23:34"
  other  "200-ball_VFBGAold.step_23:35"
  other  "200-ball_VFBGAold.step_23:36"
  other  "200-ball_VFBGAold.step_23:37"
  other  "200-ball_VFBGAold.step_23:38"
  other  "200-ball_VFBGAold.step_23:39"
  other  "200-ball_VFBGAold.step_23:40"
  other  "200-ball_VFBGAold.step_23:41"
  other  "200-ball_VFBGAold.step_23:42"
  other  "200-ball_VFBGAold.step_23:43"
  other  "200-ball_VFBGAold.step_23:44"
  other  "200-ball_VFBGAold.step_23:45"
  other  "200-ball_VFBGAold.step_23:46"
  other  "200-ball_VFBGAold.step_23:47"
  other  "200-ball_VFBGAold.step_23:48"
  other  "200-ball_VFBGAold.step_23:49"
  other  "200-ball_VFBGAold.step_23:50"
  other  "200-ball_VFBGAold.step_23:51"
  other  "200-ball_VFBGAold.step_23:52"
  other  "200-ball_VFBGAold.step_23:53"
  other  "200-ball_VFBGAold.step_23:54"
  other  "200-ball_VFBGAold.step_23:55"
  other  "200-ball_VFBGAold.step_23:56"
  other  "200-ball_VFBGAold.step_23:57"
  other  "200-ball_VFBGAold.step_23:58"
  other  "200-ball_VFBGAold.step_23:59"
  other  "200-ball_VFBGAold.step_23:60"
  other  "200-ball_VFBGAold.step_23:61"
  other  "200-ball_VFBGAold.step_23:62"
  other  "200-ball_VFBGAold.step_23:63"
  other  "200-ball_VFBGAold.step_23:64"
  other  "200-ball_VFBGAold.step_23:65"
  other  "200-ball_VFBGAold.step_23:66"
  other  "200-ball_VFBGAold.step_23:67"
  other  "200-ball_VFBGAold.step_23:68"
  other  "200-ball_VFBGAold.step_23:69"
  other  "200-ball_VFBGAold.step_23:70"
  other  "200-ball_VFBGAold.step_23:71"
  other  "200-ball_VFBGAold.step_23:72"
  other  "200-ball_VFBGAold.step_23:73"
  other  "200-ball_VFBGAold.step_23:74"
  other  "200-ball_VFBGAold.step_23:75"
  other  "200-ball_VFBGAold.step_23:76"
  other  "200-ball_VFBGAold.step_23:77"
  other  "200-ball_VFBGAold.step_23:78"
  other  "200-ball_VFBGAold.step_23:79"
  other  "200-ball_VFBGAold.step_23:80"
  other  "200-ball_VFBGAold.step_23:81"
  other  "200-ball_VFBGAold.step_23:82"
  other  "200-ball_VFBGAold.step_23:83"
  other  "200-ball_VFBGAold.step_23:84"
  other  "200-ball_VFBGAold.step_23:85"
  other  "200-ball_VFBGAold.step_23:86"
  other  "200-ball_VFBGAold.step_23:87"
  other  "200-ball_VFBGAold.step_23:88"
  other  "200-ball_VFBGAold.step_23:89"
  other  "200-ball_VFBGAold.step_23:90"
  other  "200-ball_VFBGAold.step_23:91"
  other  "200-ball_VFBGAold.step_23:92"
  other  "200-ball_VFBGAold.step_23:93"
  other  "200-ball_VFBGAold.step_23:94"
  other  "200-ball_VFBGAold.step_23:95"
  other  "200-ball_VFBGAold.step_23:96"
  other  "200-ball_VFBGAold.step_23:97"
  other  "200-ball_VFBGAold.step_23:98"
  other  "200-ball_VFBGAold.step_23:99"
  other  "200-ball_VFBGAold.step_23:100"
  other  "200-ball_VFBGAold.step_23:101"
  other  "200-ball_VFBGAold.step_23:102"
  other  "200-ball_VFBGAold.step_23:103"
  other  "200-ball_VFBGAold.step_23:104"
  other  "200-ball_VFBGAold.step_23:105"
  other  "200-ball_VFBGAold.step_23:106"
  other  "200-ball_VFBGAold.step_23:107"
  other  "200-ball_VFBGAold.step_23:108"
  other  "200-ball_VFBGAold.step_23:109"
  other  "200-ball_VFBGAold.step_23:110"
  other  "200-ball_VFBGAold.step_23:111"
  other  "200-ball_VFBGAold.step_23:112"
  other  "200-ball_VFBGAold.step_23:113"
  other  "200-ball_VFBGAold.step_23:114"
  other  "200-ball_VFBGAold.step_23:115"
  other  "200-ball_VFBGAold.step_23:116"
  other  "200-ball_VFBGAold.step_23:117"
  other  "200-ball_VFBGAold.step_23:118"
  other  "200-ball_VFBGAold.step_23:119"
  other  "200-ball_VFBGAold.step_23:120"
  other  "200-ball_VFBGAold.step_23:121"
  other  "200-ball_VFBGAold.step_23:122"
  other  "200-ball_VFBGAold.step_23:123"
  other  "200-ball_VFBGAold.step_23:124"
  other  "200-ball_VFBGAold.step_23:125"
  other  "200-ball_VFBGAold.step_23:126"
  other  "200-ball_VFBGAold.step_23:127"
  other  "200-ball_VFBGAold.step_23:128"
  other  "200-ball_VFBGAold.step_23:129"
  other  "200-ball_VFBGAold.step_23:130"
  other  "200-ball_VFBGAold.step_23:131"
  other  "200-ball_VFBGAold.step_23:132"
  other  "200-ball_VFBGAold.step_23:133"
  other  "200-ball_VFBGAold.step_23:134"
  other  "200-ball_VFBGAold.step_23:135"
  other  "200-ball_VFBGAold.step_23:136"
  other  "200-ball_VFBGAold.step_23:137"
  other  "200-ball_VFBGAold.step_23:138"
  other  "200-ball_VFBGAold.step_23:139"
  other  "200-ball_VFBGAold.step_23:140"
  other  "200-ball_VFBGAold.step_23:141"
  other  "200-ball_VFBGAold.step_23:142"
  other  "200-ball_VFBGAold.step_23:143"
  other  "200-ball_VFBGAold.step_23:144"
  other  "200-ball_VFBGAold.step_23:145"
  other  "200-ball_VFBGAold.step_23:146"
  other  "200-ball_VFBGAold.step_23:147"
  other  "200-ball_VFBGAold.step_23:148"
  other  "200-ball_VFBGAold.step_23:149"
  other  "200-ball_VFBGAold.step_23:150"
  other  "200-ball_VFBGAold.step_23:151"
  other  "200-ball_VFBGAold.step_23:152"
  other  "200-ball_VFBGAold.step_23:153"
  other  "200-ball_VFBGAold.step_23:154"
  other  "200-ball_VFBGAold.step_23:155"
  other  "200-ball_VFBGAold.step_23:156"
  other  "200-ball_VFBGAold.step_23:157"
  other  "200-ball_VFBGAold.step_23:158"
  other  "200-ball_VFBGAold.step_23:159"
  other  "200-ball_VFBGAold.step_23:160"
  other  "200-ball_VFBGAold.step_23:161"
  other  "200-ball_VFBGAold.step_23:162"
  other  "200-ball_VFBGAold.step_23:163"
  other  "200-ball_VFBGAold.step_23:164"
  other  "200-ball_VFBGAold.step_23:165"
  other  "200-ball_VFBGAold.step_23:166"
  other  "200-ball_VFBGAold.step_23:167"
  other  "200-ball_VFBGAold.step_23:168"
  other  "200-ball_VFBGAold.step_23:169"
  other  "200-ball_VFBGAold.step_23:170"
  other  "200-ball_VFBGAold.step_23:171"
  other  "200-ball_VFBGAold.step_23:172"
  other  "200-ball_VFBGAold.step_23:173"
  other  "200-ball_VFBGAold.step_23:174"
  other  "200-ball_VFBGAold.step_23:175"
  other  "200-ball_VFBGAold.step_23:176"
  other  "200-ball_VFBGAold.step_23:177"
  other  "200-ball_VFBGAold.step_23:178"
  other  "200-ball_VFBGAold.step_23:179"
  other  "200-ball_VFBGAold.step_23:180"
  other  "200-ball_VFBGAold.step_23:181"
  other  "200-ball_VFBGAold.step_23:182"
  other  "200-ball_VFBGAold.step_23:183"
  other  "200-ball_VFBGAold.step_23:184"
  other  "200-ball_VFBGAold.step_23:185"
  other  "200-ball_VFBGAold.step_23:186"
  other  "200-ball_VFBGAold.step_23:187"
  other  "200-ball_VFBGAold.step_23:188"
  other  "200-ball_VFBGAold.step_23:189"
  other  "200-ball_VFBGAold.step_23:190"
  other  "200-ball_VFBGAold.step_23:191"
  other  "200-ball_VFBGAold.step_23:192"
  other  "200-ball_VFBGAold.step_23:193"
  other  "200-ball_VFBGAold.step_23:194"
  other  "200-ball_VFBGAold.step_23:195"
  other  "200-ball_VFBGAold.step_23:196"
  other  "200-ball_VFBGAold.step_23:197"
  other  "200-ball_VFBGAold.step_23:198"
  other  "200-ball_VFBGAold.step_23:199"
  other  "200-ball_VFBGAold.step_23:200"
  other  "200-ball_VFBGAold.step_23:201"
  other  "CAP0201.step_25:1"
  other  "CAP0201.step_27:1"
  other  "CAP0201.step_29:1"
  other  "CAP0201.step_31:1"
  other  "CAP0201.step_33:1"
  other  "CAP0201.step_35:1"
  other  "CAP0201.step_37:1"
  other  "CAP0201.step_39:1"
  other  "CAP0201.step_41:1"
  other  "CAP0201.step_43:1"
  other  "CAP0201.step_45:1"
  other  "CAP0201.step_47:1"
  other  "CAP0201.step_49:1"
  other  "CAP0201.step_51:1"
  other  "CAP0201.step_53:1"
  other  "CAP0201.step_55:1"
  other  "CAP0201.step_57:1"
  other  "CAP0201.step_59:1"
  other  "CAP0201.step_61:1"
  other  "CAP0201.step_63:1"
  other  "CAP0201.step_65:1"
  other  "CAP0201.step_67:1"
  other  "CAP0201.step_69:1"
  other  "CAP0201.step_71:1"
  other  "CAP0201.step_73:1"
  other  "CAP0201.step_75:1"
  other  "CAP0201.step_77:1"
  other  "CAP0201.step_79:1"
  other  "CAP0201.step_81:1"
  other  "CAP0201.step_83:1"
  other  "CAP0201.step_85:1"
  other  "CAP0201.step_87:1"
  other  "CAP0201.step_89:1"
  other  "RES0201old.step_91:1"
  other  "RES0201old.step_91:2"
  other  "RES0201old.step_93:1"
  other  "RES0201old.step_93:2"
  other  "RES0201old.step_95:1"
  other  "RES0201old.step_95:2"
  other  "RES0201old.step_97:1"
  other  "RES0201old.step_97:2"
  other  "RES0201old.step_99:1"
  other  "RES0201old.step_99:2"
  other  "RES0201old.step_101:1"
  other  "RES0201old.step_101:2"
  other  "RES0201old.step_103:1"
  other  "RES0201old.step_103:2"
  other  "RES0201old.step_105:1"
  other  "RES0201old.step_105:2"
  other  "RES0201old.step_107:1"
  other  "RES0201old.step_107:2"
  other  "RES0201old.step_109:1"
  other  "RES0201old.step_109:2"
  other  "RES0201old.step_111:1"
  other  "RES0201old.step_111:2"
  other  "RES0201old.step_113:1"
  other  "RES0201old.step_113:2"
  other  "RES0201old.step_115:1"
  other  "RES0201old.step_115:2"
  other  "RES0201old.step_117:1"
  other  "RES0201old.step_117:2"
  other  "CAP0402.step_119:1"
  other  "CAP0402.step_121:1"
  other  "CAP0402.step_123:1"
  other  "CAP0402.step_125:1"
  other  "CAP0402.step_127:1"
  other  "CAP0402.step_129:1"
  other  "CAP0402.step_131:1"
  other  "CAP0402.step_133:1"
  other  "CAP0402.step_135:1"
  other  "CAP0402.step_137:1"
  other  "CAP0402.step_139:1"
  other  "CAP0402.step_141:1"
  other  "CAP0402.step_143:1"
  other  "CAP0402.step_145:1"
  other  "CAP0402.step_147:1"
  other  "CAP0402.step_149:1"
  other  "CAP0402.step_151:1"
  other  "CAP0402.step_153:1"
  other  "CAP0402.step_155:1"
  other  "CAP0402.step_157:1"
  other  "CAP0402.step_159:1"
  other  "CAP0402.step_161:1"
  other  "PMIC STEP.STEP_163:1"
  other  "3D-SRP201208-R47MH-20230512 .step_165:1"
  other  "3D-SRP201208-R47MH-20230512 .step_165:2"
  other  "3D-SRP201208-R47MH-20230512 .step_165:3"
  other  "3D-SRP201208-R47MH-20230512 .step_167:1"
  other  "3D-SRP201208-R47MH-20230512 .step_167:2"
  other  "3D-SRP201208-R47MH-20230512 .step_167:3"
  other  "3D-SRP201208-R47MH-20230512 .step_169:1"
  other  "3D-SRP201208-R47MH-20230512 .step_169:2"
  other  "3D-SRP201208-R47MH-20230512 .step_169:3"
  other  "3D-SRP201208-R47MH-20230512 .step_171:1"
  other  "3D-SRP201208-R47MH-20230512 .step_171:2"
  other  "3D-SRP201208-R47MH-20230512 .step_171:3"
  other  "3D-SRP201208-R47MH-20230512 .step_173:1"
  other  "3D-SRP201208-R47MH-20230512 .step_173:2"
  other  "3D-SRP201208-R47MH-20230512 .step_173:3"
  other  "3D-SRP201208-R47MH-20230512 .step_175:1"
  other  "3D-SRP201208-R47MH-20230512 .step_175:2"
  other  "3D-SRP201208-R47MH-20230512 .step_175:3"
  other  "3D-SRP201208-R47MH-20230512 .step_177:1"
  other  "3D-SRP201208-R47MH-20230512 .step_177:2"
  other  "3D-SRP201208-R47MH-20230512 .step_177:3"
  other  "body_179:1"
  other  "term2_180:1"
  other  "term1_181:1"
  other  "body_179:2"
  other  "term2_180:2"
  other  "term1_181:2"
  other  "body_179:3"
  other  "term2_180:3"
  other  "term1_181:3"
  other  "body_179:4"
  other  "term2_180:4"
  other  "term1_181:4"
  other  "2712 v2 STEP.STEP_191:1"
  other  "2712 v2 STEP.STEP_191:2"
  other  "2712 v2 STEP.STEP_191:3"
  other  "CAP0603.step_193:1"
  other  "CAP0603.step_195:1"
  other  "CAP0603.step_197:1"
  other  "CAP0603.step_199:1"
  other  "RES0402.step_201:1"
  other  "RES0402.step_201:2"
  other  "RES0402.step_201:3"
  other  "RES0402.step_201:4"
  other  "RES0402.step_203:1"
  other  "RES0402.step_203:2"
  other  "RES0402.step_203:3"
  other  "RES0402.step_203:4"
  other  "RES0402.step_205:1"
  other  "RES0402.step_205:2"
  other  "RES0402.step_205:3"
  other  "RES0402.step_205:4"
  other  "RES0402.step_207:1"
  other  "RES0402.step_207:2"
  other  "RES0402.step_207:3"
  other  "RES0402.step_207:4"
  other  "RES0402.step_209:1"
  other  "RES0402.step_209:2"
  other  "RES0402.step_209:3"
  other  "RES0402.step_209:4"
  other  "RES0402.step_211:1"
  other  "RES0402.step_211:2"
  other  "RES0402.step_211:3"
  other  "RES0402.step_211:4"
  other  "RES0402.step_213:1"
  other  "RES0402.step_213:2"
  other  "RES0402.step_213:3"
  other  "RES0402.step_213:4"
  other  "RES0402.step_215:1"
  other  "RES0402.step_215:2"
  other  "RES0402.step_215:3"
  other  "RES0402.step_215:4"
  other  "RES0402.step_217:1"
  other  "RES0402.step_217:2"
  other  "RES0402.step_217:3"
  other  "RES0402.step_217:4"
  other  "RES0402.step_219:1"
  other  "RES0402.step_219:2"
  other  "RES0402.step_219:3"
  other  "RES0402.step_219:4"
  other  "CAP0201.step_221:1"
  other  "CAP0201.step_223:1"
  other  "CAP0201.step_225:1"
  other  "CAP0201.step_227:1"
  other  "CAP0201.step_229:1"
  other  "CAP0201.step_231:1"
  other  "SOT883B Mold body_233:1"
  other  "SOT883B4 LF_234:1"
  other  "SOT883B4 LF_234:2"
  other  "SOT883B4 LF_234:3"
  other  "SOT883B4 LF_234:4"
  other  "SOT883B4 LF_234:5"
  other  "SOT883B4 LF_234:6"
  other  "SOT883B4 LF_234:7"
  other  "SOT883B4 LF_234:8"
  other  "SOT883B4 LF_234:9"
  other  "SOT883B4 LF_234:10"
  other  "SOT883B4 LF_234:11"
  other  "SOT883B4 LF_234:12"
  other  "SOT883B4 LF_234:13"
  other  "SOT883B Mold body_233:2"
  other  "SOT883B4 LF_234:14"
  other  "SOT883B4 LF_234:15"
  other  "SOT883B4 LF_234:16"
  other  "SOT883B4 LF_234:17"
  other  "SOT883B4 LF_234:18"
  other  "SOT883B4 LF_234:19"
  other  "SOT883B4 LF_234:20"
  other  "SOT883B4 LF_234:21"
  other  "SOT883B4 LF_234:22"
  other  "SOT883B4 LF_234:23"
  other  "SOT883B4 LF_234:24"
  other  "SOT883B4 LF_234:25"
  other  "SOT883B4 LF_234:26"
  other  "ProjectY v3 STEP.STEP_242:1"
  other  "(Unsaved)_244:1"
  other  "(Unsaved)_244:2"
  other  "(Unsaved)_244:3"
  other  "(Unsaved)_244:4"
  other  "(Unsaved)_244:5"
  other  "(Unsaved)_244:6"
  other  "(Unsaved)_244:7"
  other  "(Unsaved)_244:8"
  other  "(Unsaved)_244:9"
  other  "(Unsaved)_244:10"
  other  "(Unsaved)_244:11"
  other  "(Unsaved)_244:12"
  other  "(Unsaved)_244:13"
  other  "(Unsaved)_244:14"
  other  "(Unsaved)_244:15"
  other  "(Unsaved)_244:16"
  other  "(Unsaved)_244:17"
  other  "(Unsaved)_244:18"
  other  "(Unsaved)_244:19"
  other  "(Unsaved)_244:20"
  other  "(Unsaved)_244:21"
  other  "(Unsaved)_244:22"
  other  "(Unsaved)_244:23"
  other  "(Unsaved)_244:24"
  other  "(Unsaved)_244:25"
  other  "(Unsaved)_244:26"
  other  "(Unsaved)_244:27"
  other  "(Unsaved)_244:28"
  other  "(Unsaved)_244:29"
  other  "(Unsaved)_244:30"
  other  "(Unsaved)_244:31"
  other  "(Unsaved)_244:32"
  other  "(Unsaved)_244:33"
  other  "(Unsaved)_244:34"
  other  "(Unsaved)_244:35"
  other  "(Unsaved)_244:36"
  other  "(Unsaved)_244:37"
  other  "(Unsaved)_244:38"
  other  "(Unsaved)_244:39"
  other  "(Unsaved)_244:40"
  other  "(Unsaved)_244:41"
  other  "(Unsaved)_244:42"
  other  "(Unsaved)_244:43"
  other  "(Unsaved)_244:44"
  other  "(Unsaved)_244:45"
  other  "(Unsaved)_244:46"
  other  "(Unsaved)_244:47"
  other  "(Unsaved)_244:48"
  other  "(Unsaved)_244:49"
  other  "(Unsaved)_244:50"
  other  "(Unsaved)_244:51"
  other  "Box_246:1"
  other  "Box_246:2"
  other  "Fusion_248:1"
  other  "CAP0201.step_253:1"
  other  "CAP0201.step_255:1"
  other  "CAP0201.step_257:1"
  other  "CAP0201.step_259:1"
  other  "CAP0201.step_261:1"
  other  "CAP0201.step_263:1"
  other  "CAP0201.step_265:1"
  other  "CAP0201.step_267:1"
  other  "CAP0201.step_269:1"
  other  "CAP0201.step_271:1"
  other  "CAP0201.step_273:1"
  other  "CAP0201.step_275:1"
  other  "CAP0201.step_277:1"
  other  "CAP0201.step_279:1"
  other  "CAP0201.step_281:1"
  other  "CAP0201.step_283:1"
  other  "CAP0201.step_285:1"
  other  "CAP0201.step_287:1"
  other  "CAP0201.step_289:1"
  other  "CAP0201.step_291:1"
  other  "CAP0201.step_293:1"
  other  "CAP0201.step_295:1"
  other  "CAP0201.step_297:1"
  other  "CAP0201.step_299:1"
  other  "CAP0201.step_301:1"
  other  "CAP0201.step_303:1"
  other  "CAP0201.step_305:1"
  other  "CAP0201.step_307:1"
  other  "CAP0201.step_309:1"
  other  "CAP0201.step_311:1"
  other  "CAP0201.step_313:1"
  other  "CAP0201.step_315:1"
  other  "CAP0201.step_317:1"
  other  "CAP0201.step_319:1"
  other  "CAP0201.step_321:1"
  other  "CAP0201.step_323:1"
  other  "CAP0201.step_325:1"
  other  "CAP0201.step_327:1"
  other  "CAP0201.step_329:1"
  other  "CAP0201.step_331:1"
  other  "CAP0201.step_333:1"
  other  "CAP0201.step_335:1"
  other  "CAP0201.step_337:1"
  other  "CAP0201.step_339:1"
  other  "CAP0201.step_341:1"
  other  "CAP0201.step_343:1"
  other  "CAP0201.step_345:1"
  other  "CAP0201.step_347:1"
  other  "CAP0201.step_349:1"
  other  "CAP0201.step_351:1"
  other  "CAP0201.step_353:1"
  other  "CAP0201.step_355:1"
  other  "CAP0201.step_357:1"
  other  "CAP0201.step_359:1"
  other  "CAP0201.step_361:1"
  other  "CAP0201.step_363:1"
  other  "CAP0201.step_365:1"
  other  "CAP0201.step_367:1"
  other  "CAP0201.step_369:1"
  other  "CAP0201.step_371:1"
  other  "CAP0201.step_373:1"
  other  "CAP0201.step_375:1"
  other  "CAP0201.step_377:1"
  other  "CAP0201.step_379:1"
  other  "CAP0201.step_381:1"
  other  "CAP0201.step_383:1"
  other  "CAP0201.step_385:1"
  other  "CAP0201.step_387:1"
  other  "CAP0201.step_389:1"
  other  "CAP0201.step_391:1"
  other  "CAP0201.step_393:1"
  other  "CAP0201.step_395:1"
  other  "CAP0201.step_397:1"
  other  "CAP0201.step_399:1"
  other  "CAP0201.step_401:1"
  other  "CAP0201.step_403:1"
  other  "CAP0201.step_405:1"
  other  "CAP0201.step_407:1"
  other  "CAP0201.step_409:1"
  other  "CAP0201.step_411:1"
  other  "CAP0201.step_413:1"
  other  "CAP0201.step_415:1"
  other  "CAP0201.step_417:1"
  other  "CAP0201.step_419:1"
  other  "CAP0201.step_421:1"
  other  "CAP0201.step_423:1"
  other  "CAP0201.step_425:1"
  other  "CAP0201.step_427:1"
  other  "CAP0201.step_429:1"
  other  "CAP0201.step_431:1"
  other  "CAP0201.step_433:1"
  other  "CAP0201.step_435:1"
  other  "CAP0201.step_437:1"
  other  "CAP0201.step_439:1"
  other  "CAP0201.step_441:1"
  other  "CAP0201.step_443:1"
  other  "CAP0201.step_445:1"
  other  "CAP0201.step_447:1"
  other  "CAP0201.step_449:1"
  other  "CAP0201.step_451:1"
  other  "CAP0201.step_453:1"
  other  "CAP0201.step_455:1"
  other  "CAP0201.step_457:1"
  other  "CAP0201.step_459:1"
  other  "CAP0201.step_461:1"
  other  "CAP0201.step_463:1"
  other  "CAP0201.step_465:1"
  other  "CAP0201.step_467:1"
  other  "CAP0201.step_469:1"
  other  "CAP0201.step_471:1"
  other  "CAP0201.step_473:1"
  other  "CAP0201.step_475:1"
  other  "CAP0201.step_477:1"
  other  "CAP0201.step_479:1"
  other  "CAP0201.step_481:1"
  other  "CAP0201.step_483:1"
  other  "CAP0201.step_485:1"
  other  "CAP0201.step_487:1"
  other  "CAP0201.step_489:1"
  other  "CAP0201.step_491:1"
  other  "CAP0201.step_493:1"
  other  "CAP0201.step_495:1"
  other  "CAP0201.step_497:1"
  other  "CAP0201.step_499:1"
  other  "CAP0201.step_501:1"
  other  "CAP0201.step_503:1"
  other  "CAP0201.step_505:1"
  other  "CAP0201.step_507:1"
  other  "CAP0201.step_509:1"
  other  "CAP0201.step_511:1"
  other  "CAP0201.step_513:1"
  other  "CAP0201.step_515:1"
  other  "CAP0201.step_517:1"
  other  "CAP0201.step_519:1"
  other  "CAP0201.step_521:1"
  other  "CAP0201.step_523:1"
  other  "CAP0201.step_525:1"
  other  "CAP0201.step_527:1"
  other  "CAP0201.step_529:1"
  other  "CAP0201.step_531:1"
  other  "CAP0201.step_533:1"
  other  "CAP0201.step_535:1"
  other  "CAP0201.step_537:1"
  other  "CAP0201.step_539:1"
  other  "CAP0201.step_541:1"
  other  "CAP0201.step_543:1"
  other  "CAP0201.step_545:1"
  other  "CAP0201.step_547:1"
  other  "CAP0201.step_549:1"
  other  "CAP0201.step_551:1"
  other  "CAP0201.step_553:1"
  other  "RES0201old.step_555:1"
  other  "RES0201old.step_555:2"
  other  "RES0201old.step_557:1"
  other  "RES0201old.step_557:2"
  other  "RES0201old.step_559:1"
  other  "RES0201old.step_559:2"
  other  "RES0201old.step_561:1"
  other  "RES0201old.step_561:2"
  other  "RES0201old.step_563:1"
  other  "RES0201old.step_563:2"
  other  "RES0201old.step_565:1"
  other  "RES0201old.step_565:2"
  other  "RES0201old.step_567:1"
  other  "RES0201old.step_567:2"
  other  "RES0201old.step_569:1"
  other  "RES0201old.step_569:2"
  other  "RES0201old.step_571:1"
  other  "RES0201old.step_571:2"
  other  "RES0201old.step_573:1"
  other  "RES0201old.step_573:2"
  other  "RES0201old.step_575:1"
  other  "RES0201old.step_575:2"
  other  "RES0201old.step_577:1"
  other  "RES0201old.step_577:2"
  other  "RES0201old.step_579:1"
  other  "RES0201old.step_579:2"
  other  "RES0201old.step_581:1"
  other  "RES0201old.step_581:2"
  other  "RES0201old.step_583:1"
  other  "RES0201old.step_583:2"
  other  "RES0201old.step_585:1"
  other  "RES0201old.step_585:2"
  other  "RES0201old.step_587:1"
  other  "RES0201old.step_587:2"
  other  "RES0201old.step_589:1"
  other  "RES0201old.step_589:2"
  other  "RES0201old.step_591:1"
  other  "RES0201old.step_591:2"
  other  "RES0201old.step_593:1"
  other  "RES0201old.step_593:2"
  other  "RES0201old.step_595:1"
  other  "RES0201old.step_595:2"
  other  "RES0201old.step_597:1"
  other  "RES0201old.step_597:2"
  other  "RES0201old.step_599:1"
  other  "RES0201old.step_599:2"
  other  "RES0201old.step_601:1"
  other  "RES0201old.step_601:2"
  other  "RES0201old.step_603:1"
  other  "RES0201old.step_603:2"
  other  "RES0201old.step_605:1"
  other  "RES0201old.step_605:2"
  other  "RES0201old.step_607:1"
  other  "RES0201old.step_607:2"
  other  "RES0201old.step_609:1"
  other  "RES0201old.step_609:2"
  other  "RES0201old.step_611:1"
  other  "RES0201old.step_611:2"
  other  "RES0201old.step_613:1"
  other  "RES0201old.step_613:2"
  other  "RES0201old.step_615:1"
  other  "RES0201old.step_615:2"
  other  "RES0201old.step_617:1"
  other  "RES0201old.step_617:2"
  other  "RES0201old.step_619:1"
  other  "RES0201old.step_619:2"
  other  "RES0201old.step_621:1"
  other  "RES0201old.step_621:2"
  other  "RES0201old.step_623:1"
  other  "RES0201old.step_623:2"
  other  "RES0201old.step_625:1"
  other  "RES0201old.step_625:2"
  other  "RES0201old.step_627:1"
  other  "RES0201old.step_627:2"
  other  "RES0201old.step_629:1"
  other  "RES0201old.step_629:2"
  other  "RES0201old.step_631:1"
  other  "RES0201old.step_631:2"
  other  "RES0201old.step_633:1"
  other  "RES0201old.step_633:2"
  other  "RES0201old.step_635:1"
  other  "RES0201old.step_635:2"
  other  "RES0201old.step_637:1"
  other  "RES0201old.step_637:2"
  other  "RES0201old.step_639:1"
  other  "RES0201old.step_639:2"
  other  "RES0201old.step_641:1"
  other  "RES0201old.step_641:2"
  other  "RES0201old.step_643:1"
  other  "RES0201old.step_643:2"
  other  "RES0201old.step_645:1"
  other  "RES0201old.step_645:2"
  other  "RES0201old.step_647:1"
  other  "RES0201old.step_647:2"
  other  "RES0201old.step_649:1"
  other  "RES0201old.step_649:2"
  other  "RES0201old.step_651:1"
  other  "RES0201old.step_651:2"
  other  "RES0201old.step_653:1"
  other  "RES0201old.step_653:2"
  other  "RES0201old.step_655:1"
  other  "RES0201old.step_655:2"
  other  "RES0201old.step_657:1"
  other  "RES0201old.step_657:2"
  other  "RES0201old.step_659:1"
  other  "RES0201old.step_659:2"
  other  "RES0201old.step_661:1"
  other  "RES0201old.step_661:2"
  other  "RES0201old.step_663:1"
  other  "RES0201old.step_663:2"
  other  "RES0201old.step_665:1"
  other  "RES0201old.step_665:2"
  other  "RES0201old.step_667:1"
  other  "RES0201old.step_667:2"
  other  "PinIndicator_669:1"
  other  "Pads_670:1"
  other  "Lid_671:1"
  other  "Body_672:1"
  other  "Pad001_676:1"
  other  "Cut_677:1"
  other  "Cut_677:2"
  other  "Pad001_676:2"
  other  "Cut_677:3"
  other  "Cut_677:4"
  other  "Pad001_676:3"
  other  "Cut_677:5"
  other  "Cut_677:6"
  other  "Pad001_676:4"
  other  "Cut_677:7"
  other  "Cut_677:8"
  other  "Pad001_676:5"
  other  "Cut_677:9"
  other  "Cut_677:10"
  other  "Pad001_676:6"
  other  "Cut_677:11"
  other  "Cut_677:12"
  other  "Pad001_676:7"
  other  "Cut_677:13"
  other  "Cut_677:14"
  other  "Pad001_676:8"
  other  "Cut_677:15"
  other  "Cut_677:16"
  other  "Pad001_676:9"
  other  "Cut_677:17"
  other  "Cut_677:18"
  other  "Pad001_676:10"
  other  "Cut_677:19"
  other  "Cut_677:20"
  other  "Pad001_676:11"
  other  "Cut_677:21"
  other  "Cut_677:22"
  other  "Pad001_676:12"
  other  "Cut_677:23"
  other  "Cut_677:24"
  other  "Pad001_676:13"
  other  "Cut_677:25"
  other  "Cut_677:26"
  other  "Pad001_676:14"
  other  "Cut_677:27"
  other  "Cut_677:28"
  other  "Pad001_676:15"
  other  "Cut_677:29"
  other  "Cut_677:30"
  other  "Pad001_676:16"
  other  "Cut_677:31"
  other  "Cut_677:32"
  other  "Pad001_676:17"
  other  "Cut_677:33"
  other  "Cut_677:34"
  other  "Pad001_676:18"
  other  "Cut_677:35"
  other  "Cut_677:36"
  other  "Pad001_676:19"
  other  "Cut_677:37"
  other  "Cut_677:38"
  other  "Pad001_676:20"
  other  "Cut_677:39"
  other  "Cut_677:40"
  other  "Pad001_676:21"
  other  "Cut_677:41"
  other  "Cut_677:42"
  other  "Pad001_676:22"
  other  "Cut_677:43"
  other  "Cut_677:44"
  other  "CAP0402.step_723:1"
  other  "CAP0402.step_725:1"
  other  "CAP0402.step_727:1"
  other  "CAP0402.step_729:1"
  other  "CAP0402.step_731:1"
  other  "CAP0402.step_733:1"
  other  "CAP0402.step_735:1"
  other  "CAP0402.step_737:1"
  other  "CAP0402.step_739:1"
  other  "CAP0402.step_741:1"
  other  "CAP0402.step_743:1"
  other  "CAP0402.step_745:1"
  other  "CAP0402.step_747:1"
  other  "CAP0402.step_749:1"
  other  "CAP0402.step_751:1"
  other  "CAP0402.step_753:1"
  other  "CAP0402.step_755:1"
  other  "CAP0402.step_757:1"
  other  "CAP0402.step_759:1"
  other  "CAP0402.step_761:1"
  other  "CAP0402.step_763:1"
  other  "CAP0402.step_765:1"
  other  "CAP0402.step_767:1"
  other  "CAP0402.step_769:1"
  other  "CAP0402.step_771:1"
  other  "CAP0402.step_773:1"
  other  "CAP0402.step_775:1"
  other  "CAP0402.step_777:1"
  other  "CAP0402.step_779:1"
  other  "CAP0402.step_781:1"
  other  "CAP0402.step_783:1"
  other  "CAP0402.step_785:1"
  other  "CAP0402.step_787:1"
  other  "CAP0402.step_789:1"
  other  "CAP0402.step_791:1"
  other  "CAP0402.step_793:1"
  other  "CAP0402.step_795:1"
  other  "CAP0402.step_797:1"
  other  "CAP0402.step_799:1"
  other  "CAP0402.step_801:1"
  other  "CAP0402.step_803:1"
  other  "CAP0402.step_805:1"
  other  "CAP0402.step_807:1"
  other  "CAP0402.step_809:1"
  other  "CAP0402.step_811:1"
  other  "CAP0402.step_813:1"
  other  "CAP0402.step_815:1"
  other  "CAP0402.step_817:1"
  other  "CAP0402.step_819:1"
  other  "CAP0402.step_821:1"
  other  "CAP0402.step_823:1"
  other  "CAP0402.step_825:1"
  other  "CAP0402.step_827:1"
  other  "CAP0402.step_829:1"
  other  "CAP0402.step_831:1"
  other  "CAP0402.step_833:1"
  other  "CAP0402.step_835:1"
  other  "CAP0402.step_837:1"
  other  "CAP0402.step_839:1"
  other  "Plating_841:1"
  other  "Plating_841:2"
  other  "Plating_841:3"
  other  "Plating_841:4"
  other  "Plating_841:5"
  other  "LDF_842:1"
  other  "LDF_842:2"
  other  "LDF_842:3"
  other  "LDF_842:4"
  other  "LDF_842:5"
  other  "CPD_843:1"
  other  "Pads_847:1"
  other  "Lid_848:1"
  other  "Body_849:1"
  other  "Pins_853:1"
  other  "Pins_853:2"
  other  "Pins_853:3"
  other  "Pins_853:4"
  other  "Pins_853:5"
  other  "Pins_853:6"
  other  "Pins_853:7"
  other  "Pins_853:8"
  other  "Body_854:1"
  other  "CAP0603.step_858:1"
  other  "CAP0603.step_860:1"
  other  "CAP0603.step_862:1"
  other  "CAP0603.step_864:1"
  other  "CAP0603.step_866:1"
  other  "CAP0603.step_868:1"
  other  "Part_18370_870:1"
  other  "Part_739_871:1"
  other  "Part_740_872:1"
  other  "Part_665_873:1"
  other  "Part_637_874:1"
  other  "Part_609_875:1"
  other  "Part_581_876:1"
  other  "Part_553_877:1"
  other  "Part_525_878:1"
  other  "Part_496_879:1"
  other  "SOT883B Mold body_233:3"
  other  "SOT883B4 LF_234:27"
  other  "SOT883B4 LF_234:28"
  other  "SOT883B4 LF_234:29"
  other  "SOT883B4 LF_234:30"
  other  "SOT883B4 LF_234:31"
  other  "SOT883B4 LF_234:32"
  other  "SOT883B4 LF_234:33"
  other  "SOT883B4 LF_234:34"
  other  "SOT883B4 LF_234:35"
  other  "SOT883B4 LF_234:36"
  other  "SOT883B4 LF_234:37"
  other  "SOT883B4 LF_234:38"
  other  "SOT883B4 LF_234:39"
  other  "SOT883B Mold body_233:4"
  other  "SOT883B4 LF_234:40"
  other  "SOT883B4 LF_234:41"
  other  "SOT883B4 LF_234:42"
  other  "SOT883B4 LF_234:43"
  other  "SOT883B4 LF_234:44"
  other  "SOT883B4 LF_234:45"
  other  "SOT883B4 LF_234:46"
  other  "SOT883B4 LF_234:47"
  other  "SOT883B4 LF_234:48"
  other  "SOT883B4 LF_234:49"
  other  "SOT883B4 LF_234:50"
  other  "SOT883B4 LF_234:51"
  other  "SOT883B4 LF_234:52"
  other  "User Library-153BallWFBGA_887:1"
  other  "User Library-153BallWFBGA_887:2"
  other  "User Library-153BallWFBGA_887:3"
  other  "User Library-153BallWFBGA_887:4"
  other  "User Library-153BallWFBGA_887:5"
  other  "User Library-153BallWFBGA_887:6"
  other  "User Library-153BallWFBGA_887:7"
  other  "User Library-153BallWFBGA_887:8"
  other  "User Library-153BallWFBGA_887:9"
  other  "User Library-153BallWFBGA_887:10"
  other  "User Library-153BallWFBGA_887:11"
  other  "User Library-153BallWFBGA_887:12"
  other  "User Library-153BallWFBGA_887:13"
  other  "User Library-153BallWFBGA_887:14"
  other  "User Library-153BallWFBGA_887:15"
  other  "User Library-153BallWFBGA_887:16"
  other  "User Library-153BallWFBGA_887:17"
  other  "User Library-153BallWFBGA_887:18"
  other  "User Library-153BallWFBGA_887:19"
  other  "User Library-153BallWFBGA_887:20"
  other  "User Library-153BallWFBGA_887:21"
  other  "User Library-153BallWFBGA_887:22"
  other  "User Library-153BallWFBGA_887:23"
  other  "User Library-153BallWFBGA_887:24"
  other  "User Library-153BallWFBGA_887:25"
  other  "User Library-153BallWFBGA_887:26"
  other  "User Library-153BallWFBGA_887:27"
  other  "User Library-153BallWFBGA_887:28"
  other  "User Library-153BallWFBGA_887:29"
  other  "User Library-153BallWFBGA_887:30"
  other  "User Library-153BallWFBGA_887:31"
  other  "User Library-153BallWFBGA_887:32"
  other  "User Library-153BallWFBGA_887:33"
  other  "User Library-153BallWFBGA_887:34"
  other  "User Library-153BallWFBGA_887:35"
  other  "User Library-153BallWFBGA_887:36"
  other  "User Library-153BallWFBGA_887:37"
  other  "User Library-153BallWFBGA_887:38"
  other  "User Library-153BallWFBGA_887:39"
  other  "User Library-153BallWFBGA_887:40"
  other  "User Library-153BallWFBGA_887:41"
  other  "User Library-153BallWFBGA_887:42"
  other  "User Library-153BallWFBGA_887:43"
  other  "User Library-153BallWFBGA_887:44"
  other  "User Library-153BallWFBGA_887:45"
  other  "User Library-153BallWFBGA_887:46"
  other  "User Library-153BallWFBGA_887:47"
  other  "User Library-153BallWFBGA_887:48"
  other  "User Library-153BallWFBGA_887:49"
  other  "User Library-153BallWFBGA_887:50"
  other  "User Library-153BallWFBGA_887:51"
  other  "User Library-153BallWFBGA_887:52"
  other  "User Library-153BallWFBGA_887:53"
  other  "User Library-153BallWFBGA_887:54"
  other  "User Library-153BallWFBGA_887:55"
  other  "User Library-153BallWFBGA_887:56"
  other  "User Library-153BallWFBGA_887:57"
  other  "User Library-153BallWFBGA_887:58"
  other  "User Library-153BallWFBGA_887:59"
  other  "User Library-153BallWFBGA_887:60"
  other  "User Library-153BallWFBGA_887:61"
  other  "User Library-153BallWFBGA_887:62"
  other  "User Library-153BallWFBGA_887:63"
  other  "User Library-153BallWFBGA_887:64"
  other  "User Library-153BallWFBGA_887:65"
  other  "User Library-153BallWFBGA_887:66"
  other  "User Library-153BallWFBGA_887:67"
  other  "User Library-153BallWFBGA_887:68"
  other  "User Library-153BallWFBGA_887:69"
  other  "User Library-153BallWFBGA_887:70"
  other  "User Library-153BallWFBGA_887:71"
  other  "User Library-153BallWFBGA_887:72"
  other  "User Library-153BallWFBGA_887:73"
  other  "User Library-153BallWFBGA_887:74"
  other  "User Library-153BallWFBGA_887:75"
  other  "User Library-153BallWFBGA_887:76"
  other  "User Library-153BallWFBGA_887:77"
  other  "User Library-153BallWFBGA_887:78"
  other  "User Library-153BallWFBGA_887:79"
  other  "User Library-153BallWFBGA_887:80"
  other  "User Library-153BallWFBGA_887:81"
  other  "User Library-153BallWFBGA_887:82"
  other  "User Library-153BallWFBGA_887:83"
  other  "User Library-153BallWFBGA_887:84"
  other  "User Library-153BallWFBGA_887:85"
  other  "User Library-153BallWFBGA_887:86"
  other  "User Library-153BallWFBGA_887:87"
  other  "User Library-153BallWFBGA_887:88"
  other  "User Library-153BallWFBGA_887:89"
  other  "User Library-153BallWFBGA_887:90"
  other  "User Library-153BallWFBGA_887:91"
  other  "User Library-153BallWFBGA_887:92"
  other  "User Library-153BallWFBGA_887:93"
  other  "User Library-153BallWFBGA_887:94"
  other  "User Library-153BallWFBGA_887:95"
  other  "User Library-153BallWFBGA_887:96"
  other  "User Library-153BallWFBGA_887:97"
  other  "User Library-153BallWFBGA_887:98"
  other  "User Library-153BallWFBGA_887:99"
  other  "User Library-153BallWFBGA_887:100"
  other  "User Library-153BallWFBGA_887:101"
  other  "User Library-153BallWFBGA_887:102"
  other  "User Library-153BallWFBGA_887:103"
  other  "User Library-153BallWFBGA_887:104"
  other  "User Library-153BallWFBGA_887:105"
  other  "User Library-153BallWFBGA_887:106"
  other  "User Library-153BallWFBGA_887:107"
  other  "User Library-153BallWFBGA_887:108"
  other  "User Library-153BallWFBGA_887:109"
  other  "User Library-153BallWFBGA_887:110"
  other  "User Library-153BallWFBGA_887:111"
  other  "User Library-153BallWFBGA_887:112"
  other  "User Library-153BallWFBGA_887:113"
  other  "User Library-153BallWFBGA_887:114"
  other  "User Library-153BallWFBGA_887:115"
  other  "User Library-153BallWFBGA_887:116"
  other  "User Library-153BallWFBGA_887:117"
  other  "User Library-153BallWFBGA_887:118"
  other  "User Library-153BallWFBGA_887:119"
  other  "User Library-153BallWFBGA_887:120"
  other  "User Library-153BallWFBGA_887:121"
  other  "User Library-153BallWFBGA_887:122"
  other  "User Library-153BallWFBGA_887:123"
  other  "User Library-153BallWFBGA_887:124"
  other  "User Library-153BallWFBGA_887:125"
  other  "User Library-153BallWFBGA_887:126"
  other  "User Library-153BallWFBGA_887:127"
  other  "User Library-153BallWFBGA_887:128"
  other  "User Library-153BallWFBGA_887:129"
  other  "User Library-153BallWFBGA_887:130"
  other  "User Library-153BallWFBGA_887:131"
  other  "User Library-153BallWFBGA_887:132"
  other  "User Library-153BallWFBGA_887:133"
  other  "User Library-153BallWFBGA_887:134"
  other  "User Library-153BallWFBGA_887:135"
  other  "User Library-153BallWFBGA_887:136"
  other  "User Library-153BallWFBGA_887:137"
  other  "User Library-153BallWFBGA_887:138"
  other  "User Library-153BallWFBGA_887:139"
  other  "User Library-153BallWFBGA_887:140"
  other  "User Library-153BallWFBGA_887:141"
  other  "User Library-153BallWFBGA_887:142"
  other  "User Library-153BallWFBGA_887:143"
  other  "User Library-153BallWFBGA_887:144"
  other  "User Library-153BallWFBGA_887:145"
  other  "User Library-153BallWFBGA_887:146"
  other  "User Library-153BallWFBGA_887:147"
  other  "User Library-153BallWFBGA_887:148"
  other  "User Library-153BallWFBGA_887:149"
  other  "User Library-153BallWFBGA_887:150"
  other  "User Library-153BallWFBGA_887:151"
  other  "User Library-153BallWFBGA_887:152"
  other  "User Library-153BallWFBGA_887:153"
  other  "User Library-153BallWFBGA_887:154"
  other  "User Library-153BallWFBGA_887:155"
  other  "User Library-153BallWFBGA_887:156"
  other  "10164228-1001A1RLF.stp_889:1"
  other  "10164228-1001A1RLF.stp_891:1"
  other  "ABM11-0022-T3.step_893:1"
  other  "ABM11-0022-T3.step_895:1"
  other  "DIELECTRIC_Model_1_Inst_899:1"
  other  "User Library-User Library-res0402_res0402_body_903:1"
  other  "User Library-User Library-res0402_res0402_body_905:1"
  other  "User Library-Chip Cap_MLCC_0402 (1005)_907:1"
  other  "User Library-Chip Cap_MLCC_0402 (1005)_909:1"
  other  "User Library-Chip Cap_MLCC_0402 (1005)_911:1"
  other  "User Library-Chip Cap_MLCC_0402 (1005)_913:1"
  other  "User Library-Chip Cap_MLCC_0402 (1005)_915:1"
  other  "User Library-Chip Cap_MLCC_0402 (1005)_917:1"
  other  "User Library-WS2812-4020_919:1"
  other  "User Library-WS2812-4020_919:2"
  other  "User Library-WS2812-4020_919:3"
  other  "User Library-WS2812-4020_919:4"
  other  "User Library-WS2812-4020_919:5"
  other  "User Library-WS2812-4020_919:6"
  other  "User Library-WS2812-4020_919:7"
  other  "User Library-WS2812-4020_919:8"
  other  "User Library-WS2812-4020_919:9"
  other  "User Library-WS2812-4020_919:10"
  other  "User Library-WS2812-4020_921:1"
  other  "User Library-WS2812-4020_921:2"
  other  "User Library-WS2812-4020_921:3"
  other  "User Library-WS2812-4020_921:4"
  other  "User Library-WS2812-4020_921:5"
  other  "User Library-WS2812-4020_921:6"
  other  "User Library-WS2812-4020_921:7"
  other  "User Library-WS2812-4020_921:8"
  other  "User Library-WS2812-4020_921:9"
  other  "User Library-WS2812-4020_921:10"
  other  "User Library-WS2812-4020_923:1"
  other  "User Library-WS2812-4020_923:2"
  other  "User Library-WS2812-4020_923:3"
  other  "User Library-WS2812-4020_923:4"
  other  "User Library-WS2812-4020_923:5"
  other  "User Library-WS2812-4020_923:6"
  other  "User Library-WS2812-4020_923:7"
  other  "User Library-WS2812-4020_923:8"
  other  "User Library-WS2812-4020_923:9"
  other  "User Library-WS2812-4020_923:10"
  other  "User Library-WS2812-4020_925:1"
  other  "User Library-WS2812-4020_925:2"
  other  "User Library-WS2812-4020_925:3"
  other  "User Library-WS2812-4020_925:4"
  other  "User Library-WS2812-4020_925:5"
  other  "User Library-WS2812-4020_925:6"
  other  "User Library-WS2812-4020_925:7"
  other  "User Library-WS2812-4020_925:8"
  other  "User Library-WS2812-4020_925:9"
  other  "User Library-WS2812-4020_925:10"
  other  "User Library-WS2812-4020_927:1"
  other  "User Library-WS2812-4020_927:2"
  other  "User Library-WS2812-4020_927:3"
  other  "User Library-WS2812-4020_927:4"
  other  "User Library-WS2812-4020_927:5"
  other  "User Library-WS2812-4020_927:6"
  other  "User Library-WS2812-4020_927:7"
  other  "User Library-WS2812-4020_927:8"
  other  "User Library-WS2812-4020_927:9"
  other  "User Library-WS2812-4020_927:10"
  other  "User Library-WS2812-4020_929:1"
  other  "User Library-WS2812-4020_929:2"
  other  "User Library-WS2812-4020_929:3"
  other  "User Library-WS2812-4020_929:4"
  other  "User Library-WS2812-4020_929:5"
  other  "User Library-WS2812-4020_929:6"
  other  "User Library-WS2812-4020_929:7"
  other  "User Library-WS2812-4020_929:8"
  other  "User Library-WS2812-4020_929:9"
  other  "User Library-WS2812-4020_929:10"
  other  "User Library-WS2812-4020_931:1"
  other  "User Library-WS2812-4020_931:2"
  other  "User Library-WS2812-4020_931:3"
  other  "User Library-WS2812-4020_931:4"
  other  "User Library-WS2812-4020_931:5"
  other  "User Library-WS2812-4020_931:6"
  other  "User Library-WS2812-4020_931:7"
  other  "User Library-WS2812-4020_931:8"
  other  "User Library-WS2812-4020_931:9"
  other  "User Library-WS2812-4020_931:10"
  other  "User Library-WS2812-4020_933:1"
  other  "User Library-WS2812-4020_933:2"
  other  "User Library-WS2812-4020_933:3"
  other  "User Library-WS2812-4020_933:4"
  other  "User Library-WS2812-4020_933:5"
  other  "User Library-WS2812-4020_933:6"
  other  "User Library-WS2812-4020_933:7"
  other  "User Library-WS2812-4020_933:8"
  other  "User Library-WS2812-4020_933:9"
  other  "User Library-WS2812-4020_933:10"
  other  "User Library-WS2812-4020_935:1"
  other  "User Library-WS2812-4020_935:2"
  other  "User Library-WS2812-4020_935:3"
  other  "User Library-WS2812-4020_935:4"
  other  "User Library-WS2812-4020_935:5"
  other  "User Library-WS2812-4020_935:6"
  other  "User Library-WS2812-4020_935:7"
  other  "User Library-WS2812-4020_935:8"
  other  "User Library-WS2812-4020_935:9"
  other  "User Library-WS2812-4020_935:10"
  other  "User Library-WS2812-4020_937:1"
  other  "User Library-WS2812-4020_937:2"
  other  "User Library-WS2812-4020_937:3"
  other  "User Library-WS2812-4020_937:4"
  other  "User Library-WS2812-4020_937:5"
  other  "User Library-WS2812-4020_937:6"
  other  "User Library-WS2812-4020_937:7"
  other  "User Library-WS2812-4020_937:8"
  other  "User Library-WS2812-4020_937:9"
  other  "User Library-WS2812-4020_937:10"
  other  "User Library-WS2812-4020_939:1"
  other  "User Library-WS2812-4020_939:2"
  other  "User Library-WS2812-4020_939:3"
  other  "User Library-WS2812-4020_939:4"
  other  "User Library-WS2812-4020_939:5"
  other  "User Library-WS2812-4020_939:6"
  other  "User Library-WS2812-4020_939:7"
  other  "User Library-WS2812-4020_939:8"
  other  "User Library-WS2812-4020_939:9"
  other  "User Library-WS2812-4020_939:10"
  other  "User Library-WS2812-4020_941:1"
  other  "User Library-WS2812-4020_941:2"
  other  "User Library-WS2812-4020_941:3"
  other  "User Library-WS2812-4020_941:4"
  other  "User Library-WS2812-4020_941:5"
  other  "User Library-WS2812-4020_941:6"
  other  "User Library-WS2812-4020_941:7"
  other  "User Library-WS2812-4020_941:8"
  other  "User Library-WS2812-4020_941:9"
  other  "User Library-WS2812-4020_941:10"
  other  "User Library-Chip Cap_MLCC_0402 (1005)_943:1"
  other  "User Library-Chip Cap_MLCC_0402 (1005)_945:1"
  other  "User Library-Chip Cap_MLCC_0402 (1005)_947:1"
  other  "User Library-Chip Cap_MLCC_0402 (1005)_949:1"
  other  "User Library-Chip Cap_MLCC_0402 (1005)_951:1"
  other  "User Library-Chip Cap_MLCC_0402 (1005)_953:1"
  other  "CircuitWorks-SOT-23_955:1"
  other  "User Library-User Library-res0402_res0402_body_957:1"
  other  "B3U_1000P[]_959:1"
  other  "CAPC0603_961:1"
  other  "CAPC0603_963:1"
  other  "CircuitWorks-SOT-223_965:1"
  other  "User Library-LED SMD0603_967:1"
  other  "User Library-LED SMD0603_967:2"
  other  "User Library-LED SMD0603_967:3"
  other  "User Library-LED SMD0603_967:4"
  other  "User Library-LED SMD0603_967:5"
  other  "User Library-LED SMD0603_969:1"
  other  "User Library-LED SMD0603_969:2"
  other  "User Library-LED SMD0603_969:3"
  other  "User Library-LED SMD0603_969:4"
  other  "User Library-LED SMD0603_969:5"
  other  "User Library-User Library-res0402_res0402_body_971:1"
  other  "User Library-LED SMD0603_973:1"
  other  "User Library-LED SMD0603_973:2"
  other  "User Library-LED SMD0603_973:3"
  other  "User Library-LED SMD0603_973:4"
  other  "User Library-LED SMD0603_973:5"
  other  "User Library-LED SMD0603_975:1"
  other  "User Library-LED SMD0603_975:2"
  other  "User Library-LED SMD0603_975:3"
  other  "User Library-LED SMD0603_975:4"
  other  "User Library-LED SMD0603_975:5"
  other  "User Library-LED SMD0603_977:1"
  other  "User Library-LED SMD0603_977:2"
  other  "User Library-LED SMD0603_977:3"
  other  "User Library-LED SMD0603_977:4"
  other  "User Library-LED SMD0603_977:5"
  other  "User Library-LED SMD0603_979:1"
  other  "User Library-LED SMD0603_979:2"
  other  "User Library-LED SMD0603_979:3"
  other  "User Library-LED SMD0603_979:4"
  other  "User Library-LED SMD0603_979:5"
  other  "User Library-User Library-res0402_res0402_body_981:1"
  other  "User Library-LED SMD0603_983:1"
  other  "User Library-LED SMD0603_983:2"
  other  "User Library-LED SMD0603_983:3"
  other  "User Library-LED SMD0603_983:4"
  other  "User Library-LED SMD0603_983:5"
  other  "User Library-LED SMD0603_985:1"
  other  "User Library-LED SMD0603_985:2"
  other  "User Library-LED SMD0603_985:3"
  other  "User Library-LED SMD0603_985:4"
  other  "User Library-LED SMD0603_985:5"
  other  "User Library-User Library-res0402_res0402_body_987:1"
  other  "User Library-User Library-res0402_res0402_body_989:1"
  other  "User Library-LED SMD0603_991:1"
  other  "User Library-LED SMD0603_991:2"
  other  "User Library-LED SMD0603_991:3"
  other  "User Library-LED SMD0603_991:4"
  other  "User Library-LED SMD0603_991:5"
  other  "User Library-User Library-res0402_res0402_body_993:1"
  other  "User Library-Chip Cap_MLCC_0402 (1005)_995:1"
  other  "User Library-Chip Cap_MLCC_0402 (1005)_997:1"
  other  "User Library-Chip Cap_MLCC_0402 (1005)_999:1"
  other  "User Library-Chip Cap_MLCC_0402 (1005)_1001:1"
  other  "User Library-Chip Cap_MLCC_0402 (1005)_1003:1"
  other  "User Library-Chip Cap_MLCC_0402 (1005)_1005:1"
  other  "User Library-Chip Cap_MLCC_0402 (1005)_1007:1"
  other  "User Library-Chip Cap_MLCC_0402 (1005)_1009:1"
  other  "User Library-Chip Cap_MLCC_0402 (1005)_1011:1"
  other  "User Library-Chip Cap_MLCC_0402 (1005)_1013:1"
  other  "User Library-Chip Cap_MLCC_0402 (1005)_1015:1"
  other  "User Library-Chip Cap_MLCC_0402 (1005)_1017:1"
  other  "User Library-Chip Cap_MLCC_0402 (1005)_1019:1"
  other  "User Library-Chip Cap_MLCC_0402 (1005)_1021:1"
  other  "User Library-Chip Cap_MLCC_0402 (1005)_1023:1"
  other  "User Library-Chip Cap_MLCC_0402 (1005)_1025:1"
  other  "User Library-Chip Cap_MLCC_0402 (1005)_1027:1"
  other  "User Library-Chip Cap_MLCC_0402 (1005)_1029:1"
  other  "User Library-Chip Cap_MLCC_0402 (1005)_1031:1"
  other  "User Library-Chip Cap_MLCC_0402 (1005)_1033:1"
  other  "User Library-Chip Cap_MLCC_0402 (1005)_1035:1"
  other  "User Library-Chip Cap_MLCC_0402 (1005)_1037:1"
  other  "User Library-Chip Cap_MLCC_0402 (1005)_1039:1"
  other  "User Library-Chip Cap_MLCC_0402 (1005)_1041:1"
  other  "User Library-Chip Cap_MLCC_0402 (1005)_1043:1"
  other  "User Library-Chip Cap_MLCC_0402 (1005)_1045:1"
  other  "User Library-Chip Cap_MLCC_0402 (1005)_1047:1"
  other  "GRM32ER71E226ME15L_1049:1"
  other  "GRM32ER71E226ME15L_1051:1"
  other  "GRM32ER71E226ME15L_1053:1"
  other  "GRM32ER71E226ME15L_1055:1"
  other  "User Library-Chip Cap_MLCC_0402 (1005)_1057:1"
  other  "GRM32ER71E226ME15L_1059:1"
  other  "GRM32ER71E226ME15L_1061:1"
  other  "GRM32ER71E226ME15L_1063:1"
  other  "GRM32ER71E226ME15L_1065:1"
  other  "User Library-Chip Cap_MLCC_0402 (1005)_1067:1"
  other  "User Library-Chip Cap_MLCC_0402 (1005)_1069:1"
  other  "GRM32ER71E226ME15L_1071:1"
  other  "User Library-Chip Cap_MLCC_0402 (1005)_1073:1"
  other  "User Library-Chip Cap_MLCC_0402 (1005)_1075:1"
  other  "GRM32ER71E226ME15L_1077:1"
  other  "GRM32ER71E226ME15L_1079:1"
  other  "GRM32ER71E226ME15L_1081:1"
  other  "User Library-Chip Cap_MLCC_0402 (1005)_1083:1"
  other  "User Library-Chip Cap_MLCC_0402 (1005)_1085:1"
  other  "GRM32ER71E226ME15L_1087:1"
  other  "GRM32ER71E226ME15L_1089:1"
  other  "GRM32ER71E226ME15L_1091:1"
  other  "GRM32ER71E226ME15L_1093:1"
  other  "User Library-Chip Cap_MLCC_0402 (1005)_1095:1"
  other  "User Library-Chip Cap_MLCC_0402 (1005)_1097:1"
  other  "User Library-Chip Cap_MLCC_0402 (1005)_1099:1"
  other  "User Library-Chip Cap_MLCC_0402 (1005)_1101:1"
  other  "User Library-Chip Cap_MLCC_0402 (1005)_1103:1"
  other  "User Library-Chip Cap_MLCC_0402 (1005)_1105:1"
  other  "User Library-Chip Cap_MLCC_0402 (1005)_1107:1"
  other  "User Library-Chip Cap_MLCC_0402 (1005)_1109:1"
  other  "User Library-Chip Cap_MLCC_0402 (1005)_1111:1"
  other  "User Library-Chip Cap_MLCC_0402 (1005)_1113:1"
  other  "User Library-Chip Cap_MLCC_0402 (1005)_1115:1"
  other  "User Library-Chip Cap_MLCC_0402 (1005)_1117:1"
  other  "User Library-Chip Cap_MLCC_0402 (1005)_1119:1"
  other  "User Library-Chip Cap_MLCC_0402 (1005)_1121:1"
  other  "User Library-Chip Cap_MLCC_0402 (1005)_1123:1"
  other  "User Library-Chip Cap_MLCC_0402 (1005)_1125:1"
  other  "User Library-Chip Cap_MLCC_0402 (1005)_1127:1"
  other  "User Library-Chip Cap_MLCC_0402 (1005)_1129:1"
  other  "User Library-Chip Cap_MLCC_0402 (1005)_1131:1"
  other  "User Library-Chip Cap_MLCC_0402 (1005)_1133:1"
  other  "CAPC0603_1135:1"
  other  "CAPC0603_1137:1"
  other  "User Library-Chip Cap_MLCC_0402 (1005)_1139:1"
  other  "User Library-Chip Cap_MLCC_0402 (1005)_1141:1"
  other  "User Library-GeyerElectronics_KX7_1143:1"
  other  "User Library-GeyerElectronics_KX7_1143:2"
  other  "User Library-GeyerElectronics_KX7_1143:3"
  other  "User Library-GeyerElectronics_KX7_1143:4"
  other  "User Library-640456-4_1145:1"
  other  "User Library-640456-4_1146:1"
  other  "Open CASCADE STEP translator 7.5 1.132.1.1_1148:1"
  other  "User Library-2047110001_1152:1"
  other  "User Library-2047110001_1154:1"
  other  "86A--3DModel-STEP-56544_1156:1"
  other  "86A--3DModel-STEP-56544_1156:2"
  other  "86A--3DModel-STEP-56544_1156:3"
  other  "86A--3DModel-STEP-56544_1156:4"
  other  "86A--3DModel-STEP-56544_1158:1"
  other  "86A--3DModel-STEP-56544_1158:2"
  other  "86A--3DModel-STEP-56544_1158:3"
  other  "86A--3DModel-STEP-56544_1158:4"
  other  "User Library-LED SMD0603_1160:1"
  other  "User Library-LED SMD0603_1160:2"
  other  "User Library-LED SMD0603_1160:3"
  other  "User Library-LED SMD0603_1160:4"
  other  "User Library-LED SMD0603_1160:5"
  other  "User Library-LED SMD0603_1162:1"
  other  "User Library-LED SMD0603_1162:2"
  other  "User Library-LED SMD0603_1162:3"
  other  "User Library-LED SMD0603_1162:4"
  other  "User Library-LED SMD0603_1162:5"
  other  "User Library-SOD323F-1_1164:1"
  other  "B3U_1000P[]_1166:1"
  other  "User Library-IT-1187_1168:1"
  other  "User Library-IT-1187_1170:1"
  other  "push-fit_1172:1"
  other  "Linit Switch_1173:1"
  other  "Linit Switch_1173:2"
  other  "Linit Switch_1173:3"
  other  "Linit Switch_1173:4"
  other  "push-fit_1172:2"
  other  "Linit Switch_1173:5"
  other  "Linit Switch_1173:6"
  other  "Linit Switch_1173:7"
  other  "Linit Switch_1173:8"
  other  "User Library-IT-1187_1178:1"
  other  "User Library-IT-1187_1180:1"
  other  "User Library-User Library-res0402_res0402_body_1182:1"
  other  "User Library-User Library-res0402_res0402_body_1184:1"
  other  "User Library-User Library-res0402_res0402_body_1186:1"
  other  "User Library-User Library-res0402_res0402_body_1188:1"
  other  "User Library-User Library-res0402_res0402_body_1190:1"
  other  "User Library-User Library-res0402_res0402_body_1192:1"
  other  "User Library-User Library-res0402_res0402_body_1194:1"
  other  "User Library-User Library-res0402_res0402_body_1196:1"
  other  "User Library-User Library-res0402_res0402_body_1198:1"
  other  "User Library-User Library-res0402_res0402_body_1200:1"
  other  "User Library-User Library-res0402_res0402_body_1202:1"
  other  "User Library-User Library-res0402_res0402_body_1204:1"
  other  "User Library-User Library-res0402_res0402_body_1206:1"
  other  "User Library-User Library-res0402_res0402_body_1208:1"
  other  "User Library-User Library-res0402_res0402_body_1210:1"
  other  "User Library-User Library-res0402_res0402_body_1212:1"
  other  "User Library-User Library-res0402_res0402_body_1214:1"
  other  "User Library-User Library-res0402_res0402_body_1216:1"
  other  "User Library-User Library-res0402_res0402_body_1218:1"
  other  "User Library-User Library-res0402_res0402_body_1220:1"
  other  "User Library-User Library-res0402_res0402_body_1222:1"
  other  "User Library-User Library-res0402_res0402_body_1224:1"
  other  "User Library-User Library-res0402_res0402_body_1226:1"
  other  "User Library-User Library-res0402_res0402_body_1228:1"
  other  "User Library-User Library-res0402_res0402_body_1230:1"
  other  "User Library-User Library-res0402_res0402_body_1232:1"
  other  "User Library-User Library-res0402_res0402_body_1234:1"
  other  "User Library-User Library-res0402_res0402_body_1236:1"
  other  "User Library-User Library-res0402_res0402_body_1238:1"
  other  "User Library-User Library-res0402_res0402_body_1240:1"
  other  "User Library-User Library-res0402_res0402_body_1242:1"
  other  "User Library-User Library-res0402_res0402_body_1244:1"
  other  "User Library-User Library-res0402_res0402_body_1246:1"
  other  "User Library-User Library-res0402_res0402_body_1248:1"
  other  "User Library-741C083_1250:1"
  other  "User Library-741C083_1250:2"
  other  "User Library-User Library-res0402_res0402_body_1252:1"
  other  "User Library-User Library-res0402_res0402_body_1254:1"
  other  "User Library-User Library-res0402_res0402_body_1256:1"
  other  "User Library-User Library-res0402_res0402_body_1258:1"
  other  "User Library-User Library-res0402_res0402_body_1260:1"
  other  "User Library-User Library-res0402_res0402_body_1262:1"
  other  "User Library-User Library-res0402_res0402_body_1264:1"
  other  "User Library-User Library-res0402_res0402_body_1266:1"
  other  "User Library-User Library-res0402_res0402_body_1268:1"
  other  "User Library-User Library-res0402_res0402_body_1270:1"
  other  "User Library-User Library-res0402_res0402_body_1272:1"
  other  "User Library-User Library-res0402_res0402_body_1274:1"
  other  "User Library-User Library-res0402_res0402_body_1276:1"
  other  "User Library-User Library-res0402_res0402_body_1278:1"
  other  "User Library-User Library-res0402_res0402_body_1280:1"
  other  "User Library-User Library-res0402_res0402_body_1282:1"
  other  "User Library-User Library-res0402_res0402_body_1284:1"
  other  "User Library-741C083_1286:1"
  other  "User Library-741C083_1286:2"
  other  "User Library-741C083_1288:1"
  other  "User Library-741C083_1288:2"
  other  "User Library-User Library-res0402_res0402_body_1290:1"
  other  "User Library-741C083_1292:1"
  other  "User Library-741C083_1292:2"
  other  "User Library-741C083_1294:1"
  other  "User Library-741C083_1294:2"
  other  "User Library-741C083_1296:1"
  other  "User Library-741C083_1296:2"
  other  "User Library-741C083_1298:1"
  other  "User Library-741C083_1298:2"
  other  "User Library-741C083_1300:1"
  other  "User Library-741C083_1300:2"
  other  "User Library-User Library-res0402_res0402_body_1302:1"
  other  "User Library-User Library-res0402_res0402_body_1304:1"
  other  "User Library-User Library-res0402_res0402_body_1306:1"
  other  "User Library-User Library-res0402_res0402_body_1308:1"
  other  "User Library-User Library-res0402_res0402_body_1310:1"
  other  "User Library-User Library-res0402_res0402_body_1312:1"
  other  "User Library-User Library-res0402_res0402_body_1314:1"
  other  "User Library-Bourns_SRP1038A_series_CASE-Non-Lead-Frame_1316:1"
  other  "User Library-Bourns_SRP1038A_series_CASE-Non-Lead-Frame_1316:2"
  other  "User Library-Bourns_SRP1038A_series_CASE-Non-Lead-Frame_1316:3"
  other  "User Library-Bourns_SRP1038A_series_CASE-Non-Lead-Frame_1318:1"
  other  "User Library-Bourns_SRP1038A_series_CASE-Non-Lead-Frame_1318:2"
  other  "User Library-Bourns_SRP1038A_series_CASE-Non-Lead-Frame_1318:3"
  other  "User Library-WS2812-4020_1320:1"
  other  "User Library-WS2812-4020_1320:2"
  other  "User Library-WS2812-4020_1320:3"
  other  "User Library-WS2812-4020_1320:4"
  other  "User Library-WS2812-4020_1320:5"
  other  "User Library-WS2812-4020_1320:6"
  other  "User Library-WS2812-4020_1320:7"
  other  "User Library-WS2812-4020_1320:8"
  other  "User Library-WS2812-4020_1320:9"
  other  "User Library-WS2812-4020_1320:10"
  other  "User Library-WS2812-4020_1322:1"
  other  "User Library-WS2812-4020_1322:2"
  other  "User Library-WS2812-4020_1322:3"
  other  "User Library-WS2812-4020_1322:4"
  other  "User Library-WS2812-4020_1322:5"
  other  "User Library-WS2812-4020_1322:6"
  other  "User Library-WS2812-4020_1322:7"
  other  "User Library-WS2812-4020_1322:8"
  other  "User Library-WS2812-4020_1322:9"
  other  "User Library-WS2812-4020_1322:10"
  other  "User Library-WS2812-4020_1324:1"
  other  "User Library-WS2812-4020_1324:2"
  other  "User Library-WS2812-4020_1324:3"
  other  "User Library-WS2812-4020_1324:4"
  other  "User Library-WS2812-4020_1324:5"
  other  "User Library-WS2812-4020_1324:6"
  other  "User Library-WS2812-4020_1324:7"
  other  "User Library-WS2812-4020_1324:8"
  other  "User Library-WS2812-4020_1324:9"
  other  "User Library-WS2812-4020_1324:10"
  other  "User Library-WS2812-4020_1326:1"
  other  "User Library-WS2812-4020_1326:2"
  other  "User Library-WS2812-4020_1326:3"
  other  "User Library-WS2812-4020_1326:4"
  other  "User Library-WS2812-4020_1326:5"
  other  "User Library-WS2812-4020_1326:6"
  other  "User Library-WS2812-4020_1326:7"
  other  "User Library-WS2812-4020_1326:8"
  other  "User Library-WS2812-4020_1326:9"
  other  "User Library-WS2812-4020_1326:10"
  other  "User Library-WS2812-4020_1328:1"
  other  "User Library-WS2812-4020_1328:2"
  other  "User Library-WS2812-4020_1328:3"
  other  "User Library-WS2812-4020_1328:4"
  other  "User Library-WS2812-4020_1328:5"
  other  "User Library-WS2812-4020_1328:6"
  other  "User Library-WS2812-4020_1328:7"
  other  "User Library-WS2812-4020_1328:8"
  other  "User Library-WS2812-4020_1328:9"
  other  "User Library-WS2812-4020_1328:10"
  other  "User Library-WS2812-4020_1330:1"
  other  "User Library-WS2812-4020_1330:2"
  other  "User Library-WS2812-4020_1330:3"
  other  "User Library-WS2812-4020_1330:4"
  other  "User Library-WS2812-4020_1330:5"
  other  "User Library-WS2812-4020_1330:6"
  other  "User Library-WS2812-4020_1330:7"
  other  "User Library-WS2812-4020_1330:8"
  other  "User Library-WS2812-4020_1330:9"
  other  "User Library-WS2812-4020_1330:10"
  other  "User Library-WS2812-4020_1332:1"
  other  "User Library-WS2812-4020_1332:2"
  other  "User Library-WS2812-4020_1332:3"
  other  "User Library-WS2812-4020_1332:4"
  other  "User Library-WS2812-4020_1332:5"
  other  "User Library-WS2812-4020_1332:6"
  other  "User Library-WS2812-4020_1332:7"
  other  "User Library-WS2812-4020_1332:8"
  other  "User Library-WS2812-4020_1332:9"
  other  "User Library-WS2812-4020_1332:10"
  other  "User Library-WS2812-4020_1334:1"
  other  "User Library-WS2812-4020_1334:2"
  other  "User Library-WS2812-4020_1334:3"
  other  "User Library-WS2812-4020_1334:4"
  other  "User Library-WS2812-4020_1334:5"
  other  "User Library-WS2812-4020_1334:6"
  other  "User Library-WS2812-4020_1334:7"
  other  "User Library-WS2812-4020_1334:8"
  other  "User Library-WS2812-4020_1334:9"
  other  "User Library-WS2812-4020_1334:10"
  other  "User Library-WS2812-4020_1336:1"
  other  "User Library-WS2812-4020_1336:2"
  other  "User Library-WS2812-4020_1336:3"
  other  "User Library-WS2812-4020_1336:4"
  other  "User Library-WS2812-4020_1336:5"
  other  "User Library-WS2812-4020_1336:6"
  other  "User Library-WS2812-4020_1336:7"
  other  "User Library-WS2812-4020_1336:8"
  other  "User Library-WS2812-4020_1336:9"
  other  "User Library-WS2812-4020_1336:10"
  other  "User Library-WS2812-4020_1338:1"
  other  "User Library-WS2812-4020_1338:2"
  other  "User Library-WS2812-4020_1338:3"
  other  "User Library-WS2812-4020_1338:4"
  other  "User Library-WS2812-4020_1338:5"
  other  "User Library-WS2812-4020_1338:6"
  other  "User Library-WS2812-4020_1338:7"
  other  "User Library-WS2812-4020_1338:8"
  other  "User Library-WS2812-4020_1338:9"
  other  "User Library-WS2812-4020_1338:10"
  other  "User Library-WS2812-4020_1340:1"
  other  "User Library-WS2812-4020_1340:2"
  other  "User Library-WS2812-4020_1340:3"
  other  "User Library-WS2812-4020_1340:4"
  other  "User Library-WS2812-4020_1340:5"
  other  "User Library-WS2812-4020_1340:6"
  other  "User Library-WS2812-4020_1340:7"
  other  "User Library-WS2812-4020_1340:8"
  other  "User Library-WS2812-4020_1340:9"
  other  "User Library-WS2812-4020_1340:10"
  other  "User Library-WS2812-4020_1342:1"
  other  "User Library-WS2812-4020_1342:2"
  other  "User Library-WS2812-4020_1342:3"
  other  "User Library-WS2812-4020_1342:4"
  other  "User Library-WS2812-4020_1342:5"
  other  "User Library-WS2812-4020_1342:6"
  other  "User Library-WS2812-4020_1342:7"
  other  "User Library-WS2812-4020_1342:8"
  other  "User Library-WS2812-4020_1342:9"
  other  "User Library-WS2812-4020_1342:10"
  other  "User Library-WS2812-4020_1344:1"
  other  "User Library-WS2812-4020_1344:2"
  other  "User Library-WS2812-4020_1344:3"
  other  "User Library-WS2812-4020_1344:4"
  other  "User Library-WS2812-4020_1344:5"
  other  "User Library-WS2812-4020_1344:6"
  other  "User Library-WS2812-4020_1344:7"
  other  "User Library-WS2812-4020_1344:8"
  other  "User Library-WS2812-4020_1344:9"
  other  "User Library-WS2812-4020_1344:10"
  other  "User Library-WS2812-4020_1346:1"
  other  "User Library-WS2812-4020_1346:2"
  other  "User Library-WS2812-4020_1346:3"
  other  "User Library-WS2812-4020_1346:4"
  other  "User Library-WS2812-4020_1346:5"
  other  "User Library-WS2812-4020_1346:6"
  other  "User Library-WS2812-4020_1346:7"
  other  "User Library-WS2812-4020_1346:8"
  other  "User Library-WS2812-4020_1346:9"
  other  "User Library-WS2812-4020_1346:10"
  other  "User Library-WS2812-4020_1348:1"
  other  "User Library-WS2812-4020_1348:2"
  other  "User Library-WS2812-4020_1348:3"
  other  "User Library-WS2812-4020_1348:4"
  other  "User Library-WS2812-4020_1348:5"
  other  "User Library-WS2812-4020_1348:6"
  other  "User Library-WS2812-4020_1348:7"
  other  "User Library-WS2812-4020_1348:8"
  other  "User Library-WS2812-4020_1348:9"
  other  "User Library-WS2812-4020_1348:10"
  other  "User Library-WS2812-4020_1350:1"
  other  "User Library-WS2812-4020_1350:2"
  other  "User Library-WS2812-4020_1350:3"
  other  "User Library-WS2812-4020_1350:4"
  other  "User Library-WS2812-4020_1350:5"
  other  "User Library-WS2812-4020_1350:6"
  other  "User Library-WS2812-4020_1350:7"
  other  "User Library-WS2812-4020_1350:8"
  other  "User Library-WS2812-4020_1350:9"
  other  "User Library-WS2812-4020_1350:10"
  other  "User Library-WS2812-4020_1352:1"
  other  "User Library-WS2812-4020_1352:2"
  other  "User Library-WS2812-4020_1352:3"
  other  "User Library-WS2812-4020_1352:4"
  other  "User Library-WS2812-4020_1352:5"
  other  "User Library-WS2812-4020_1352:6"
  other  "User Library-WS2812-4020_1352:7"
  other  "User Library-WS2812-4020_1352:8"
  other  "User Library-WS2812-4020_1352:9"
  other  "User Library-WS2812-4020_1352:10"
  other  "User Library-WS2812-4020_1354:1"
  other  "User Library-WS2812-4020_1354:2"
  other  "User Library-WS2812-4020_1354:3"
  other  "User Library-WS2812-4020_1354:4"
  other  "User Library-WS2812-4020_1354:5"
  other  "User Library-WS2812-4020_1354:6"
  other  "User Library-WS2812-4020_1354:7"
  other  "User Library-WS2812-4020_1354:8"
  other  "User Library-WS2812-4020_1354:9"
  other  "User Library-WS2812-4020_1354:10"
  other  "User Library-WS2812-4020_1356:1"
  other  "User Library-WS2812-4020_1356:2"
  other  "User Library-WS2812-4020_1356:3"
  other  "User Library-WS2812-4020_1356:4"
  other  "User Library-WS2812-4020_1356:5"
  other  "User Library-WS2812-4020_1356:6"
  other  "User Library-WS2812-4020_1356:7"
  other  "User Library-WS2812-4020_1356:8"
  other  "User Library-WS2812-4020_1356:9"
  other  "User Library-WS2812-4020_1356:10"
  other  "User Library-WS2812-4020_1358:1"
  other  "User Library-WS2812-4020_1358:2"
  other  "User Library-WS2812-4020_1358:3"
  other  "User Library-WS2812-4020_1358:4"
  other  "User Library-WS2812-4020_1358:5"
  other  "User Library-WS2812-4020_1358:6"
  other  "User Library-WS2812-4020_1358:7"
  other  "User Library-WS2812-4020_1358:8"
  other  "User Library-WS2812-4020_1358:9"
  other  "User Library-WS2812-4020_1358:10"
  other  "User Library-WS2812-4020_1360:1"
  other  "User Library-WS2812-4020_1360:2"
  other  "User Library-WS2812-4020_1360:3"
  other  "User Library-WS2812-4020_1360:4"
  other  "User Library-WS2812-4020_1360:5"
  other  "User Library-WS2812-4020_1360:6"
  other  "User Library-WS2812-4020_1360:7"
  other  "User Library-WS2812-4020_1360:8"
  other  "User Library-WS2812-4020_1360:9"
  other  "User Library-WS2812-4020_1360:10"
  other  "User Library-WS2812-4020_1362:1"
  other  "User Library-WS2812-4020_1362:2"
  other  "User Library-WS2812-4020_1362:3"
  other  "User Library-WS2812-4020_1362:4"
  other  "User Library-WS2812-4020_1362:5"
  other  "User Library-WS2812-4020_1362:6"
  other  "User Library-WS2812-4020_1362:7"
  other  "User Library-WS2812-4020_1362:8"
  other  "User Library-WS2812-4020_1362:9"
  other  "User Library-WS2812-4020_1362:10"
  other  "User Library-WS2812-4020_1364:1"
  other  "User Library-WS2812-4020_1364:2"
  other  "User Library-WS2812-4020_1364:3"
  other  "User Library-WS2812-4020_1364:4"
  other  "User Library-WS2812-4020_1364:5"
  other  "User Library-WS2812-4020_1364:6"
  other  "User Library-WS2812-4020_1364:7"
  other  "User Library-WS2812-4020_1364:8"
  other  "User Library-WS2812-4020_1364:9"
  other  "User Library-WS2812-4020_1364:10"
  other  "User Library-WS2812-4020_1366:1"
  other  "User Library-WS2812-4020_1366:2"
  other  "User Library-WS2812-4020_1366:3"
  other  "User Library-WS2812-4020_1366:4"
  other  "User Library-WS2812-4020_1366:5"
  other  "User Library-WS2812-4020_1366:6"
  other  "User Library-WS2812-4020_1366:7"
  other  "User Library-WS2812-4020_1366:8"
  other  "User Library-WS2812-4020_1366:9"
  other  "User Library-WS2812-4020_1366:10"
  other  "User Library-QFN24_4x4x0_75_p0_5_1368:1"
  other  "MC33926 8X8X2_1370:1"
  other  "MC33926 8X8X2_1370:2"
  other  "MC33926 8X8X2_1370:3"
  other  "MC33926 8X8X2_1370:4"
  other  "MC33926 8X8X2_1370:5"
  other  "MC33926 8X8X2_1370:6"
  other  "MC33926 8X8X2_1370:7"
  other  "MC33926 8X8X2_1370:8"
  other  "MC33926 8X8X2_1370:9"
  other  "MC33926 8X8X2_1370:10"
  other  "MC33926 8X8X2_1370:11"
  other  "MC33926 8X8X2_1370:12"
  other  "MC33926 8X8X2_1370:13"
  other  "MC33926 8X8X2_1370:14"
  other  "MC33926 8X8X2_1370:15"
  other  "MC33926 8X8X2_1370:16"
  other  "MC33926 8X8X2_1370:17"
  other  "MC33926 8X8X2_1370:18"
  other  "MC33926 8X8X2_1370:19"
  other  "MC33926 8X8X2_1370:20"
  other  "MC33926 8X8X2_1370:21"
  other  "MC33926 8X8X2_1370:22"
  other  "MC33926 8X8X2_1370:23"
  other  "MC33926 8X8X2_1370:24"
  other  "MC33926 8X8X2_1370:25"
  other  "MC33926 8X8X2_1370:26"
  other  "MC33926 8X8X2_1370:27"
  other  "MC33926 8X8X2_1370:28"
  other  "MC33926 8X8X2_1370:29"
  other  "MC33926 8X8X2_1370:30"
  other  "MC33926 8X8X2_1370:31"
  other  "MC33926 8X8X2_1370:32"
  other  "MC33926 8X8X2_1370:33"
  other  "MC33926 8X8X2_1372:1"
  other  "MC33926 8X8X2_1372:2"
  other  "MC33926 8X8X2_1372:3"
  other  "MC33926 8X8X2_1372:4"
  other  "MC33926 8X8X2_1372:5"
  other  "MC33926 8X8X2_1372:6"
  other  "MC33926 8X8X2_1372:7"
  other  "MC33926 8X8X2_1372:8"
  other  "MC33926 8X8X2_1372:9"
  other  "MC33926 8X8X2_1372:10"
  other  "MC33926 8X8X2_1372:11"
  other  "MC33926 8X8X2_1372:12"
  other  "MC33926 8X8X2_1372:13"
  other  "MC33926 8X8X2_1372:14"
  other  "MC33926 8X8X2_1372:15"
  other  "MC33926 8X8X2_1372:16"
  other  "MC33926 8X8X2_1372:17"
  other  "MC33926 8X8X2_1372:18"
  other  "MC33926 8X8X2_1372:19"
  other  "MC33926 8X8X2_1372:20"
  other  "MC33926 8X8X2_1372:21"
  other  "MC33926 8X8X2_1372:22"
  other  "MC33926 8X8X2_1372:23"
  other  "MC33926 8X8X2_1372:24"
  other  "MC33926 8X8X2_1372:25"
  other  "MC33926 8X8X2_1372:26"
  other  "MC33926 8X8X2_1372:27"
  other  "MC33926 8X8X2_1372:28"
  other  "MC33926 8X8X2_1372:29"
  other  "MC33926 8X8X2_1372:30"
  other  "MC33926 8X8X2_1372:31"
  other  "MC33926 8X8X2_1372:32"
  other  "MC33926 8X8X2_1372:33"
  other  "BODY-SON_1374:1"
  other  "Open CASCADE STEP translator 7.5 1.243.1.2.1_1375:1"
  other  "Open CASCADE STEP translator 7.5 1.243.1.2.2_1376:1"
  other  "Open CASCADE STEP translator 7.5 1.243.1.2.3_1377:1"
  other  "Open CASCADE STEP translator 7.5 1.243.1.2.4_1378:1"
  other  "Open CASCADE STEP translator 7.5 1.243.1.2.5_1379:1"
  other  "Open CASCADE STEP translator 7.5 1.243.1.2.6_1380:1"
  other  "Open CASCADE STEP translator 7.5 1.243.1.2.7_1381:1"
  other  "Open CASCADE STEP translator 7.5 1.243.1.2.8_1382:1"
  other  "Open CASCADE STEP translator 7.5 1.243.1.2.9_1383:1"
  other  "Open CASCADE STEP translator 7.5 1.243.1.2.10_1384:1"
  other  "Open CASCADE STEP translator 7.5 1.243.1.2.11_1385:1"
  other  "BODY-SON_1374:2"
  other  "Open CASCADE STEP translator 7.5 1.243.1.2.1_1375:2"
  other  "Open CASCADE STEP translator 7.5 1.243.1.2.2_1376:2"
  other  "Open CASCADE STEP translator 7.5 1.243.1.2.3_1377:2"
  other  "Open CASCADE STEP translator 7.5 1.243.1.2.4_1378:2"
  other  "Open CASCADE STEP translator 7.5 1.243.1.2.5_1379:2"
  other  "Open CASCADE STEP translator 7.5 1.243.1.2.6_1380:2"
  other  "Open CASCADE STEP translator 7.5 1.243.1.2.7_1381:2"
  other  "Open CASCADE STEP translator 7.5 1.243.1.2.8_1382:2"
  other  "Open CASCADE STEP translator 7.5 1.243.1.2.9_1383:2"
  other  "Open CASCADE STEP translator 7.5 1.243.1.2.10_1384:2"
  other  "Open CASCADE STEP translator 7.5 1.243.1.2.11_1385:2"
  other  "User Library-SOT353-1-1_1392:1"
  other  "User Library-SOT353-1-1_1392:2"
  other  "User Library-SOT353-1-1_1392:3"
  other  "User Library-SOT353-1-1_1392:4"
  other  "User Library-SOT353-1-1_1392:5"
  other  "User Library-SOT353-1-1_1392:6"
  extrude  "Extruded_1394:1"  [1 undecoded]
  other  "128x32-OLED_1397:1"
  other  "Составной1"
  other  "SRF1"
note: 2 required parameter values undecoded (feature->parameter linkage not recoverable at this tier; creation-order binding heuristic only, values carry confidence <= 0.55)
